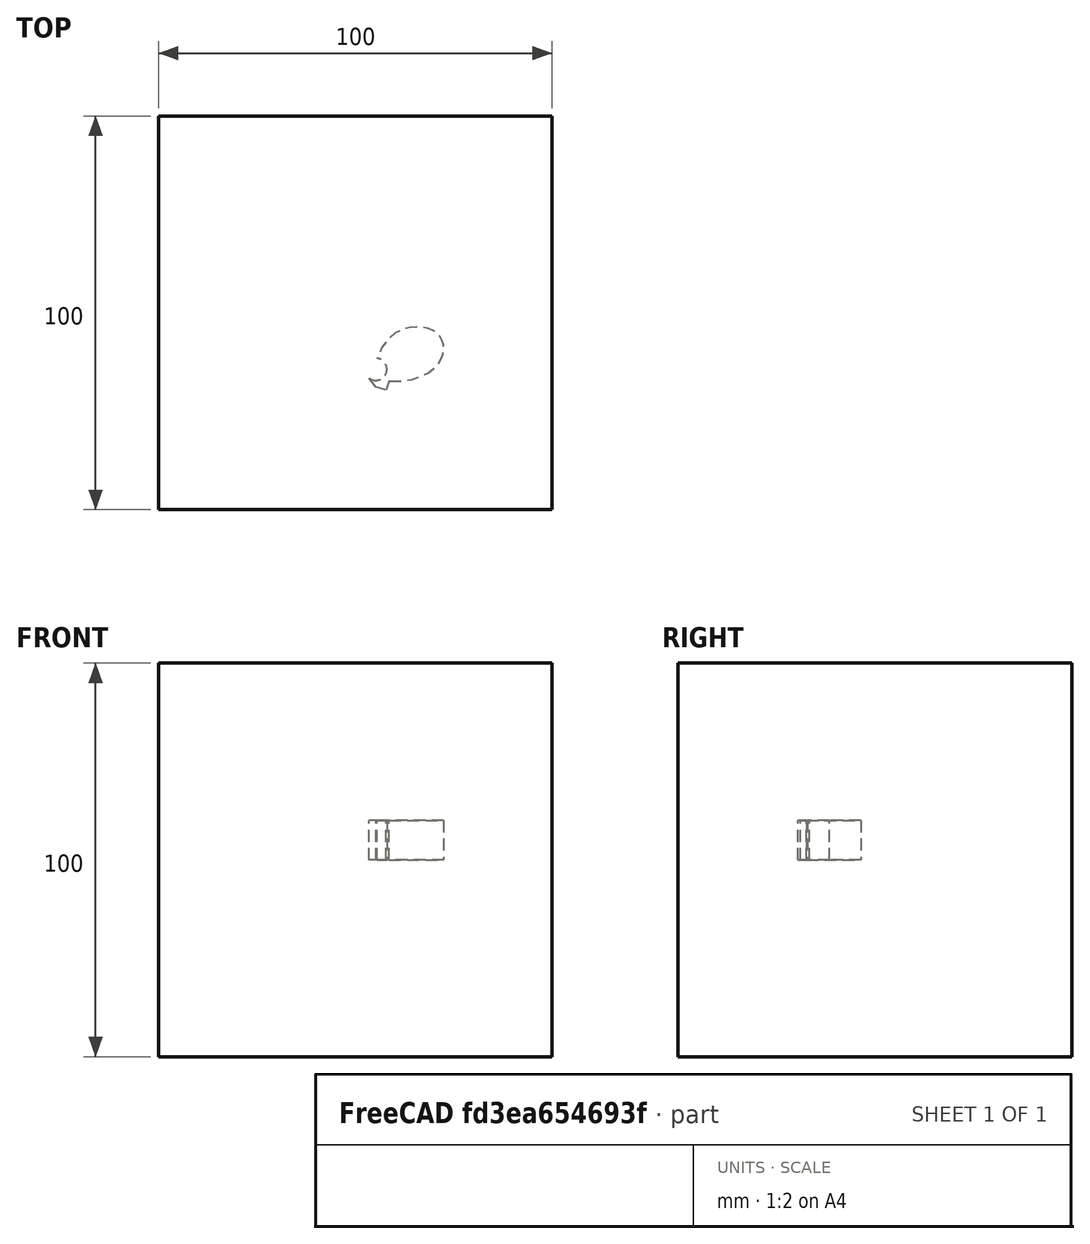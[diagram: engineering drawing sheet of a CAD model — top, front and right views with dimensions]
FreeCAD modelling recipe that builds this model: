
FCSTD DOCUMENT  (FreeCAD 0.19RUnknown)
Label: mirrorTest-1b
License: All rights reserved
LicenseURL: http://en.wikipedia.org/wiki/All_rights_reserved
objects: App::DocumentObjectGroupPython×1248, App::Part×2, Part::FeaturePython×1, Sketcher::SketchObject×1, Part::Extrusion×1, Part::Mirroring×1
note: 4 computed .brp shape members not serialized (recipe doc carries the construction recipe); baked Part::Feature solids carry a one-line shape summary decoded from their .brp

FEATURE [App::DocumentObjectGroupPython] HALFPI  # scripted group (container) (typed FeaturePython)
  name = HALFPI
  value = pi/2.
FEATURE [App::DocumentObjectGroupPython] PI  # scripted group (container) (typed FeaturePython)
  name = PI
  value = 1.*pi
FEATURE [App::DocumentObjectGroupPython] TWOPI  # scripted group (container) (typed FeaturePython)
  name = TWOPI
  value = 2.*pi
FEATURE [App::DocumentObjectGroupPython] Constants  # scripted group (container) (typed FeaturePython)
  Group = -> [HALFPI,PI,TWOPI]
FEATURE [App::DocumentObjectGroupPython] Variables  # scripted group (container) (typed FeaturePython)
FEATURE [App::DocumentObjectGroupPython] Quantities  # scripted group (container) (typed FeaturePython)
FEATURE [App::DocumentObjectGroupPython] Isotopes  # scripted group (container) (typed FeaturePython)
FEATURE [App::DocumentObjectGroupPython] Elements  # scripted group (container) (typed FeaturePython)
FEATURE [App::DocumentObjectGroupPython] G4Isotopes  # scripted group (container) (typed FeaturePython)
FEATURE [App::DocumentObjectGroupPython] H_element  # scripted group (container) (typed FeaturePython)
  Z = 1
  atom_value = 1.008
  formula = H
  name = H_element
FEATURE [App::DocumentObjectGroupPython] He_element  # scripted group (container) (typed FeaturePython)
  Z = 2
  atom_value = 4.0026
  formula = He
  name = He_element
FEATURE [App::DocumentObjectGroupPython] Li_element  # scripted group (container) (typed FeaturePython)
  Z = 3
  atom_value = 6.94
  formula = Li
  name = Li_element
FEATURE [App::DocumentObjectGroupPython] Be_element  # scripted group (container) (typed FeaturePython)
  Z = 4
  atom_value = 9.01218
  formula = Be
  name = Be_element
FEATURE [App::DocumentObjectGroupPython] B_element  # scripted group (container) (typed FeaturePython)
  Z = 5
  atom_value = 10.81
  formula = B
  name = B_element
FEATURE [App::DocumentObjectGroupPython] C_element  # scripted group (container) (typed FeaturePython)
  Z = 6
  atom_value = 12.011
  formula = C
  name = C_element
FEATURE [App::DocumentObjectGroupPython] N_element  # scripted group (container) (typed FeaturePython)
  Z = 7
  atom_value = 14.007
  formula = N
  name = N_element
FEATURE [App::DocumentObjectGroupPython] O_element  # scripted group (container) (typed FeaturePython)
  Z = 8
  atom_value = 15.999
  formula = O
  name = O_element
FEATURE [App::DocumentObjectGroupPython] F_element  # scripted group (container) (typed FeaturePython)
  Z = 9
  atom_value = 18.9984
  formula = F
  name = F_element
FEATURE [App::DocumentObjectGroupPython] Ne_element  # scripted group (container) (typed FeaturePython)
  Z = 10
  atom_value = 20.1797
  formula = Ne
  name = Ne_element
FEATURE [App::DocumentObjectGroupPython] Na_element  # scripted group (container) (typed FeaturePython)
  Z = 11
  atom_value = 22.9898
  formula = Na
  name = Na_element
FEATURE [App::DocumentObjectGroupPython] Mg_element  # scripted group (container) (typed FeaturePython)
  Z = 12
  atom_value = 24.305
  formula = Mg
  name = Mg_element
FEATURE [App::DocumentObjectGroupPython] Al_element  # scripted group (container) (typed FeaturePython)
  Z = 13
  atom_value = 26.9815
  formula = Al
  name = Al_element
FEATURE [App::DocumentObjectGroupPython] Si_element  # scripted group (container) (typed FeaturePython)
  Z = 14
  atom_value = 28.085
  formula = Si
  name = Si_element
FEATURE [App::DocumentObjectGroupPython] P_element  # scripted group (container) (typed FeaturePython)
  Z = 15
  atom_value = 30.9738
  formula = P
  name = P_element
FEATURE [App::DocumentObjectGroupPython] S_element  # scripted group (container) (typed FeaturePython)
  Z = 16
  atom_value = 32.06
  formula = S
  name = S_element
FEATURE [App::DocumentObjectGroupPython] Cl_element  # scripted group (container) (typed FeaturePython)
  Z = 17
  atom_value = 35.45
  formula = Cl
  name = Cl_element
FEATURE [App::DocumentObjectGroupPython] Ar_element  # scripted group (container) (typed FeaturePython)
  Z = 18
  atom_value = 39.95
  formula = Ar
  name = Ar_element
FEATURE [App::DocumentObjectGroupPython] K_element  # scripted group (container) (typed FeaturePython)
  Z = 19
  atom_value = 39.0983
  formula = K
  name = K_element
FEATURE [App::DocumentObjectGroupPython] Ca_element  # scripted group (container) (typed FeaturePython)
  Z = 20
  atom_value = 40.078
  formula = Ca
  name = Ca_element
FEATURE [App::DocumentObjectGroupPython] Sc_element  # scripted group (container) (typed FeaturePython)
  Z = 21
  atom_value = 44.9559
  formula = Sc
  name = Sc_element
FEATURE [App::DocumentObjectGroupPython] Ti_element  # scripted group (container) (typed FeaturePython)
  Z = 22
  atom_value = 47.867
  formula = Ti
  name = Ti_element
FEATURE [App::DocumentObjectGroupPython] V_element  # scripted group (container) (typed FeaturePython)
  Z = 23
  atom_value = 50.9415
  formula = V
  name = V_element
FEATURE [App::DocumentObjectGroupPython] Cr_element  # scripted group (container) (typed FeaturePython)
  Z = 24
  atom_value = 51.9961
  formula = Cr
  name = Cr_element
FEATURE [App::DocumentObjectGroupPython] Mn_element  # scripted group (container) (typed FeaturePython)
  Z = 25
  atom_value = 54.938
  formula = Mn
  name = Mn_element
FEATURE [App::DocumentObjectGroupPython] Fe_element  # scripted group (container) (typed FeaturePython)
  Z = 26
  atom_value = 55.845
  formula = Fe
  name = Fe_element
FEATURE [App::DocumentObjectGroupPython] Co_element  # scripted group (container) (typed FeaturePython)
  Z = 27
  atom_value = 58.9332
  formula = Co
  name = Co_element
FEATURE [App::DocumentObjectGroupPython] Ni_element  # scripted group (container) (typed FeaturePython)
  Z = 28
  atom_value = 58.6934
  formula = Ni
  name = Ni_element
FEATURE [App::DocumentObjectGroupPython] Cu_element  # scripted group (container) (typed FeaturePython)
  Z = 29
  atom_value = 63.546
  formula = Cu
  name = Cu_element
FEATURE [App::DocumentObjectGroupPython] Zn_element  # scripted group (container) (typed FeaturePython)
  Z = 30
  atom_value = 65.38
  formula = Zn
  name = Zn_element
FEATURE [App::DocumentObjectGroupPython] Ga_element  # scripted group (container) (typed FeaturePython)
  Z = 31
  atom_value = 69.723
  formula = Ga
  name = Ga_element
FEATURE [App::DocumentObjectGroupPython] Ge_element  # scripted group (container) (typed FeaturePython)
  Z = 32
  atom_value = 72.63
  formula = Ge
  name = Ge_element
FEATURE [App::DocumentObjectGroupPython] As_element  # scripted group (container) (typed FeaturePython)
  Z = 33
  atom_value = 74.9216
  formula = As
  name = As_element
FEATURE [App::DocumentObjectGroupPython] Se_element  # scripted group (container) (typed FeaturePython)
  Z = 34
  atom_value = 78.971
  formula = Se
  name = Se_element
FEATURE [App::DocumentObjectGroupPython] Br_element  # scripted group (container) (typed FeaturePython)
  Z = 35
  atom_value = 79.904
  formula = Br
  name = Br_element
FEATURE [App::DocumentObjectGroupPython] Kr_element  # scripted group (container) (typed FeaturePython)
  Z = 36
  atom_value = 83.798
  formula = Kr
  name = Kr_element
FEATURE [App::DocumentObjectGroupPython] Rb_element  # scripted group (container) (typed FeaturePython)
  Z = 37
  atom_value = 85.4678
  formula = Rb
  name = Rb_element
FEATURE [App::DocumentObjectGroupPython] Sr_element  # scripted group (container) (typed FeaturePython)
  Z = 38
  atom_value = 87.62
  formula = Sr
  name = Sr_element
FEATURE [App::DocumentObjectGroupPython] Y_element  # scripted group (container) (typed FeaturePython)
  Z = 39
  atom_value = 88.9058
  formula = Y
  name = Y_element
FEATURE [App::DocumentObjectGroupPython] Zr_element  # scripted group (container) (typed FeaturePython)
  Z = 40
  atom_value = 91.224
  formula = Zr
  name = Zr_element
FEATURE [App::DocumentObjectGroupPython] Nb_element  # scripted group (container) (typed FeaturePython)
  Z = 41
  atom_value = 92.9064
  formula = Nb
  name = Nb_element
FEATURE [App::DocumentObjectGroupPython] Mo_element  # scripted group (container) (typed FeaturePython)
  Z = 42
  atom_value = 95.95
  formula = Mo
  name = Mo_element
FEATURE [App::DocumentObjectGroupPython] Tc_element  # scripted group (container) (typed FeaturePython)
  Z = 43
  atom_value = 97
  formula = Tc
  name = Tc_element
FEATURE [App::DocumentObjectGroupPython] Ru_element  # scripted group (container) (typed FeaturePython)
  Z = 44
  atom_value = 101.07
  formula = Ru
  name = Ru_element
FEATURE [App::DocumentObjectGroupPython] Rh_element  # scripted group (container) (typed FeaturePython)
  Z = 45
  atom_value = 102.905
  formula = Rh
  name = Rh_element
FEATURE [App::DocumentObjectGroupPython] Pd_element  # scripted group (container) (typed FeaturePython)
  Z = 46
  atom_value = 106.42
  formula = Pd
  name = Pd_element
FEATURE [App::DocumentObjectGroupPython] Ag_element  # scripted group (container) (typed FeaturePython)
  Z = 47
  atom_value = 107.868
  formula = Ag
  name = Ag_element
FEATURE [App::DocumentObjectGroupPython] Cd_element  # scripted group (container) (typed FeaturePython)
  Z = 48
  atom_value = 112.414
  formula = Cd
  name = Cd_element
FEATURE [App::DocumentObjectGroupPython] In_element  # scripted group (container) (typed FeaturePython)
  Z = 49
  atom_value = 114.818
  formula = In
  name = In_element
FEATURE [App::DocumentObjectGroupPython] Sn_element  # scripted group (container) (typed FeaturePython)
  Z = 50
  atom_value = 118.71
  formula = Sn
  name = Sn_element
FEATURE [App::DocumentObjectGroupPython] Sb_element  # scripted group (container) (typed FeaturePython)
  Z = 51
  atom_value = 121.76
  formula = Sb
  name = Sb_element
FEATURE [App::DocumentObjectGroupPython] Te_element  # scripted group (container) (typed FeaturePython)
  Z = 52
  atom_value = 127.6
  formula = Te
  name = Te_element
FEATURE [App::DocumentObjectGroupPython] I_element  # scripted group (container) (typed FeaturePython)
  Z = 53
  atom_value = 126.904
  formula = I
  name = I_element
FEATURE [App::DocumentObjectGroupPython] Xe_element  # scripted group (container) (typed FeaturePython)
  Z = 54
  atom_value = 131.293
  formula = Xe
  name = Xe_element
FEATURE [App::DocumentObjectGroupPython] Cs_element  # scripted group (container) (typed FeaturePython)
  Z = 55
  atom_value = 132.905
  formula = Cs
  name = Cs_element
FEATURE [App::DocumentObjectGroupPython] Ba_element  # scripted group (container) (typed FeaturePython)
  Z = 56
  atom_value = 137.327
  formula = Ba
  name = Ba_element
FEATURE [App::DocumentObjectGroupPython] La_element  # scripted group (container) (typed FeaturePython)
  Z = 57
  atom_value = 138.905
  formula = La
  name = La_element
FEATURE [App::DocumentObjectGroupPython] Ce_element  # scripted group (container) (typed FeaturePython)
  Z = 58
  atom_value = 140.116
  formula = Ce
  name = Ce_element
FEATURE [App::DocumentObjectGroupPython] Pr_element  # scripted group (container) (typed FeaturePython)
  Z = 59
  atom_value = 140.908
  formula = Pr
  name = Pr_element
FEATURE [App::DocumentObjectGroupPython] Nd_element  # scripted group (container) (typed FeaturePython)
  Z = 60
  atom_value = 144.242
  formula = Nd
  name = Nd_element
FEATURE [App::DocumentObjectGroupPython] Pm_element  # scripted group (container) (typed FeaturePython)
  Z = 61
  atom_value = 145
  formula = Pm
  name = Pm_element
FEATURE [App::DocumentObjectGroupPython] Sm_element  # scripted group (container) (typed FeaturePython)
  Z = 62
  atom_value = 150.36
  formula = Sm
  name = Sm_element
FEATURE [App::DocumentObjectGroupPython] Eu_element  # scripted group (container) (typed FeaturePython)
  Z = 63
  atom_value = 151.964
  formula = Eu
  name = Eu_element
FEATURE [App::DocumentObjectGroupPython] Gd_element  # scripted group (container) (typed FeaturePython)
  Z = 64
  atom_value = 157.25
  formula = Gd
  name = Gd_element
FEATURE [App::DocumentObjectGroupPython] Tb_element  # scripted group (container) (typed FeaturePython)
  Z = 65
  atom_value = 158.925
  formula = Tb
  name = Tb_element
FEATURE [App::DocumentObjectGroupPython] Dy_element  # scripted group (container) (typed FeaturePython)
  Z = 66
  atom_value = 162.5
  formula = Dy
  name = Dy_element
FEATURE [App::DocumentObjectGroupPython] Ho_element  # scripted group (container) (typed FeaturePython)
  Z = 67
  atom_value = 164.93
  formula = Ho
  name = Ho_element
FEATURE [App::DocumentObjectGroupPython] Er_element  # scripted group (container) (typed FeaturePython)
  Z = 68
  atom_value = 167.259
  formula = Er
  name = Er_element
FEATURE [App::DocumentObjectGroupPython] Tm_element  # scripted group (container) (typed FeaturePython)
  Z = 69
  atom_value = 168.934
  formula = Tm
  name = Tm_element
FEATURE [App::DocumentObjectGroupPython] Yb_element  # scripted group (container) (typed FeaturePython)
  Z = 70
  atom_value = 173.045
  formula = Yb
  name = Yb_element
FEATURE [App::DocumentObjectGroupPython] Lu_element  # scripted group (container) (typed FeaturePython)
  Z = 71
  atom_value = 174.967
  formula = Lu
  name = Lu_element
FEATURE [App::DocumentObjectGroupPython] Hf_element  # scripted group (container) (typed FeaturePython)
  Z = 72
  atom_value = 178.49
  formula = Hf
  name = Hf_element
FEATURE [App::DocumentObjectGroupPython] Ta_element  # scripted group (container) (typed FeaturePython)
  Z = 73
  atom_value = 180.948
  formula = Ta
  name = Ta_element
FEATURE [App::DocumentObjectGroupPython] W_element  # scripted group (container) (typed FeaturePython)
  Z = 74
  atom_value = 183.84
  formula = W
  name = W_element
FEATURE [App::DocumentObjectGroupPython] Re_element  # scripted group (container) (typed FeaturePython)
  Z = 75
  atom_value = 186.207
  formula = Re
  name = Re_element
FEATURE [App::DocumentObjectGroupPython] Os_element  # scripted group (container) (typed FeaturePython)
  Z = 76
  atom_value = 190.23
  formula = Os
  name = Os_element
FEATURE [App::DocumentObjectGroupPython] Ir_element  # scripted group (container) (typed FeaturePython)
  Z = 77
  atom_value = 192.217
  formula = Ir
  name = Ir_element
FEATURE [App::DocumentObjectGroupPython] Pt_element  # scripted group (container) (typed FeaturePython)
  Z = 78
  atom_value = 195.084
  formula = Pt
  name = Pt_element
FEATURE [App::DocumentObjectGroupPython] Au_element  # scripted group (container) (typed FeaturePython)
  Z = 79
  atom_value = 196.967
  formula = Au
  name = Au_element
FEATURE [App::DocumentObjectGroupPython] Hg_element  # scripted group (container) (typed FeaturePython)
  Z = 80
  atom_value = 200.592
  formula = Hg
  name = Hg_element
FEATURE [App::DocumentObjectGroupPython] Tl_element  # scripted group (container) (typed FeaturePython)
  Z = 81
  atom_value = 204.38
  formula = Tl
  name = Tl_element
FEATURE [App::DocumentObjectGroupPython] Pb_element  # scripted group (container) (typed FeaturePython)
  Z = 82
  atom_value = 207.2
  formula = Pb
  name = Pb_element
FEATURE [App::DocumentObjectGroupPython] Bi_element  # scripted group (container) (typed FeaturePython)
  Z = 83
  atom_value = 208.98
  formula = Bi
  name = Bi_element
FEATURE [App::DocumentObjectGroupPython] Po_element  # scripted group (container) (typed FeaturePython)
  Z = 84
  atom_value = 209
  formula = Po
  name = Po_element
FEATURE [App::DocumentObjectGroupPython] At_element  # scripted group (container) (typed FeaturePython)
  Z = 85
  atom_value = 210
  formula = At
  name = At_element
FEATURE [App::DocumentObjectGroupPython] Rn_element  # scripted group (container) (typed FeaturePython)
  Z = 86
  atom_value = 222
  formula = Rn
  name = Rn_element
FEATURE [App::DocumentObjectGroupPython] Fr_element  # scripted group (container) (typed FeaturePython)
  Z = 87
  atom_value = 223
  formula = Fr
  name = Fr_element
FEATURE [App::DocumentObjectGroupPython] Ra_element  # scripted group (container) (typed FeaturePython)
  Z = 88
  atom_value = 226
  formula = Ra
  name = Ra_element
FEATURE [App::DocumentObjectGroupPython] Ac_element  # scripted group (container) (typed FeaturePython)
  Z = 89
  atom_value = 227
  formula = Ac
  name = Ac_element
FEATURE [App::DocumentObjectGroupPython] Th_element  # scripted group (container) (typed FeaturePython)
  Z = 90
  atom_value = 232.038
  formula = Th
  name = Th_element
FEATURE [App::DocumentObjectGroupPython] Pa_element  # scripted group (container) (typed FeaturePython)
  Z = 91
  atom_value = 231.036
  formula = Pa
  name = Pa_element
FEATURE [App::DocumentObjectGroupPython] U_element  # scripted group (container) (typed FeaturePython)
  Z = 92
  atom_value = 238.029
  formula = U
  name = U_element
FEATURE [App::DocumentObjectGroupPython] Np_element  # scripted group (container) (typed FeaturePython)
  Z = 93
  atom_value = 237
  formula = Np
  name = Np_element
FEATURE [App::DocumentObjectGroupPython] Pu_element  # scripted group (container) (typed FeaturePython)
  Z = 94
  atom_value = 244
  formula = Pu
  name = Pu_element
FEATURE [App::DocumentObjectGroupPython] Am_element  # scripted group (container) (typed FeaturePython)
  Z = 95
  atom_value = 243
  formula = Am
  name = Am_element
FEATURE [App::DocumentObjectGroupPython] Cm_element  # scripted group (container) (typed FeaturePython)
  Z = 96
  atom_value = 247
  formula = Cm
  name = Cm_element
FEATURE [App::DocumentObjectGroupPython] Bk_element  # scripted group (container) (typed FeaturePython)
  Z = 97
  atom_value = 247
  formula = Bk
  name = Bk_element
FEATURE [App::DocumentObjectGroupPython] Cf_element  # scripted group (container) (typed FeaturePython)
  Z = 98
  atom_value = 251
  formula = Cf
  name = Cf_element
FEATURE [App::DocumentObjectGroupPython] G4Elements  # scripted group (container) (typed FeaturePython)
  Group = -> [H_element,He_element,Li_element,Be_element,B_element,C_element,N_element,O_element,F_element,Ne_element,Na_element,Mg_element,Al_element,Si_element,P_element,S_element,Cl_element,Ar_element,K_element,Ca_element,Sc_element,Ti_element,V_element,Cr_element,Mn_element,Fe_element,Co_element,Ni_element,Cu_element,Zn_element,Ga_element,Ge_element,As_element,Se_element,Br_element,Kr_element,Rb_element,+61 more]
FEATURE [App::DocumentObjectGroupPython] H_element001  label="H_element : 0.101"  # scripted group (container) (typed FeaturePython)
  n = 0.101327
FEATURE [App::DocumentObjectGroupPython] C_element001  label="C_element : 0.775"  # scripted group (container) (typed FeaturePython)
  n = 0.7755
FEATURE [App::DocumentObjectGroupPython] N_element001  label="N_element : 0.035"  # scripted group (container) (typed FeaturePython)
  n = 0.035057
FEATURE [App::DocumentObjectGroupPython] O_element001  label="O_element : 0.052"  # scripted group (container) (typed FeaturePython)
  n = 0.0523159
FEATURE [App::DocumentObjectGroupPython] F_element001  label="F_element : 0.017"  # scripted group (container) (typed FeaturePython)
  n = 0.017422
FEATURE [App::DocumentObjectGroupPython] Ca_element001  label="Ca_element : 0.018"  # scripted group (container) (typed FeaturePython)
  n = 0.018378
FEATURE [App::DocumentObjectGroupPython] G4_A_150_TISSUE  label="G4_A-150_TISSUE"  # scripted group (container) (typed FeaturePython)
  Dunit = g/cm3
  Dvalue = 1.127
  Group = -> [H_element001,C_element001,N_element001,O_element001,F_element001,Ca_element001]
  conduct = 2
  density = 1
  expand = 3
  formula = G4_A-150_TISSUE
  name = G4_A-150_TISSUE
  specific = 4
FEATURE [App::DocumentObjectGroupPython] C_element002  label="C_element : 3"  # scripted group (container) (typed FeaturePython)
  n = 3
  ref = C_element
FEATURE [App::DocumentObjectGroupPython] H_element002  label="H_element : 6"  # scripted group (container) (typed FeaturePython)
  n = 6
  ref = H_element
FEATURE [App::DocumentObjectGroupPython] O_element002  label="O_element : 1"  # scripted group (container) (typed FeaturePython)
  n = 1
  ref = O_element
FEATURE [App::DocumentObjectGroupPython] G4_ACETONE  # scripted group (container) (typed FeaturePython)
  Dunit = g/cm3
  Dvalue = 0.7899
  Group = -> [C_element002,H_element002,O_element002]
  conduct = 2
  density = 1
  expand = 3
  formula = G4_ACETONE
  name = G4_ACETONE
  specific = 4
FEATURE [App::DocumentObjectGroupPython] C_element003  label="C_element : 2"  # scripted group (container) (typed FeaturePython)
  n = 2
  ref = C_element
FEATURE [App::DocumentObjectGroupPython] H_element003  label="H_element : 2"  # scripted group (container) (typed FeaturePython)
  n = 2
  ref = H_element
FEATURE [App::DocumentObjectGroupPython] G4_ACETYLENE  # scripted group (container) (typed FeaturePython)
  Dunit = g/cm3
  Dvalue = 0.0010967
  Group = -> [C_element003,H_element003]
  conduct = 2
  density = 1
  expand = 3
  formula = G4_ACETYLENE
  name = G4_ACETYLENE
  specific = 4
FEATURE [App::DocumentObjectGroupPython] C_element004  label="C_element : 5"  # scripted group (container) (typed FeaturePython)
  n = 5
  ref = C_element
FEATURE [App::DocumentObjectGroupPython] H_element004  label="H_element : 5"  # scripted group (container) (typed FeaturePython)
  n = 5
  ref = H_element
FEATURE [App::DocumentObjectGroupPython] N_element002  label="N_element : 5"  # scripted group (container) (typed FeaturePython)
  n = 5
  ref = N_element
FEATURE [App::DocumentObjectGroupPython] G4_ADENINE  # scripted group (container) (typed FeaturePython)
  Dunit = g/cm3
  Dvalue = 1.6
  Group = -> [C_element004,H_element004,N_element002]
  conduct = 2
  density = 1
  expand = 3
  formula = G4_ADENINE
  name = G4_ADENINE
  specific = 4
FEATURE [App::DocumentObjectGroupPython] H_element005  label="H_element : 0.114"  # scripted group (container) (typed FeaturePython)
  n = 0.114
FEATURE [App::DocumentObjectGroupPython] C_element005  label="C_element : 0.598"  # scripted group (container) (typed FeaturePython)
  n = 0.598
FEATURE [App::DocumentObjectGroupPython] N_element003  label="N_element : 0.007"  # scripted group (container) (typed FeaturePython)
  n = 0.007
FEATURE [App::DocumentObjectGroupPython] O_element003  label="O_element : 0.278"  # scripted group (container) (typed FeaturePython)
  n = 0.278
FEATURE [App::DocumentObjectGroupPython] Na_element001  label="Na_element : 0.001"  # scripted group (container) (typed FeaturePython)
  n = 0.001
FEATURE [App::DocumentObjectGroupPython] S_element001  label="S_element : 0.001"  # scripted group (container) (typed FeaturePython)
  n = 0.001
FEATURE [App::DocumentObjectGroupPython] Cl_element001  label="Cl_element : 0.001"  # scripted group (container) (typed FeaturePython)
  n = 0.001
FEATURE [App::DocumentObjectGroupPython] G4_ADIPOSE_TISSUE_ICRP  # scripted group (container) (typed FeaturePython)
  Dunit = g/cm3
  Dvalue = 0.95
  Group = -> [H_element005,C_element005,N_element003,O_element003,Na_element001,S_element001,Cl_element001]
  conduct = 2
  density = 1
  expand = 3
  formula = G4_ADIPOSE_TISSUE_ICRP
  name = G4_ADIPOSE_TISSUE_ICRP
  specific = 4
FEATURE [App::DocumentObjectGroupPython] C_element006  label="C_element : 0.000"  # scripted group (container) (typed FeaturePython)
  n = 0.000124
FEATURE [App::DocumentObjectGroupPython] N_element004  label="N_element : 0.755"  # scripted group (container) (typed FeaturePython)
  n = 0.755268
FEATURE [App::DocumentObjectGroupPython] O_element004  label="O_element : 0.232"  # scripted group (container) (typed FeaturePython)
  n = 0.231781
FEATURE [App::DocumentObjectGroupPython] Ar_element001  label="Ar_element : 0.013"  # scripted group (container) (typed FeaturePython)
  n = 0.012827
FEATURE [App::DocumentObjectGroupPython] G4_AIR  # scripted group (container) (typed FeaturePython)
  Dunit = g/cm3
  Dvalue = 0.00120479
  Group = -> [C_element006,N_element004,O_element004,Ar_element001]
  conduct = 2
  density = 1
  expand = 3
  formula = G4_AIR
  name = G4_AIR
  specific = 4
FEATURE [App::DocumentObjectGroupPython] C_element007  label="C_element : 006"  # scripted group (container) (typed FeaturePython)
  n = 3
  ref = C_element
FEATURE [App::DocumentObjectGroupPython] H_element006  label="H_element : 7"  # scripted group (container) (typed FeaturePython)
  n = 7
  ref = H_element
FEATURE [App::DocumentObjectGroupPython] N_element005  label="N_element : 1"  # scripted group (container) (typed FeaturePython)
  n = 1
  ref = N_element
FEATURE [App::DocumentObjectGroupPython] O_element005  label="O_element : 2"  # scripted group (container) (typed FeaturePython)
  n = 2
  ref = O_element
FEATURE [App::DocumentObjectGroupPython] G4_ALANINE  # scripted group (container) (typed FeaturePython)
  Dunit = g/cm3
  Dvalue = 1.42
  Group = -> [C_element007,H_element006,N_element005,O_element005]
  conduct = 2
  density = 1
  expand = 3
  formula = G4_ALANINE
  name = G4_ALANINE
  specific = 4
FEATURE [App::DocumentObjectGroupPython] Al_element001  label="Al_element : 2"  # scripted group (container) (typed FeaturePython)
  n = 2
  ref = Al_element
FEATURE [App::DocumentObjectGroupPython] O_element006  label="O_element : 3"  # scripted group (container) (typed FeaturePython)
  n = 3
  ref = O_element
FEATURE [App::DocumentObjectGroupPython] G4_ALUMINUM_OXIDE  # scripted group (container) (typed FeaturePython)
  Dunit = g/cm3
  Dvalue = 3.97
  Group = -> [Al_element001,O_element006]
  conduct = 2
  density = 1
  expand = 3
  formula = G4_ALUMINUM_OXIDE
  name = G4_ALUMINUM_OXIDE
  specific = 4
FEATURE [App::DocumentObjectGroupPython] H_element007  label="H_element : 0.106"  # scripted group (container) (typed FeaturePython)
  n = 0.10593
FEATURE [App::DocumentObjectGroupPython] C_element008  label="C_element : 0.789"  # scripted group (container) (typed FeaturePython)
  n = 0.788974
FEATURE [App::DocumentObjectGroupPython] O_element007  label="O_element : 0.105"  # scripted group (container) (typed FeaturePython)
  n = 0.105096
FEATURE [App::DocumentObjectGroupPython] G4_AMBER  # scripted group (container) (typed FeaturePython)
  Dunit = g/cm3
  Dvalue = 1.1
  Group = -> [H_element007,C_element008,O_element007]
  conduct = 2
  density = 1
  expand = 3
  formula = G4_AMBER
  name = G4_AMBER
  specific = 4
FEATURE [App::DocumentObjectGroupPython] N_element006  label="N_element : 006"  # scripted group (container) (typed FeaturePython)
  n = 1
  ref = N_element
FEATURE [App::DocumentObjectGroupPython] H_element008  label="H_element : 3"  # scripted group (container) (typed FeaturePython)
  n = 3
  ref = H_element
FEATURE [App::DocumentObjectGroupPython] G4_AMMONIA  # scripted group (container) (typed FeaturePython)
  Dunit = g/cm3
  Dvalue = 0.000826019
  Group = -> [N_element006,H_element008]
  conduct = 2
  density = 1
  expand = 3
  formula = G4_AMMONIA
  name = G4_AMMONIA
  specific = 4
FEATURE [App::DocumentObjectGroupPython] C_element009  label="C_element : 6"  # scripted group (container) (typed FeaturePython)
  n = 6
  ref = C_element
FEATURE [App::DocumentObjectGroupPython] H_element009  label="H_element : 008"  # scripted group (container) (typed FeaturePython)
  n = 7
  ref = H_element
FEATURE [App::DocumentObjectGroupPython] N_element007  label="N_element : 007"  # scripted group (container) (typed FeaturePython)
  n = 1
  ref = N_element
FEATURE [App::DocumentObjectGroupPython] G4_ANILINE  # scripted group (container) (typed FeaturePython)
  Dunit = g/cm3
  Dvalue = 1.0235
  Group = -> [C_element009,H_element009,N_element007]
  conduct = 2
  density = 1
  expand = 3
  formula = G4_ANILINE
  name = G4_ANILINE
  specific = 4
FEATURE [App::DocumentObjectGroupPython] C_element010  label="C_element : 14"  # scripted group (container) (typed FeaturePython)
  n = 14
  ref = C_element
FEATURE [App::DocumentObjectGroupPython] H_element010  label="H_element : 10"  # scripted group (container) (typed FeaturePython)
  n = 10
  ref = H_element
FEATURE [App::DocumentObjectGroupPython] G4_ANTHRACENE  # scripted group (container) (typed FeaturePython)
  Dunit = g/cm3
  Dvalue = 1.283
  Group = -> [C_element010,H_element010]
  conduct = 2
  density = 1
  expand = 3
  formula = G4_ANTHRACENE
  name = G4_ANTHRACENE
  specific = 4
FEATURE [App::DocumentObjectGroupPython] H_element011  label="H_element : 0.065"  # scripted group (container) (typed FeaturePython)
  n = 0.0654709
FEATURE [App::DocumentObjectGroupPython] C_element011  label="C_element : 0.537"  # scripted group (container) (typed FeaturePython)
  n = 0.536944
FEATURE [App::DocumentObjectGroupPython] N_element008  label="N_element : 0.021"  # scripted group (container) (typed FeaturePython)
  n = 0.0215
FEATURE [App::DocumentObjectGroupPython] O_element008  label="O_element : 0.032"  # scripted group (container) (typed FeaturePython)
  n = 0.032085
FEATURE [App::DocumentObjectGroupPython] F_element002  label="F_element : 0.167"  # scripted group (container) (typed FeaturePython)
  n = 0.167411
FEATURE [App::DocumentObjectGroupPython] Ca_element002  label="Ca_element : 0.177"  # scripted group (container) (typed FeaturePython)
  n = 0.176589
FEATURE [App::DocumentObjectGroupPython] G4_B_100_BONE  label="G4_B-100_BONE"  # scripted group (container) (typed FeaturePython)
  Dunit = g/cm3
  Dvalue = 1.45
  Group = -> [H_element011,C_element011,N_element008,O_element008,F_element002,Ca_element002]
  conduct = 2
  density = 1
  expand = 3
  formula = G4_B-100_BONE
  name = G4_B-100_BONE
  specific = 4
FEATURE [App::DocumentObjectGroupPython] H_element012  label="H_element : 0.057"  # scripted group (container) (typed FeaturePython)
  n = 0.057441
FEATURE [App::DocumentObjectGroupPython] C_element012  label="C_element : 0.790"  # scripted group (container) (typed FeaturePython)
  n = 0.774591
FEATURE [App::DocumentObjectGroupPython] O_element009  label="O_element : 0.168"  # scripted group (container) (typed FeaturePython)
  n = 0.167968
FEATURE [App::DocumentObjectGroupPython] G4_BAKELITE  # scripted group (container) (typed FeaturePython)
  Dunit = g/cm3
  Dvalue = 1.25
  Group = -> [H_element012,C_element012,O_element009]
  conduct = 2
  density = 1
  expand = 3
  formula = G4_BAKELITE
  name = G4_BAKELITE
  specific = 4
FEATURE [App::DocumentObjectGroupPython] Ba_element001  label="Ba_element : 1"  # scripted group (container) (typed FeaturePython)
  n = 1
  ref = Ba_element
FEATURE [App::DocumentObjectGroupPython] F_element003  label="F_element : 2"  # scripted group (container) (typed FeaturePython)
  n = 2
  ref = F_element
FEATURE [App::DocumentObjectGroupPython] G4_BARIUM_FLUORIDE  # scripted group (container) (typed FeaturePython)
  Dunit = g/cm3
  Dvalue = 4.89
  Group = -> [Ba_element001,F_element003]
  conduct = 2
  density = 1
  expand = 3
  formula = G4_BARIUM_FLUORIDE
  name = G4_BARIUM_FLUORIDE
  specific = 4
FEATURE [App::DocumentObjectGroupPython] Ba_element002  label="Ba_element : 002"  # scripted group (container) (typed FeaturePython)
  n = 1
  ref = Ba_element
FEATURE [App::DocumentObjectGroupPython] S_element002  label="S_element : 1"  # scripted group (container) (typed FeaturePython)
  n = 1
  ref = S_element
FEATURE [App::DocumentObjectGroupPython] O_element010  label="O_element : 4"  # scripted group (container) (typed FeaturePython)
  n = 4
  ref = O_element
FEATURE [App::DocumentObjectGroupPython] G4_BARIUM_SULFATE  # scripted group (container) (typed FeaturePython)
  Dunit = g/cm3
  Dvalue = 4.5
  Group = -> [Ba_element002,S_element002,O_element010]
  conduct = 2
  density = 1
  expand = 3
  formula = G4_BARIUM_SULFATE
  name = G4_BARIUM_SULFATE
  specific = 4
FEATURE [App::DocumentObjectGroupPython] C_element013  label="C_element : 007"  # scripted group (container) (typed FeaturePython)
  n = 6
  ref = C_element
FEATURE [App::DocumentObjectGroupPython] H_element013  label="H_element : 009"  # scripted group (container) (typed FeaturePython)
  n = 6
  ref = H_element
FEATURE [App::DocumentObjectGroupPython] G4_BENZENE  # scripted group (container) (typed FeaturePython)
  Dunit = g/cm3
  Dvalue = 0.87865
  Group = -> [C_element013,H_element013]
  conduct = 2
  density = 1
  expand = 3
  formula = G4_BENZENE
  name = G4_BENZENE
  specific = 4
FEATURE [App::DocumentObjectGroupPython] Be_element001  label="Be_element : 1"  # scripted group (container) (typed FeaturePython)
  n = 1
  ref = Be_element
FEATURE [App::DocumentObjectGroupPython] O_element011  label="O_element : 005"  # scripted group (container) (typed FeaturePython)
  n = 1
  ref = O_element
FEATURE [App::DocumentObjectGroupPython] G4_BERYLLIUM_OXIDE  # scripted group (container) (typed FeaturePython)
  Dunit = g/cm3
  Dvalue = 3.01
  Group = -> [Be_element001,O_element011]
  conduct = 2
  density = 1
  expand = 3
  formula = G4_BERYLLIUM_OXIDE
  name = G4_BERYLLIUM_OXIDE
  specific = 4
FEATURE [App::DocumentObjectGroupPython] Bi_element001  label="Bi_element : 4"  # scripted group (container) (typed FeaturePython)
  n = 4
  ref = Bi_element
FEATURE [App::DocumentObjectGroupPython] Ge_element001  label="Ge_element : 3"  # scripted group (container) (typed FeaturePython)
  n = 3
  ref = Ge_element
FEATURE [App::DocumentObjectGroupPython] O_element012  label="O_element : 12"  # scripted group (container) (typed FeaturePython)
  n = 12
  ref = O_element
FEATURE [App::DocumentObjectGroupPython] G4_BGO  # scripted group (container) (typed FeaturePython)
  Dunit = g/cm3
  Dvalue = 7.13
  Group = -> [Bi_element001,Ge_element001,O_element012]
  conduct = 2
  density = 1
  expand = 3
  formula = G4_BGO
  name = G4_BGO
  specific = 4
FEATURE [App::DocumentObjectGroupPython] H_element014  label="H_element : 0.102"  # scripted group (container) (typed FeaturePython)
  n = 0.102
FEATURE [App::DocumentObjectGroupPython] C_element014  label="C_element : 0.110"  # scripted group (container) (typed FeaturePython)
  n = 0.11
FEATURE [App::DocumentObjectGroupPython] N_element009  label="N_element : 0.033"  # scripted group (container) (typed FeaturePython)
  n = 0.033
FEATURE [App::DocumentObjectGroupPython] O_element013  label="O_element : 0.745"  # scripted group (container) (typed FeaturePython)
  n = 0.745
FEATURE [App::DocumentObjectGroupPython] Na_element002  label="Na_element : 0.002"  # scripted group (container) (typed FeaturePython)
  n = 0.001
FEATURE [App::DocumentObjectGroupPython] P_element001  label="P_element : 0.001"  # scripted group (container) (typed FeaturePython)
  n = 0.001
FEATURE [App::DocumentObjectGroupPython] S_element003  label="S_element : 0.002"  # scripted group (container) (typed FeaturePython)
  n = 0.002
FEATURE [App::DocumentObjectGroupPython] Cl_element002  label="Cl_element : 0.003"  # scripted group (container) (typed FeaturePython)
  n = 0.003
FEATURE [App::DocumentObjectGroupPython] K_element001  label="K_element : 0.002"  # scripted group (container) (typed FeaturePython)
  n = 0.002
FEATURE [App::DocumentObjectGroupPython] Fe_element001  label="Fe_element : 0.001"  # scripted group (container) (typed FeaturePython)
  n = 0.001
FEATURE [App::DocumentObjectGroupPython] G4_BLOOD_ICRP  # scripted group (container) (typed FeaturePython)
  Dunit = g/cm3
  Dvalue = 1.06
  Group = -> [H_element014,C_element014,N_element009,O_element013,Na_element002,P_element001,S_element003,Cl_element002,K_element001,Fe_element001]
  conduct = 2
  density = 1
  expand = 3
  formula = G4_BLOOD_ICRP
  name = G4_BLOOD_ICRP
  specific = 4
FEATURE [App::DocumentObjectGroupPython] H_element015  label="H_element : 0.064"  # scripted group (container) (typed FeaturePython)
  n = 0.064
FEATURE [App::DocumentObjectGroupPython] C_element015  label="C_element : 0.278"  # scripted group (container) (typed FeaturePython)
  n = 0.278
FEATURE [App::DocumentObjectGroupPython] N_element010  label="N_element : 0.027"  # scripted group (container) (typed FeaturePython)
  n = 0.027
FEATURE [App::DocumentObjectGroupPython] O_element014  label="O_element : 0.410"  # scripted group (container) (typed FeaturePython)
  n = 0.41
FEATURE [App::DocumentObjectGroupPython] Mg_element001  label="Mg_element : 0.002"  # scripted group (container) (typed FeaturePython)
  n = 0.002
FEATURE [App::DocumentObjectGroupPython] P_element002  label="P_element : 0.070"  # scripted group (container) (typed FeaturePython)
  n = 0.07
FEATURE [App::DocumentObjectGroupPython] S_element004  label="S_element : 0.003"  # scripted group (container) (typed FeaturePython)
  n = 0.002
FEATURE [App::DocumentObjectGroupPython] Ca_element003  label="Ca_element : 0.147"  # scripted group (container) (typed FeaturePython)
  n = 0.147
FEATURE [App::DocumentObjectGroupPython] G4_BONE_COMPACT_ICRU  # scripted group (container) (typed FeaturePython)
  Dunit = g/cm3
  Dvalue = 1.85
  Group = -> [H_element015,C_element015,N_element010,O_element014,Mg_element001,P_element002,S_element004,Ca_element003]
  conduct = 2
  density = 1
  expand = 3
  formula = G4_BONE_COMPACT_ICRU
  name = G4_BONE_COMPACT_ICRU
  specific = 4
FEATURE [App::DocumentObjectGroupPython] H_element016  label="H_element : 0.034"  # scripted group (container) (typed FeaturePython)
  n = 0.034
FEATURE [App::DocumentObjectGroupPython] C_element016  label="C_element : 0.155"  # scripted group (container) (typed FeaturePython)
  n = 0.155
FEATURE [App::DocumentObjectGroupPython] N_element011  label="N_element : 0.042"  # scripted group (container) (typed FeaturePython)
  n = 0.042
FEATURE [App::DocumentObjectGroupPython] O_element015  label="O_element : 0.435"  # scripted group (container) (typed FeaturePython)
  n = 0.435
FEATURE [App::DocumentObjectGroupPython] Na_element003  label="Na_element : 0.003"  # scripted group (container) (typed FeaturePython)
  n = 0.001
FEATURE [App::DocumentObjectGroupPython] Mg_element002  label="Mg_element : 0.003"  # scripted group (container) (typed FeaturePython)
  n = 0.002
FEATURE [App::DocumentObjectGroupPython] P_element003  label="P_element : 0.103"  # scripted group (container) (typed FeaturePython)
  n = 0.103
FEATURE [App::DocumentObjectGroupPython] S_element005  label="S_element : 0.004"  # scripted group (container) (typed FeaturePython)
  n = 0.003
FEATURE [App::DocumentObjectGroupPython] Ca_element004  label="Ca_element : 0.225"  # scripted group (container) (typed FeaturePython)
  n = 0.225
FEATURE [App::DocumentObjectGroupPython] G4_BONE_CORTICAL_ICRP  # scripted group (container) (typed FeaturePython)
  Dunit = g/cm3
  Dvalue = 1.92
  Group = -> [H_element016,C_element016,N_element011,O_element015,Na_element003,Mg_element002,P_element003,S_element005,Ca_element004]
  conduct = 2
  density = 1
  expand = 3
  formula = G4_BONE_CORTICAL_ICRP
  name = G4_BONE_CORTICAL_ICRP
  specific = 4
FEATURE [App::DocumentObjectGroupPython] B_element001  label="B_element : 4"  # scripted group (container) (typed FeaturePython)
  n = 4
  ref = B_element
FEATURE [App::DocumentObjectGroupPython] C_element017  label="C_element : 1"  # scripted group (container) (typed FeaturePython)
  n = 1
  ref = C_element
FEATURE [App::DocumentObjectGroupPython] G4_BORON_CARBIDE  # scripted group (container) (typed FeaturePython)
  Dunit = g/cm3
  Dvalue = 2.52
  Group = -> [B_element001,C_element017]
  conduct = 2
  density = 1
  expand = 3
  formula = G4_BORON_CARBIDE
  name = G4_BORON_CARBIDE
  specific = 4
FEATURE [App::DocumentObjectGroupPython] B_element002  label="B_element : 2"  # scripted group (container) (typed FeaturePython)
  n = 2
  ref = B_element
FEATURE [App::DocumentObjectGroupPython] O_element016  label="O_element : 006"  # scripted group (container) (typed FeaturePython)
  n = 3
  ref = O_element
FEATURE [App::DocumentObjectGroupPython] G4_BORON_OXIDE  # scripted group (container) (typed FeaturePython)
  Dunit = g/cm3
  Dvalue = 1.812
  Group = -> [B_element002,O_element016]
  conduct = 2
  density = 1
  expand = 3
  formula = G4_BORON_OXIDE
  name = G4_BORON_OXIDE
  specific = 4
FEATURE [App::DocumentObjectGroupPython] H_element017  label="H_element : 0.107"  # scripted group (container) (typed FeaturePython)
  n = 0.107
FEATURE [App::DocumentObjectGroupPython] C_element018  label="C_element : 0.145"  # scripted group (container) (typed FeaturePython)
  n = 0.145
FEATURE [App::DocumentObjectGroupPython] N_element012  label="N_element : 0.022"  # scripted group (container) (typed FeaturePython)
  n = 0.022
FEATURE [App::DocumentObjectGroupPython] O_element017  label="O_element : 0.712"  # scripted group (container) (typed FeaturePython)
  n = 0.712
FEATURE [App::DocumentObjectGroupPython] Na_element004  label="Na_element : 0.004"  # scripted group (container) (typed FeaturePython)
  n = 0.002
FEATURE [App::DocumentObjectGroupPython] P_element004  label="P_element : 0.004"  # scripted group (container) (typed FeaturePython)
  n = 0.004
FEATURE [App::DocumentObjectGroupPython] S_element006  label="S_element : 0.005"  # scripted group (container) (typed FeaturePython)
  n = 0.002
FEATURE [App::DocumentObjectGroupPython] Cl_element003  label="Cl_element : 0.004"  # scripted group (container) (typed FeaturePython)
  n = 0.003
FEATURE [App::DocumentObjectGroupPython] K_element002  label="K_element : 0.003"  # scripted group (container) (typed FeaturePython)
  n = 0.003
FEATURE [App::DocumentObjectGroupPython] G4_BRAIN_ICRP  # scripted group (container) (typed FeaturePython)
  Dunit = g/cm3
  Dvalue = 1.04
  Group = -> [H_element017,C_element018,N_element012,O_element017,Na_element004,P_element004,S_element006,Cl_element003,K_element002]
  conduct = 2
  density = 1
  expand = 3
  formula = G4_BRAIN_ICRP
  name = G4_BRAIN_ICRP
  specific = 4
FEATURE [App::DocumentObjectGroupPython] C_element019  label="C_element : 4"  # scripted group (container) (typed FeaturePython)
  n = 4
  ref = C_element
FEATURE [App::DocumentObjectGroupPython] H_element018  label="H_element : 010"  # scripted group (container) (typed FeaturePython)
  n = 10
  ref = H_element
FEATURE [App::DocumentObjectGroupPython] G4_BUTANE  # scripted group (container) (typed FeaturePython)
  Dunit = g/cm3
  Dvalue = 0.00249343
  Group = -> [C_element019,H_element018]
  conduct = 2
  density = 1
  expand = 3
  formula = G4_BUTANE
  name = G4_BUTANE
  specific = 4
FEATURE [App::DocumentObjectGroupPython] C_element020  label="C_element : 008"  # scripted group (container) (typed FeaturePython)
  n = 4
  ref = C_element
FEATURE [App::DocumentObjectGroupPython] H_element019  label="H_element : 011"  # scripted group (container) (typed FeaturePython)
  n = 10
  ref = H_element
FEATURE [App::DocumentObjectGroupPython] O_element018  label="O_element : 007"  # scripted group (container) (typed FeaturePython)
  n = 1
  ref = O_element
FEATURE [App::DocumentObjectGroupPython] G4_N_BUTYL_ALCOHOL  label="G4_N-BUTYL_ALCOHOL"  # scripted group (container) (typed FeaturePython)
  Dunit = g/cm3
  Dvalue = 0.8098
  Group = -> [C_element020,H_element019,O_element018]
  conduct = 2
  density = 1
  expand = 3
  formula = G4_N-BUTYL_ALCOHOL
  name = G4_N-BUTYL_ALCOHOL
  specific = 4
FEATURE [App::DocumentObjectGroupPython] H_element020  label="H_element : 0.025"  # scripted group (container) (typed FeaturePython)
  n = 0.02468
FEATURE [App::DocumentObjectGroupPython] C_element021  label="C_element : 0.502"  # scripted group (container) (typed FeaturePython)
  n = 0.501611
FEATURE [App::DocumentObjectGroupPython] O_element019  label="O_element : 0.005"  # scripted group (container) (typed FeaturePython)
  n = 0.004527
FEATURE [App::DocumentObjectGroupPython] F_element004  label="F_element : 0.465"  # scripted group (container) (typed FeaturePython)
  n = 0.465209
FEATURE [App::DocumentObjectGroupPython] Si_element001  label="Si_element : 0.004"  # scripted group (container) (typed FeaturePython)
  n = 0.003973
FEATURE [App::DocumentObjectGroupPython] G4_C_552  label="G4_C-552"  # scripted group (container) (typed FeaturePython)
  Dunit = g/cm3
  Dvalue = 1.76
  Group = -> [H_element020,C_element021,O_element019,F_element004,Si_element001]
  conduct = 2
  density = 1
  expand = 3
  formula = G4_C-552
  name = G4_C-552
  specific = 4
FEATURE [App::DocumentObjectGroupPython] Cd_element001  label="Cd_element : 1"  # scripted group (container) (typed FeaturePython)
  n = 1
  ref = Cd_element
FEATURE [App::DocumentObjectGroupPython] Te_element001  label="Te_element : 1"  # scripted group (container) (typed FeaturePython)
  n = 1
  ref = Te_element
FEATURE [App::DocumentObjectGroupPython] G4_CADMIUM_TELLURIDE  # scripted group (container) (typed FeaturePython)
  Dunit = g/cm3
  Dvalue = 6.2
  Group = -> [Cd_element001,Te_element001]
  conduct = 2
  density = 1
  expand = 3
  formula = G4_CADMIUM_TELLURIDE
  name = G4_CADMIUM_TELLURIDE
  specific = 4
FEATURE [App::DocumentObjectGroupPython] Cd_element002  label="Cd_element : 002"  # scripted group (container) (typed FeaturePython)
  n = 1
  ref = Cd_element
FEATURE [App::DocumentObjectGroupPython] W_element001  label="W_element : 1"  # scripted group (container) (typed FeaturePython)
  n = 1
  ref = W_element
FEATURE [App::DocumentObjectGroupPython] O_element020  label="O_element : 008"  # scripted group (container) (typed FeaturePython)
  n = 4
  ref = O_element
FEATURE [App::DocumentObjectGroupPython] G4_CADMIUM_TUNGSTATE  # scripted group (container) (typed FeaturePython)
  Dunit = g/cm3
  Dvalue = 7.9
  Group = -> [Cd_element002,W_element001,O_element020]
  conduct = 2
  density = 1
  expand = 3
  formula = G4_CADMIUM_TUNGSTATE
  name = G4_CADMIUM_TUNGSTATE
  specific = 4
FEATURE [App::DocumentObjectGroupPython] Ca_element005  label="Ca_element : 1"  # scripted group (container) (typed FeaturePython)
  n = 1
  ref = Ca_element
FEATURE [App::DocumentObjectGroupPython] C_element022  label="C_element : 009"  # scripted group (container) (typed FeaturePython)
  n = 1
  ref = C_element
FEATURE [App::DocumentObjectGroupPython] O_element021  label="O_element : 009"  # scripted group (container) (typed FeaturePython)
  n = 3
  ref = O_element
FEATURE [App::DocumentObjectGroupPython] G4_CALCIUM_CARBONATE  # scripted group (container) (typed FeaturePython)
  Dunit = g/cm3
  Dvalue = 2.8
  Group = -> [Ca_element005,C_element022,O_element021]
  conduct = 2
  density = 1
  expand = 3
  formula = G4_CALCIUM_CARBONATE
  name = G4_CALCIUM_CARBONATE
  specific = 4
FEATURE [App::DocumentObjectGroupPython] Ca_element006  label="Ca_element : 002"  # scripted group (container) (typed FeaturePython)
  n = 1
  ref = Ca_element
FEATURE [App::DocumentObjectGroupPython] F_element005  label="F_element : 003"  # scripted group (container) (typed FeaturePython)
  n = 2
  ref = F_element
FEATURE [App::DocumentObjectGroupPython] G4_CALCIUM_FLUORIDE  # scripted group (container) (typed FeaturePython)
  Dunit = g/cm3
  Dvalue = 3.18
  Group = -> [Ca_element006,F_element005]
  conduct = 2
  density = 1
  expand = 3
  formula = G4_CALCIUM_FLUORIDE
  name = G4_CALCIUM_FLUORIDE
  specific = 4
FEATURE [App::DocumentObjectGroupPython] Ca_element007  label="Ca_element : 003"  # scripted group (container) (typed FeaturePython)
  n = 1
  ref = Ca_element
FEATURE [App::DocumentObjectGroupPython] O_element022  label="O_element : 010"  # scripted group (container) (typed FeaturePython)
  n = 1
  ref = O_element
FEATURE [App::DocumentObjectGroupPython] G4_CALCIUM_OXIDE  # scripted group (container) (typed FeaturePython)
  Dunit = g/cm3
  Dvalue = 3.3
  Group = -> [Ca_element007,O_element022]
  conduct = 2
  density = 1
  expand = 3
  formula = G4_CALCIUM_OXIDE
  name = G4_CALCIUM_OXIDE
  specific = 4
FEATURE [App::DocumentObjectGroupPython] Ca_element008  label="Ca_element : 004"  # scripted group (container) (typed FeaturePython)
  n = 1
  ref = Ca_element
FEATURE [App::DocumentObjectGroupPython] S_element007  label="S_element : 002"  # scripted group (container) (typed FeaturePython)
  n = 1
  ref = S_element
FEATURE [App::DocumentObjectGroupPython] O_element023  label="O_element : 011"  # scripted group (container) (typed FeaturePython)
  n = 4
  ref = O_element
FEATURE [App::DocumentObjectGroupPython] G4_CALCIUM_SULFATE  # scripted group (container) (typed FeaturePython)
  Dunit = g/cm3
  Dvalue = 2.96
  Group = -> [Ca_element008,S_element007,O_element023]
  conduct = 2
  density = 1
  expand = 3
  formula = G4_CALCIUM_SULFATE
  name = G4_CALCIUM_SULFATE
  specific = 4
FEATURE [App::DocumentObjectGroupPython] Ca_element009  label="Ca_element : 005"  # scripted group (container) (typed FeaturePython)
  n = 1
  ref = Ca_element
FEATURE [App::DocumentObjectGroupPython] W_element002  label="W_element : 002"  # scripted group (container) (typed FeaturePython)
  n = 1
  ref = W_element
FEATURE [App::DocumentObjectGroupPython] O_element024  label="O_element : 012"  # scripted group (container) (typed FeaturePython)
  n = 4
  ref = O_element
FEATURE [App::DocumentObjectGroupPython] G4_CALCIUM_TUNGSTATE  # scripted group (container) (typed FeaturePython)
  Dunit = g/cm3
  Dvalue = 6.062
  Group = -> [Ca_element009,W_element002,O_element024]
  conduct = 2
  density = 1
  expand = 3
  formula = G4_CALCIUM_TUNGSTATE
  name = G4_CALCIUM_TUNGSTATE
  specific = 4
FEATURE [App::DocumentObjectGroupPython] C_element023  label="C_element : 010"  # scripted group (container) (typed FeaturePython)
  n = 1
  ref = C_element
FEATURE [App::DocumentObjectGroupPython] O_element025  label="O_element : 013"  # scripted group (container) (typed FeaturePython)
  n = 2
  ref = O_element
FEATURE [App::DocumentObjectGroupPython] G4_CARBON_DIOXIDE  # scripted group (container) (typed FeaturePython)
  Dunit = g/cm3
  Dvalue = 0.00184212
  Group = -> [C_element023,O_element025]
  conduct = 2
  density = 1
  expand = 3
  formula = G4_CARBON_DIOXIDE
  name = G4_CARBON_DIOXIDE
  specific = 4
FEATURE [App::DocumentObjectGroupPython] C_element024  label="C_element : 011"  # scripted group (container) (typed FeaturePython)
  n = 1
  ref = C_element
FEATURE [App::DocumentObjectGroupPython] Cl_element004  label="Cl_element : 4"  # scripted group (container) (typed FeaturePython)
  n = 4
  ref = Cl_element
FEATURE [App::DocumentObjectGroupPython] G4_CARBON_TETRACHLORIDE  # scripted group (container) (typed FeaturePython)
  Dunit = g/cm3
  Dvalue = 1.594
  Group = -> [C_element024,Cl_element004]
  conduct = 2
  density = 1
  expand = 3
  formula = G4_CARBON_TETRACHLORIDE
  name = G4_CARBON_TETRACHLORIDE
  specific = 4
FEATURE [App::DocumentObjectGroupPython] C_element025  label="C_element : 012"  # scripted group (container) (typed FeaturePython)
  n = 6
  ref = C_element
FEATURE [App::DocumentObjectGroupPython] H_element021  label="H_element : 012"  # scripted group (container) (typed FeaturePython)
  n = 10
  ref = H_element
FEATURE [App::DocumentObjectGroupPython] O_element026  label="O_element : 5"  # scripted group (container) (typed FeaturePython)
  n = 5
  ref = O_element
FEATURE [App::DocumentObjectGroupPython] G4_CELLULOSE_CELLOPHANE  # scripted group (container) (typed FeaturePython)
  Dunit = g/cm3
  Dvalue = 1.42
  Group = -> [C_element025,H_element021,O_element026]
  conduct = 2
  density = 1
  expand = 3
  formula = G4_CELLULOSE_CELLOPHANE
  name = G4_CELLULOSE_CELLOPHANE
  specific = 4
FEATURE [App::DocumentObjectGroupPython] H_element022  label="H_element : 0.067"  # scripted group (container) (typed FeaturePython)
  n = 0.067125
FEATURE [App::DocumentObjectGroupPython] C_element026  label="C_element : 0.545"  # scripted group (container) (typed FeaturePython)
  n = 0.545403
FEATURE [App::DocumentObjectGroupPython] O_element027  label="O_element : 0.387"  # scripted group (container) (typed FeaturePython)
  n = 0.387472
FEATURE [App::DocumentObjectGroupPython] G4_CELLULOSE_BUTYRATE  # scripted group (container) (typed FeaturePython)
  Dunit = g/cm3
  Dvalue = 1.2
  Group = -> [H_element022,C_element026,O_element027]
  conduct = 2
  density = 1
  expand = 3
  formula = G4_CELLULOSE_BUTYRATE
  name = G4_CELLULOSE_BUTYRATE
  specific = 4
FEATURE [App::DocumentObjectGroupPython] H_element023  label="H_element : 0.029"  # scripted group (container) (typed FeaturePython)
  n = 0.029216
FEATURE [App::DocumentObjectGroupPython] C_element027  label="C_element : 0.271"  # scripted group (container) (typed FeaturePython)
  n = 0.271296
FEATURE [App::DocumentObjectGroupPython] N_element013  label="N_element : 0.121"  # scripted group (container) (typed FeaturePython)
  n = 0.121276
FEATURE [App::DocumentObjectGroupPython] O_element028  label="O_element : 0.578"  # scripted group (container) (typed FeaturePython)
  n = 0.578212
FEATURE [App::DocumentObjectGroupPython] G4_CELLULOSE_NITRATE  # scripted group (container) (typed FeaturePython)
  Dunit = g/cm3
  Dvalue = 1.49
  Group = -> [H_element023,C_element027,N_element013,O_element028]
  conduct = 2
  density = 1
  expand = 3
  formula = G4_CELLULOSE_NITRATE
  name = G4_CELLULOSE_NITRATE
  specific = 4
FEATURE [App::DocumentObjectGroupPython] H_element024  label="H_element : 0.108"  # scripted group (container) (typed FeaturePython)
  n = 0.107596
FEATURE [App::DocumentObjectGroupPython] N_element014  label="N_element : 0.001"  # scripted group (container) (typed FeaturePython)
  n = 0.0008
FEATURE [App::DocumentObjectGroupPython] O_element029  label="O_element : 0.875"  # scripted group (container) (typed FeaturePython)
  n = 0.874976
FEATURE [App::DocumentObjectGroupPython] S_element008  label="S_element : 0.015"  # scripted group (container) (typed FeaturePython)
  n = 0.014627
FEATURE [App::DocumentObjectGroupPython] Ce_element001  label="Ce_element : 0.002"  # scripted group (container) (typed FeaturePython)
  n = 0.002001
FEATURE [App::DocumentObjectGroupPython] G4_CERIC_SULFATE  # scripted group (container) (typed FeaturePython)
  Dunit = g/cm3
  Dvalue = 1.03
  Group = -> [H_element024,N_element014,O_element029,S_element008,Ce_element001]
  conduct = 2
  density = 1
  expand = 3
  formula = G4_CERIC_SULFATE
  name = G4_CERIC_SULFATE
  specific = 4
FEATURE [App::DocumentObjectGroupPython] Cs_element001  label="Cs_element : 1"  # scripted group (container) (typed FeaturePython)
  n = 1
  ref = Cs_element
FEATURE [App::DocumentObjectGroupPython] F_element006  label="F_element : 1"  # scripted group (container) (typed FeaturePython)
  n = 1
  ref = F_element
FEATURE [App::DocumentObjectGroupPython] G4_CESIUM_FLUORIDE  # scripted group (container) (typed FeaturePython)
  Dunit = g/cm3
  Dvalue = 4.115
  Group = -> [Cs_element001,F_element006]
  conduct = 2
  density = 1
  expand = 3
  formula = G4_CESIUM_FLUORIDE
  name = G4_CESIUM_FLUORIDE
  specific = 4
FEATURE [App::DocumentObjectGroupPython] Cs_element002  label="Cs_element : 002"  # scripted group (container) (typed FeaturePython)
  n = 1
  ref = Cs_element
FEATURE [App::DocumentObjectGroupPython] I_element001  label="I_element : 1"  # scripted group (container) (typed FeaturePython)
  n = 1
  ref = I_element
FEATURE [App::DocumentObjectGroupPython] G4_CESIUM_IODIDE  # scripted group (container) (typed FeaturePython)
  Dunit = g/cm3
  Dvalue = 4.51
  Group = -> [Cs_element002,I_element001]
  conduct = 2
  density = 1
  expand = 3
  formula = G4_CESIUM_IODIDE
  name = G4_CESIUM_IODIDE
  specific = 4
FEATURE [App::DocumentObjectGroupPython] C_element028  label="C_element : 013"  # scripted group (container) (typed FeaturePython)
  n = 6
  ref = C_element
FEATURE [App::DocumentObjectGroupPython] H_element025  label="H_element : 013"  # scripted group (container) (typed FeaturePython)
  n = 5
  ref = H_element
FEATURE [App::DocumentObjectGroupPython] Cl_element005  label="Cl_element : 1"  # scripted group (container) (typed FeaturePython)
  n = 1
  ref = Cl_element
FEATURE [App::DocumentObjectGroupPython] G4_CHLOROBENZENE  # scripted group (container) (typed FeaturePython)
  Dunit = g/cm3
  Dvalue = 1.1058
  Group = -> [C_element028,H_element025,Cl_element005]
  conduct = 2
  density = 1
  expand = 3
  formula = G4_CHLOROBENZENE
  name = G4_CHLOROBENZENE
  specific = 4
FEATURE [App::DocumentObjectGroupPython] C_element029  label="C_element : 014"  # scripted group (container) (typed FeaturePython)
  n = 1
  ref = C_element
FEATURE [App::DocumentObjectGroupPython] H_element026  label="H_element : 1"  # scripted group (container) (typed FeaturePython)
  n = 1
  ref = H_element
FEATURE [App::DocumentObjectGroupPython] Cl_element006  label="Cl_element : 3"  # scripted group (container) (typed FeaturePython)
  n = 3
  ref = Cl_element
FEATURE [App::DocumentObjectGroupPython] G4_CHLOROFORM  # scripted group (container) (typed FeaturePython)
  Dunit = g/cm3
  Dvalue = 1.4832
  Group = -> [C_element029,H_element026,Cl_element006]
  conduct = 2
  density = 1
  expand = 3
  formula = G4_CHLOROFORM
  name = G4_CHLOROFORM
  specific = 4
FEATURE [App::DocumentObjectGroupPython] H_element027  label="H_element : 0.010"  # scripted group (container) (typed FeaturePython)
  n = 0.01
FEATURE [App::DocumentObjectGroupPython] C_element030  label="C_element : 0.001"  # scripted group (container) (typed FeaturePython)
  n = 0.001
FEATURE [App::DocumentObjectGroupPython] O_element030  label="O_element : 0.529"  # scripted group (container) (typed FeaturePython)
  n = 0.529107
FEATURE [App::DocumentObjectGroupPython] Na_element005  label="Na_element : 0.016"  # scripted group (container) (typed FeaturePython)
  n = 0.016
FEATURE [App::DocumentObjectGroupPython] Mg_element003  label="Mg_element : 0.004"  # scripted group (container) (typed FeaturePython)
  n = 0.002
FEATURE [App::DocumentObjectGroupPython] Al_element002  label="Al_element : 0.034"  # scripted group (container) (typed FeaturePython)
  n = 0.033872
FEATURE [App::DocumentObjectGroupPython] Si_element002  label="Si_element : 0.337"  # scripted group (container) (typed FeaturePython)
  n = 0.337021
FEATURE [App::DocumentObjectGroupPython] K_element003  label="K_element : 0.013"  # scripted group (container) (typed FeaturePython)
  n = 0.013
FEATURE [App::DocumentObjectGroupPython] Ca_element010  label="Ca_element : 0.044"  # scripted group (container) (typed FeaturePython)
  n = 0.044
FEATURE [App::DocumentObjectGroupPython] Fe_element002  label="Fe_element : 0.014"  # scripted group (container) (typed FeaturePython)
  n = 0.014
FEATURE [App::DocumentObjectGroupPython] G4_CONCRETE  # scripted group (container) (typed FeaturePython)
  Dunit = g/cm3
  Dvalue = 2.3
  Group = -> [H_element027,C_element030,O_element030,Na_element005,Mg_element003,Al_element002,Si_element002,K_element003,Ca_element010,Fe_element002]
  conduct = 2
  density = 1
  expand = 3
  formula = G4_CONCRETE
  name = G4_CONCRETE
  specific = 4
FEATURE [App::DocumentObjectGroupPython] C_element031  label="C_element : 015"  # scripted group (container) (typed FeaturePython)
  n = 6
  ref = C_element
FEATURE [App::DocumentObjectGroupPython] H_element028  label="H_element : 12"  # scripted group (container) (typed FeaturePython)
  n = 12
  ref = H_element
FEATURE [App::DocumentObjectGroupPython] G4_CYCLOHEXANE  # scripted group (container) (typed FeaturePython)
  Dunit = g/cm3
  Dvalue = 0.779
  Group = -> [C_element031,H_element028]
  conduct = 2
  density = 1
  expand = 3
  formula = G4_CYCLOHEXANE
  name = G4_CYCLOHEXANE
  specific = 4
FEATURE [App::DocumentObjectGroupPython] C_element032  label="C_element : 016"  # scripted group (container) (typed FeaturePython)
  n = 6
  ref = C_element
FEATURE [App::DocumentObjectGroupPython] H_element029  label="H_element : 4"  # scripted group (container) (typed FeaturePython)
  n = 4
  ref = H_element
FEATURE [App::DocumentObjectGroupPython] Cl_element007  label="Cl_element : 2"  # scripted group (container) (typed FeaturePython)
  n = 2
  ref = Cl_element
FEATURE [App::DocumentObjectGroupPython] G4_1_2_DICHLOROBENZENE  label="G4_1.2-DICHLOROBENZENE"  # scripted group (container) (typed FeaturePython)
  Dunit = g/cm3
  Dvalue = 1.3048
  Group = -> [C_element032,H_element029,Cl_element007]
  conduct = 2
  density = 1
  expand = 3
  formula = G4_1.2-DICHLOROBENZENE
  name = G4_1.2-DICHLOROBENZENE
  specific = 4
FEATURE [App::DocumentObjectGroupPython] C_element033  label="C_element : 017"  # scripted group (container) (typed FeaturePython)
  n = 4
  ref = C_element
FEATURE [App::DocumentObjectGroupPython] H_element030  label="H_element : 8"  # scripted group (container) (typed FeaturePython)
  n = 8
  ref = H_element
FEATURE [App::DocumentObjectGroupPython] O_element031  label="O_element : 014"  # scripted group (container) (typed FeaturePython)
  n = 1
  ref = O_element
FEATURE [App::DocumentObjectGroupPython] Cl_element008  label="Cl_element : 005"  # scripted group (container) (typed FeaturePython)
  n = 2
  ref = Cl_element
FEATURE [App::DocumentObjectGroupPython] G4_DICHLORODIETHYL_ETHER  # scripted group (container) (typed FeaturePython)
  Dunit = g/cm3
  Dvalue = 1.2199
  Group = -> [C_element033,H_element030,O_element031,Cl_element008]
  conduct = 2
  density = 1
  expand = 3
  formula = G4_DICHLORODIETHYL_ETHER
  name = G4_DICHLORODIETHYL_ETHER
  specific = 4
FEATURE [App::DocumentObjectGroupPython] C_element034  label="C_element : 018"  # scripted group (container) (typed FeaturePython)
  n = 2
  ref = C_element
FEATURE [App::DocumentObjectGroupPython] H_element031  label="H_element : 014"  # scripted group (container) (typed FeaturePython)
  n = 4
  ref = H_element
FEATURE [App::DocumentObjectGroupPython] Cl_element009  label="Cl_element : 006"  # scripted group (container) (typed FeaturePython)
  n = 2
  ref = Cl_element
FEATURE [App::DocumentObjectGroupPython] G4_1_2_DICHLOROETHANE  label="G4_1.2-DICHLOROETHANE"  # scripted group (container) (typed FeaturePython)
  Dunit = g/cm3
  Dvalue = 1.2351
  Group = -> [C_element034,H_element031,Cl_element009]
  conduct = 2
  density = 1
  expand = 3
  formula = G4_1.2-DICHLOROETHANE
  name = G4_1.2-DICHLOROETHANE
  specific = 4
FEATURE [App::DocumentObjectGroupPython] C_element035  label="C_element : 019"  # scripted group (container) (typed FeaturePython)
  n = 4
  ref = C_element
FEATURE [App::DocumentObjectGroupPython] H_element032  label="H_element : 015"  # scripted group (container) (typed FeaturePython)
  n = 10
  ref = H_element
FEATURE [App::DocumentObjectGroupPython] O_element032  label="O_element : 015"  # scripted group (container) (typed FeaturePython)
  n = 1
  ref = O_element
FEATURE [App::DocumentObjectGroupPython] G4_DIETHYL_ETHER  # scripted group (container) (typed FeaturePython)
  Dunit = g/cm3
  Dvalue = 0.71378
  Group = -> [C_element035,H_element032,O_element032]
  conduct = 2
  density = 1
  expand = 3
  formula = G4_DIETHYL_ETHER
  name = G4_DIETHYL_ETHER
  specific = 4
FEATURE [App::DocumentObjectGroupPython] C_element036  label="C_element : 020"  # scripted group (container) (typed FeaturePython)
  n = 3
  ref = C_element
FEATURE [App::DocumentObjectGroupPython] H_element033  label="H_element : 016"  # scripted group (container) (typed FeaturePython)
  n = 7
  ref = H_element
FEATURE [App::DocumentObjectGroupPython] N_element015  label="N_element : 008"  # scripted group (container) (typed FeaturePython)
  n = 1
  ref = N_element
FEATURE [App::DocumentObjectGroupPython] O_element033  label="O_element : 016"  # scripted group (container) (typed FeaturePython)
  n = 1
  ref = O_element
FEATURE [App::DocumentObjectGroupPython] G4_N_N_DIMETHYL_FORMAMIDE  label="G4_N.N-DIMETHYL_FORMAMIDE"  # scripted group (container) (typed FeaturePython)
  Dunit = g/cm3
  Dvalue = 0.9487
  Group = -> [C_element036,H_element033,N_element015,O_element033]
  conduct = 2
  density = 1
  expand = 3
  formula = G4_N.N-DIMETHYL_FORMAMIDE
  name = G4_N.N-DIMETHYL_FORMAMIDE
  specific = 4
FEATURE [App::DocumentObjectGroupPython] C_element037  label="C_element : 021"  # scripted group (container) (typed FeaturePython)
  n = 2
  ref = C_element
FEATURE [App::DocumentObjectGroupPython] H_element034  label="H_element : 017"  # scripted group (container) (typed FeaturePython)
  n = 6
  ref = H_element
FEATURE [App::DocumentObjectGroupPython] O_element034  label="O_element : 017"  # scripted group (container) (typed FeaturePython)
  n = 1
  ref = O_element
FEATURE [App::DocumentObjectGroupPython] S_element009  label="S_element : 003"  # scripted group (container) (typed FeaturePython)
  n = 1
  ref = S_element
FEATURE [App::DocumentObjectGroupPython] G4_DIMETHYL_SULFOXIDE  # scripted group (container) (typed FeaturePython)
  Dunit = g/cm3
  Dvalue = 1.1014
  Group = -> [C_element037,H_element034,O_element034,S_element009]
  conduct = 2
  density = 1
  expand = 3
  formula = G4_DIMETHYL_SULFOXIDE
  name = G4_DIMETHYL_SULFOXIDE
  specific = 4
FEATURE [App::DocumentObjectGroupPython] C_element038  label="C_element : 022"  # scripted group (container) (typed FeaturePython)
  n = 2
  ref = C_element
FEATURE [App::DocumentObjectGroupPython] H_element035  label="H_element : 018"  # scripted group (container) (typed FeaturePython)
  n = 6
  ref = H_element
FEATURE [App::DocumentObjectGroupPython] G4_ETHANE  # scripted group (container) (typed FeaturePython)
  Dunit = g/cm3
  Dvalue = 0.00125324
  Group = -> [C_element038,H_element035]
  conduct = 2
  density = 1
  expand = 3
  formula = G4_ETHANE
  name = G4_ETHANE
  specific = 4
FEATURE [App::DocumentObjectGroupPython] C_element039  label="C_element : 023"  # scripted group (container) (typed FeaturePython)
  n = 2
  ref = C_element
FEATURE [App::DocumentObjectGroupPython] H_element036  label="H_element : 019"  # scripted group (container) (typed FeaturePython)
  n = 6
  ref = H_element
FEATURE [App::DocumentObjectGroupPython] O_element035  label="O_element : 018"  # scripted group (container) (typed FeaturePython)
  n = 1
  ref = O_element
FEATURE [App::DocumentObjectGroupPython] G4_ETHYL_ALCOHOL  # scripted group (container) (typed FeaturePython)
  Dunit = g/cm3
  Dvalue = 0.7893
  Group = -> [C_element039,H_element036,O_element035]
  conduct = 2
  density = 1
  expand = 3
  formula = G4_ETHYL_ALCOHOL
  name = G4_ETHYL_ALCOHOL
  specific = 4
FEATURE [App::DocumentObjectGroupPython] H_element037  label="H_element : 0.090"  # scripted group (container) (typed FeaturePython)
  n = 0.090027
FEATURE [App::DocumentObjectGroupPython] C_element040  label="C_element : 0.585"  # scripted group (container) (typed FeaturePython)
  n = 0.585182
FEATURE [App::DocumentObjectGroupPython] O_element036  label="O_element : 0.325"  # scripted group (container) (typed FeaturePython)
  n = 0.324791
FEATURE [App::DocumentObjectGroupPython] G4_ETHYL_CELLULOSE  # scripted group (container) (typed FeaturePython)
  Dunit = g/cm3
  Dvalue = 1.13
  Group = -> [H_element037,C_element040,O_element036]
  conduct = 2
  density = 1
  expand = 3
  formula = G4_ETHYL_CELLULOSE
  name = G4_ETHYL_CELLULOSE
  specific = 4
FEATURE [App::DocumentObjectGroupPython] C_element041  label="C_element : 024"  # scripted group (container) (typed FeaturePython)
  n = 2
  ref = C_element
FEATURE [App::DocumentObjectGroupPython] H_element038  label="H_element : 020"  # scripted group (container) (typed FeaturePython)
  n = 4
  ref = H_element
FEATURE [App::DocumentObjectGroupPython] G4_ETHYLENE  # scripted group (container) (typed FeaturePython)
  Dunit = g/cm3
  Dvalue = 0.00117497
  Group = -> [C_element041,H_element038]
  conduct = 2
  density = 1
  expand = 3
  formula = G4_ETHYLENE
  name = G4_ETHYLENE
  specific = 4
FEATURE [App::DocumentObjectGroupPython] H_element039  label="H_element : 0.096"  # scripted group (container) (typed FeaturePython)
  n = 0.096
FEATURE [App::DocumentObjectGroupPython] C_element042  label="C_element : 0.195"  # scripted group (container) (typed FeaturePython)
  n = 0.195
FEATURE [App::DocumentObjectGroupPython] N_element016  label="N_element : 0.057"  # scripted group (container) (typed FeaturePython)
  n = 0.057
FEATURE [App::DocumentObjectGroupPython] O_element037  label="O_element : 0.646"  # scripted group (container) (typed FeaturePython)
  n = 0.646
FEATURE [App::DocumentObjectGroupPython] Na_element006  label="Na_element : 0.017"  # scripted group (container) (typed FeaturePython)
  n = 0.001
FEATURE [App::DocumentObjectGroupPython] P_element005  label="P_element : 0.104"  # scripted group (container) (typed FeaturePython)
  n = 0.001
FEATURE [App::DocumentObjectGroupPython] S_element010  label="S_element : 0.016"  # scripted group (container) (typed FeaturePython)
  n = 0.003
FEATURE [App::DocumentObjectGroupPython] Cl_element010  label="Cl_element : 0.005"  # scripted group (container) (typed FeaturePython)
  n = 0.001
FEATURE [App::DocumentObjectGroupPython] G4_EYE_LENS_ICRP  # scripted group (container) (typed FeaturePython)
  Dunit = g/cm3
  Dvalue = 1.07
  Group = -> [H_element039,C_element042,N_element016,O_element037,Na_element006,P_element005,S_element010,Cl_element010]
  conduct = 2
  density = 1
  expand = 3
  formula = G4_EYE_LENS_ICRP
  name = G4_EYE_LENS_ICRP
  specific = 4
FEATURE [App::DocumentObjectGroupPython] Fe_element003  label="Fe_element : 2"  # scripted group (container) (typed FeaturePython)
  n = 2
  ref = Fe_element
FEATURE [App::DocumentObjectGroupPython] O_element038  label="O_element : 019"  # scripted group (container) (typed FeaturePython)
  n = 3
  ref = O_element
FEATURE [App::DocumentObjectGroupPython] G4_FERRIC_OXIDE  # scripted group (container) (typed FeaturePython)
  Dunit = g/cm3
  Dvalue = 5.2
  Group = -> [Fe_element003,O_element038]
  conduct = 2
  density = 1
  expand = 3
  formula = G4_FERRIC_OXIDE
  name = G4_FERRIC_OXIDE
  specific = 4
FEATURE [App::DocumentObjectGroupPython] Fe_element004  label="Fe_element : 1"  # scripted group (container) (typed FeaturePython)
  n = 1
  ref = Fe_element
FEATURE [App::DocumentObjectGroupPython] B_element003  label="B_element : 1"  # scripted group (container) (typed FeaturePython)
  n = 1
  ref = B_element
FEATURE [App::DocumentObjectGroupPython] G4_FERROBORIDE  # scripted group (container) (typed FeaturePython)
  Dunit = g/cm3
  Dvalue = 7.15
  Group = -> [Fe_element004,B_element003]
  conduct = 2
  density = 1
  expand = 3
  formula = G4_FERROBORIDE
  name = G4_FERROBORIDE
  specific = 4
FEATURE [App::DocumentObjectGroupPython] Fe_element005  label="Fe_element : 003"  # scripted group (container) (typed FeaturePython)
  n = 1
  ref = Fe_element
FEATURE [App::DocumentObjectGroupPython] O_element039  label="O_element : 020"  # scripted group (container) (typed FeaturePython)
  n = 1
  ref = O_element
FEATURE [App::DocumentObjectGroupPython] G4_FERROUS_OXIDE  # scripted group (container) (typed FeaturePython)
  Dunit = g/cm3
  Dvalue = 5.7
  Group = -> [Fe_element005,O_element039]
  conduct = 2
  density = 1
  expand = 3
  formula = G4_FERROUS_OXIDE
  name = G4_FERROUS_OXIDE
  specific = 4
FEATURE [App::DocumentObjectGroupPython] H_element040  label="H_element : 0.115"  # scripted group (container) (typed FeaturePython)
  n = 0.108259
FEATURE [App::DocumentObjectGroupPython] N_element017  label="N_element : 0.000"  # scripted group (container) (typed FeaturePython)
  n = 2.7e-05
FEATURE [App::DocumentObjectGroupPython] O_element040  label="O_element : 0.879"  # scripted group (container) (typed FeaturePython)
  n = 0.878636
FEATURE [App::DocumentObjectGroupPython] Na_element007  label="Na_element : 0.000"  # scripted group (container) (typed FeaturePython)
  n = 2.2e-05
FEATURE [App::DocumentObjectGroupPython] S_element011  label="S_element : 0.013"  # scripted group (container) (typed FeaturePython)
  n = 0.012968
FEATURE [App::DocumentObjectGroupPython] Cl_element011  label="Cl_element : 0.000"  # scripted group (container) (typed FeaturePython)
  n = 3.4e-05
FEATURE [App::DocumentObjectGroupPython] Fe_element006  label="Fe_element : 0.000"  # scripted group (container) (typed FeaturePython)
  n = 5.4e-05
FEATURE [App::DocumentObjectGroupPython] G4_FERROUS_SULFATE  # scripted group (container) (typed FeaturePython)
  Dunit = g/cm3
  Dvalue = 1.024
  Group = -> [H_element040,N_element017,O_element040,Na_element007,S_element011,Cl_element011,Fe_element006]
  conduct = 2
  density = 1
  expand = 3
  formula = G4_FERROUS_SULFATE
  name = G4_FERROUS_SULFATE
  specific = 4
FEATURE [App::DocumentObjectGroupPython] C_element043  label="C_element : 0.099"  # scripted group (container) (typed FeaturePython)
  n = 0.099335
FEATURE [App::DocumentObjectGroupPython] F_element007  label="F_element : 0.314"  # scripted group (container) (typed FeaturePython)
  n = 0.314247
FEATURE [App::DocumentObjectGroupPython] Cl_element012  label="Cl_element : 0.586"  # scripted group (container) (typed FeaturePython)
  n = 0.586418
FEATURE [App::DocumentObjectGroupPython] G4_FREON_12  label="G4_FREON-12"  # scripted group (container) (typed FeaturePython)
  Dunit = g/cm3
  Dvalue = 1.12
  Group = -> [C_element043,F_element007,Cl_element012]
  conduct = 2
  density = 1
  expand = 3
  formula = G4_FREON-12
  name = G4_FREON-12
  specific = 4
FEATURE [App::DocumentObjectGroupPython] C_element044  label="C_element : 0.057"  # scripted group (container) (typed FeaturePython)
  n = 0.057245
FEATURE [App::DocumentObjectGroupPython] F_element008  label="F_element : 0.181"  # scripted group (container) (typed FeaturePython)
  n = 0.181096
FEATURE [App::DocumentObjectGroupPython] Br_element001  label="Br_element : 0.762"  # scripted group (container) (typed FeaturePython)
  n = 0.761659
FEATURE [App::DocumentObjectGroupPython] G4_FREON_12B2  label="G4_FREON-12B2"  # scripted group (container) (typed FeaturePython)
  Dunit = g/cm3
  Dvalue = 1.8
  Group = -> [C_element044,F_element008,Br_element001]
  conduct = 2
  density = 1
  expand = 3
  formula = G4_FREON-12B2
  name = G4_FREON-12B2
  specific = 4
FEATURE [App::DocumentObjectGroupPython] C_element045  label="C_element : 0.115"  # scripted group (container) (typed FeaturePython)
  n = 0.114983
FEATURE [App::DocumentObjectGroupPython] F_element009  label="F_element : 0.546"  # scripted group (container) (typed FeaturePython)
  n = 0.545621
FEATURE [App::DocumentObjectGroupPython] Cl_element013  label="Cl_element : 0.339"  # scripted group (container) (typed FeaturePython)
  n = 0.339396
FEATURE [App::DocumentObjectGroupPython] G4_FREON_13  label="G4_FREON-13"  # scripted group (container) (typed FeaturePython)
  Dunit = g/cm3
  Dvalue = 0.95
  Group = -> [C_element045,F_element009,Cl_element013]
  conduct = 2
  density = 1
  expand = 3
  formula = G4_FREON-13
  name = G4_FREON-13
  specific = 4
FEATURE [App::DocumentObjectGroupPython] C_element046  label="C_element : 025"  # scripted group (container) (typed FeaturePython)
  n = 1
  ref = C_element
FEATURE [App::DocumentObjectGroupPython] F_element010  label="F_element : 3"  # scripted group (container) (typed FeaturePython)
  n = 3
  ref = F_element
FEATURE [App::DocumentObjectGroupPython] Br_element002  label="Br_element : 1"  # scripted group (container) (typed FeaturePython)
  n = 1
  ref = Br_element
FEATURE [App::DocumentObjectGroupPython] G4_FREON_13B1  label="G4_FREON-13B1"  # scripted group (container) (typed FeaturePython)
  Dunit = g/cm3
  Dvalue = 1.5
  Group = -> [C_element046,F_element010,Br_element002]
  conduct = 2
  density = 1
  expand = 3
  formula = G4_FREON-13B1
  name = G4_FREON-13B1
  specific = 4
FEATURE [App::DocumentObjectGroupPython] C_element047  label="C_element : 0.061"  # scripted group (container) (typed FeaturePython)
  n = 0.061309
FEATURE [App::DocumentObjectGroupPython] F_element011  label="F_element : 0.291"  # scripted group (container) (typed FeaturePython)
  n = 0.290924
FEATURE [App::DocumentObjectGroupPython] I_element002  label="I_element : 0.648"  # scripted group (container) (typed FeaturePython)
  n = 0.647767
FEATURE [App::DocumentObjectGroupPython] G4_FREON_13I1  label="G4_FREON-13I1"  # scripted group (container) (typed FeaturePython)
  Dunit = g/cm3
  Dvalue = 1.8
  Group = -> [C_element047,F_element011,I_element002]
  conduct = 2
  density = 1
  expand = 3
  formula = G4_FREON-13I1
  name = G4_FREON-13I1
  specific = 4
FEATURE [App::DocumentObjectGroupPython] Gd_element001  label="Gd_element : 2"  # scripted group (container) (typed FeaturePython)
  n = 2
  ref = Gd_element
FEATURE [App::DocumentObjectGroupPython] O_element041  label="O_element : 021"  # scripted group (container) (typed FeaturePython)
  n = 2
  ref = O_element
FEATURE [App::DocumentObjectGroupPython] S_element012  label="S_element : 004"  # scripted group (container) (typed FeaturePython)
  n = 1
  ref = S_element
FEATURE [App::DocumentObjectGroupPython] G4_GADOLINIUM_OXYSULFIDE  # scripted group (container) (typed FeaturePython)
  Dunit = g/cm3
  Dvalue = 7.44
  Group = -> [Gd_element001,O_element041,S_element012]
  conduct = 2
  density = 1
  expand = 3
  formula = G4_GADOLINIUM_OXYSULFIDE
  name = G4_GADOLINIUM_OXYSULFIDE
  specific = 4
FEATURE [App::DocumentObjectGroupPython] Ga_element001  label="Ga_element : 1"  # scripted group (container) (typed FeaturePython)
  n = 1
  ref = Ga_element
FEATURE [App::DocumentObjectGroupPython] As_element001  label="As_element : 1"  # scripted group (container) (typed FeaturePython)
  n = 1
  ref = As_element
FEATURE [App::DocumentObjectGroupPython] G4_GALLIUM_ARSENIDE  # scripted group (container) (typed FeaturePython)
  Dunit = g/cm3
  Dvalue = 5.31
  Group = -> [Ga_element001,As_element001]
  conduct = 2
  density = 1
  expand = 3
  formula = G4_GALLIUM_ARSENIDE
  name = G4_GALLIUM_ARSENIDE
  specific = 4
FEATURE [App::DocumentObjectGroupPython] H_element041  label="H_element : 0.081"  # scripted group (container) (typed FeaturePython)
  n = 0.08118
FEATURE [App::DocumentObjectGroupPython] C_element048  label="C_element : 0.416"  # scripted group (container) (typed FeaturePython)
  n = 0.41606
FEATURE [App::DocumentObjectGroupPython] N_element018  label="N_element : 0.111"  # scripted group (container) (typed FeaturePython)
  n = 0.11124
FEATURE [App::DocumentObjectGroupPython] O_element042  label="O_element : 0.381"  # scripted group (container) (typed FeaturePython)
  n = 0.38064
FEATURE [App::DocumentObjectGroupPython] S_element013  label="S_element : 0.011"  # scripted group (container) (typed FeaturePython)
  n = 0.01088
FEATURE [App::DocumentObjectGroupPython] G4_GEL_PHOTO_EMULSION  # scripted group (container) (typed FeaturePython)
  Dunit = g/cm3
  Dvalue = 1.2914
  Group = -> [H_element041,C_element048,N_element018,O_element042,S_element013]
  conduct = 2
  density = 1
  expand = 3
  formula = G4_GEL_PHOTO_EMULSION
  name = G4_GEL_PHOTO_EMULSION
  specific = 4
FEATURE [App::DocumentObjectGroupPython] B_element004  label="B_element : 0.040"  # scripted group (container) (typed FeaturePython)
  n = 0.0400639
FEATURE [App::DocumentObjectGroupPython] O_element043  label="O_element : 0.540"  # scripted group (container) (typed FeaturePython)
  n = 0.539561
FEATURE [App::DocumentObjectGroupPython] Na_element008  label="Na_element : 0.028"  # scripted group (container) (typed FeaturePython)
  n = 0.0281909
FEATURE [App::DocumentObjectGroupPython] Al_element003  label="Al_element : 0.012"  # scripted group (container) (typed FeaturePython)
  n = 0.011644
FEATURE [App::DocumentObjectGroupPython] Si_element003  label="Si_element : 0.377"  # scripted group (container) (typed FeaturePython)
  n = 0.377219
FEATURE [App::DocumentObjectGroupPython] K_element004  label="K_element : 0.014"  # scripted group (container) (typed FeaturePython)
  n = 0.00332099
FEATURE [App::DocumentObjectGroupPython] G4_Pyrex_Glass  # scripted group (container) (typed FeaturePython)
  Dunit = g/cm3
  Dvalue = 2.23
  Group = -> [B_element004,O_element043,Na_element008,Al_element003,Si_element003,K_element004]
  conduct = 2
  density = 1
  expand = 3
  formula = G4_Pyrex_Glass
  name = G4_Pyrex_Glass
  specific = 4
FEATURE [App::DocumentObjectGroupPython] O_element044  label="O_element : 0.156"  # scripted group (container) (typed FeaturePython)
  n = 0.156453
FEATURE [App::DocumentObjectGroupPython] Si_element004  label="Si_element : 0.081"  # scripted group (container) (typed FeaturePython)
  n = 0.080866
FEATURE [App::DocumentObjectGroupPython] Ti_element001  label="Ti_element : 0.008"  # scripted group (container) (typed FeaturePython)
  n = 0.008092
FEATURE [App::DocumentObjectGroupPython] As_element002  label="As_element : 0.003"  # scripted group (container) (typed FeaturePython)
  n = 0.002651
FEATURE [App::DocumentObjectGroupPython] Pb_element001  label="Pb_element : 0.752"  # scripted group (container) (typed FeaturePython)
  n = 0.751938
FEATURE [App::DocumentObjectGroupPython] G4_GLASS_LEAD  # scripted group (container) (typed FeaturePython)
  Dunit = g/cm3
  Dvalue = 6.22
  Group = -> [O_element044,Si_element004,Ti_element001,As_element002,Pb_element001]
  conduct = 2
  density = 1
  expand = 3
  formula = G4_GLASS_LEAD
  name = G4_GLASS_LEAD
  specific = 4
FEATURE [App::DocumentObjectGroupPython] O_element045  label="O_element : 0.460"  # scripted group (container) (typed FeaturePython)
  n = 0.4598
FEATURE [App::DocumentObjectGroupPython] Na_element009  label="Na_element : 0.096"  # scripted group (container) (typed FeaturePython)
  n = 0.0964411
FEATURE [App::DocumentObjectGroupPython] Si_element005  label="Si_element : 0.378"  # scripted group (container) (typed FeaturePython)
  n = 0.336553
FEATURE [App::DocumentObjectGroupPython] Ca_element011  label="Ca_element : 0.107"  # scripted group (container) (typed FeaturePython)
  n = 0.107205
FEATURE [App::DocumentObjectGroupPython] G4_GLASS_PLATE  # scripted group (container) (typed FeaturePython)
  Dunit = g/cm3
  Dvalue = 2.4
  Group = -> [O_element045,Na_element009,Si_element005,Ca_element011]
  conduct = 2
  density = 1
  expand = 3
  formula = G4_GLASS_PLATE
  name = G4_GLASS_PLATE
  specific = 4
FEATURE [App::DocumentObjectGroupPython] C_element049  label="C_element : 026"  # scripted group (container) (typed FeaturePython)
  n = 5
  ref = C_element
FEATURE [App::DocumentObjectGroupPython] H_element042  label="H_element : 021"  # scripted group (container) (typed FeaturePython)
  n = 10
  ref = H_element
FEATURE [App::DocumentObjectGroupPython] N_element019  label="N_element : 2"  # scripted group (container) (typed FeaturePython)
  n = 2
  ref = N_element
FEATURE [App::DocumentObjectGroupPython] O_element046  label="O_element : 022"  # scripted group (container) (typed FeaturePython)
  n = 3
  ref = O_element
FEATURE [App::DocumentObjectGroupPython] G4_GLUTAMINE  # scripted group (container) (typed FeaturePython)
  Dunit = g/cm3
  Dvalue = 1.46
  Group = -> [C_element049,H_element042,N_element019,O_element046]
  conduct = 2
  density = 1
  expand = 3
  formula = G4_GLUTAMINE
  name = G4_GLUTAMINE
  specific = 4
FEATURE [App::DocumentObjectGroupPython] C_element050  label="C_element : 027"  # scripted group (container) (typed FeaturePython)
  n = 3
  ref = C_element
FEATURE [App::DocumentObjectGroupPython] H_element043  label="H_element : 022"  # scripted group (container) (typed FeaturePython)
  n = 8
  ref = H_element
FEATURE [App::DocumentObjectGroupPython] O_element047  label="O_element : 023"  # scripted group (container) (typed FeaturePython)
  n = 3
  ref = O_element
FEATURE [App::DocumentObjectGroupPython] G4_GLYCEROL  # scripted group (container) (typed FeaturePython)
  Dunit = g/cm3
  Dvalue = 1.2613
  Group = -> [C_element050,H_element043,O_element047]
  conduct = 2
  density = 1
  expand = 3
  formula = G4_GLYCEROL
  name = G4_GLYCEROL
  specific = 4
FEATURE [App::DocumentObjectGroupPython] C_element051  label="C_element : 028"  # scripted group (container) (typed FeaturePython)
  n = 5
  ref = C_element
FEATURE [App::DocumentObjectGroupPython] H_element044  label="H_element : 023"  # scripted group (container) (typed FeaturePython)
  n = 5
  ref = H_element
FEATURE [App::DocumentObjectGroupPython] N_element020  label="N_element : 009"  # scripted group (container) (typed FeaturePython)
  n = 5
  ref = N_element
FEATURE [App::DocumentObjectGroupPython] O_element048  label="O_element : 024"  # scripted group (container) (typed FeaturePython)
  n = 1
  ref = O_element
FEATURE [App::DocumentObjectGroupPython] G4_GUANINE  # scripted group (container) (typed FeaturePython)
  Dunit = g/cm3
  Dvalue = 2.2
  Group = -> [C_element051,H_element044,N_element020,O_element048]
  conduct = 2
  density = 1
  expand = 3
  formula = G4_GUANINE
  name = G4_GUANINE
  specific = 4
FEATURE [App::DocumentObjectGroupPython] Ca_element012  label="Ca_element : 006"  # scripted group (container) (typed FeaturePython)
  n = 1
  ref = Ca_element
FEATURE [App::DocumentObjectGroupPython] S_element014  label="S_element : 005"  # scripted group (container) (typed FeaturePython)
  n = 1
  ref = S_element
FEATURE [App::DocumentObjectGroupPython] O_element049  label="O_element : 6"  # scripted group (container) (typed FeaturePython)
  n = 6
  ref = O_element
FEATURE [App::DocumentObjectGroupPython] H_element045  label="H_element : 024"  # scripted group (container) (typed FeaturePython)
  n = 4
  ref = H_element
FEATURE [App::DocumentObjectGroupPython] G4_GYPSUM  # scripted group (container) (typed FeaturePython)
  Dunit = g/cm3
  Dvalue = 2.32
  Group = -> [Ca_element012,S_element014,O_element049,H_element045]
  conduct = 2
  density = 1
  expand = 3
  formula = G4_GYPSUM
  name = G4_GYPSUM
  specific = 4
FEATURE [App::DocumentObjectGroupPython] C_element052  label="C_element : 7"  # scripted group (container) (typed FeaturePython)
  n = 7
  ref = C_element
FEATURE [App::DocumentObjectGroupPython] H_element046  label="H_element : 16"  # scripted group (container) (typed FeaturePython)
  n = 16
  ref = H_element
FEATURE [App::DocumentObjectGroupPython] G4_N_HEPTANE  label="G4_N-HEPTANE"  # scripted group (container) (typed FeaturePython)
  Dunit = g/cm3
  Dvalue = 0.68376
  Group = -> [C_element052,H_element046]
  conduct = 2
  density = 1
  expand = 3
  formula = G4_N-HEPTANE
  name = G4_N-HEPTANE
  specific = 4
FEATURE [App::DocumentObjectGroupPython] C_element053  label="C_element : 029"  # scripted group (container) (typed FeaturePython)
  n = 6
  ref = C_element
FEATURE [App::DocumentObjectGroupPython] H_element047  label="H_element : 14"  # scripted group (container) (typed FeaturePython)
  n = 14
  ref = H_element
FEATURE [App::DocumentObjectGroupPython] G4_N_HEXANE  label="G4_N-HEXANE"  # scripted group (container) (typed FeaturePython)
  Dunit = g/cm3
  Dvalue = 0.6603
  Group = -> [C_element053,H_element047]
  conduct = 2
  density = 1
  expand = 3
  formula = G4_N-HEXANE
  name = G4_N-HEXANE
  specific = 4
FEATURE [App::DocumentObjectGroupPython] C_element054  label="C_element : 22"  # scripted group (container) (typed FeaturePython)
  n = 22
  ref = C_element
FEATURE [App::DocumentObjectGroupPython] H_element048  label="H_element : 025"  # scripted group (container) (typed FeaturePython)
  n = 10
  ref = H_element
FEATURE [App::DocumentObjectGroupPython] N_element021  label="N_element : 010"  # scripted group (container) (typed FeaturePython)
  n = 2
  ref = N_element
FEATURE [App::DocumentObjectGroupPython] O_element050  label="O_element : 025"  # scripted group (container) (typed FeaturePython)
  n = 5
  ref = O_element
FEATURE [App::DocumentObjectGroupPython] G4_KAPTON  # scripted group (container) (typed FeaturePython)
  Dunit = g/cm3
  Dvalue = 1.42
  Group = -> [C_element054,H_element048,N_element021,O_element050]
  conduct = 2
  density = 1
  expand = 3
  formula = G4_KAPTON
  name = G4_KAPTON
  specific = 4
FEATURE [App::DocumentObjectGroupPython] La_element001  label="La_element : 1"  # scripted group (container) (typed FeaturePython)
  n = 1
  ref = La_element
FEATURE [App::DocumentObjectGroupPython] Br_element003  label="Br_element : 002"  # scripted group (container) (typed FeaturePython)
  n = 1
  ref = Br_element
FEATURE [App::DocumentObjectGroupPython] O_element051  label="O_element : 026"  # scripted group (container) (typed FeaturePython)
  n = 1
  ref = O_element
FEATURE [App::DocumentObjectGroupPython] G4_LANTHANUM_OXYBROMIDE  # scripted group (container) (typed FeaturePython)
  Dunit = g/cm3
  Dvalue = 6.28
  Group = -> [La_element001,Br_element003,O_element051]
  conduct = 2
  density = 1
  expand = 3
  formula = G4_LANTHANUM_OXYBROMIDE
  name = G4_LANTHANUM_OXYBROMIDE
  specific = 4
FEATURE [App::DocumentObjectGroupPython] La_element002  label="La_element : 2"  # scripted group (container) (typed FeaturePython)
  n = 2
  ref = La_element
FEATURE [App::DocumentObjectGroupPython] O_element052  label="O_element : 027"  # scripted group (container) (typed FeaturePython)
  n = 2
  ref = O_element
FEATURE [App::DocumentObjectGroupPython] S_element015  label="S_element : 006"  # scripted group (container) (typed FeaturePython)
  n = 1
  ref = S_element
FEATURE [App::DocumentObjectGroupPython] G4_LANTHANUM_OXYSULFIDE  # scripted group (container) (typed FeaturePython)
  Dunit = g/cm3
  Dvalue = 5.86
  Group = -> [La_element002,O_element052,S_element015]
  conduct = 2
  density = 1
  expand = 3
  formula = G4_LANTHANUM_OXYSULFIDE
  name = G4_LANTHANUM_OXYSULFIDE
  specific = 4
FEATURE [App::DocumentObjectGroupPython] O_element053  label="O_element : 0.072"  # scripted group (container) (typed FeaturePython)
  n = 0.071682
FEATURE [App::DocumentObjectGroupPython] Pb_element002  label="Pb_element : 0.928"  # scripted group (container) (typed FeaturePython)
  n = 0.928318
FEATURE [App::DocumentObjectGroupPython] G4_LEAD_OXIDE  # scripted group (container) (typed FeaturePython)
  Dunit = g/cm3
  Dvalue = 9.53
  Group = -> [O_element053,Pb_element002]
  conduct = 2
  density = 1
  expand = 3
  formula = G4_LEAD_OXIDE
  name = G4_LEAD_OXIDE
  specific = 4
FEATURE [App::DocumentObjectGroupPython] Li_element001  label="Li_element : 1"  # scripted group (container) (typed FeaturePython)
  n = 1
  ref = Li_element
FEATURE [App::DocumentObjectGroupPython] N_element022  label="N_element : 011"  # scripted group (container) (typed FeaturePython)
  n = 1
  ref = N_element
FEATURE [App::DocumentObjectGroupPython] H_element049  label="H_element : 026"  # scripted group (container) (typed FeaturePython)
  n = 2
  ref = H_element
FEATURE [App::DocumentObjectGroupPython] G4_LITHIUM_AMIDE  # scripted group (container) (typed FeaturePython)
  Dunit = g/cm3
  Dvalue = 1.178
  Group = -> [Li_element001,N_element022,H_element049]
  conduct = 2
  density = 1
  expand = 3
  formula = G4_LITHIUM_AMIDE
  name = G4_LITHIUM_AMIDE
  specific = 4
FEATURE [App::DocumentObjectGroupPython] Li_element002  label="Li_element : 2"  # scripted group (container) (typed FeaturePython)
  n = 2
  ref = Li_element
FEATURE [App::DocumentObjectGroupPython] C_element055  label="C_element : 030"  # scripted group (container) (typed FeaturePython)
  n = 1
  ref = C_element
FEATURE [App::DocumentObjectGroupPython] O_element054  label="O_element : 028"  # scripted group (container) (typed FeaturePython)
  n = 3
  ref = O_element
FEATURE [App::DocumentObjectGroupPython] G4_LITHIUM_CARBONATE  # scripted group (container) (typed FeaturePython)
  Dunit = g/cm3
  Dvalue = 2.11
  Group = -> [Li_element002,C_element055,O_element054]
  conduct = 2
  density = 1
  expand = 3
  formula = G4_LITHIUM_CARBONATE
  name = G4_LITHIUM_CARBONATE
  specific = 4
FEATURE [App::DocumentObjectGroupPython] Li_element003  label="Li_element : 003"  # scripted group (container) (typed FeaturePython)
  n = 1
  ref = Li_element
FEATURE [App::DocumentObjectGroupPython] F_element012  label="F_element : 004"  # scripted group (container) (typed FeaturePython)
  n = 1
  ref = F_element
FEATURE [App::DocumentObjectGroupPython] G4_LITHIUM_FLUORIDE  # scripted group (container) (typed FeaturePython)
  Dunit = g/cm3
  Dvalue = 2.635
  Group = -> [Li_element003,F_element012]
  conduct = 2
  density = 1
  expand = 3
  formula = G4_LITHIUM_FLUORIDE
  name = G4_LITHIUM_FLUORIDE
  specific = 4
FEATURE [App::DocumentObjectGroupPython] Li_element004  label="Li_element : 004"  # scripted group (container) (typed FeaturePython)
  n = 1
  ref = Li_element
FEATURE [App::DocumentObjectGroupPython] H_element050  label="H_element : 027"  # scripted group (container) (typed FeaturePython)
  n = 1
  ref = H_element
FEATURE [App::DocumentObjectGroupPython] G4_LITHIUM_HYDRIDE  # scripted group (container) (typed FeaturePython)
  Dunit = g/cm3
  Dvalue = 0.82
  Group = -> [Li_element004,H_element050]
  conduct = 2
  density = 1
  expand = 3
  formula = G4_LITHIUM_HYDRIDE
  name = G4_LITHIUM_HYDRIDE
  specific = 4
FEATURE [App::DocumentObjectGroupPython] Li_element005  label="Li_element : 005"  # scripted group (container) (typed FeaturePython)
  n = 1
  ref = Li_element
FEATURE [App::DocumentObjectGroupPython] I_element003  label="I_element : 002"  # scripted group (container) (typed FeaturePython)
  n = 1
  ref = I_element
FEATURE [App::DocumentObjectGroupPython] G4_LITHIUM_IODIDE  # scripted group (container) (typed FeaturePython)
  Dunit = g/cm3
  Dvalue = 3.494
  Group = -> [Li_element005,I_element003]
  conduct = 2
  density = 1
  expand = 3
  formula = G4_LITHIUM_IODIDE
  name = G4_LITHIUM_IODIDE
  specific = 4
FEATURE [App::DocumentObjectGroupPython] Li_element006  label="Li_element : 006"  # scripted group (container) (typed FeaturePython)
  n = 2
  ref = Li_element
FEATURE [App::DocumentObjectGroupPython] O_element055  label="O_element : 029"  # scripted group (container) (typed FeaturePython)
  n = 1
  ref = O_element
FEATURE [App::DocumentObjectGroupPython] G4_LITHIUM_OXIDE  # scripted group (container) (typed FeaturePython)
  Dunit = g/cm3
  Dvalue = 2.013
  Group = -> [Li_element006,O_element055]
  conduct = 2
  density = 1
  expand = 3
  formula = G4_LITHIUM_OXIDE
  name = G4_LITHIUM_OXIDE
  specific = 4
FEATURE [App::DocumentObjectGroupPython] Li_element007  label="Li_element : 007"  # scripted group (container) (typed FeaturePython)
  n = 2
  ref = Li_element
FEATURE [App::DocumentObjectGroupPython] B_element005  label="B_element : 005"  # scripted group (container) (typed FeaturePython)
  n = 4
  ref = B_element
FEATURE [App::DocumentObjectGroupPython] O_element056  label="O_element : 7"  # scripted group (container) (typed FeaturePython)
  n = 7
  ref = O_element
FEATURE [App::DocumentObjectGroupPython] G4_LITHIUM_TETRABORATE  # scripted group (container) (typed FeaturePython)
  Dunit = g/cm3
  Dvalue = 2.44
  Group = -> [Li_element007,B_element005,O_element056]
  conduct = 2
  density = 1
  expand = 3
  formula = G4_LITHIUM_TETRABORATE
  name = G4_LITHIUM_TETRABORATE
  specific = 4
FEATURE [App::DocumentObjectGroupPython] H_element051  label="H_element : 0.105"  # scripted group (container) (typed FeaturePython)
  n = 0.105
FEATURE [App::DocumentObjectGroupPython] C_element056  label="C_element : 0.083"  # scripted group (container) (typed FeaturePython)
  n = 0.083
FEATURE [App::DocumentObjectGroupPython] N_element023  label="N_element : 0.023"  # scripted group (container) (typed FeaturePython)
  n = 0.023
FEATURE [App::DocumentObjectGroupPython] O_element057  label="O_element : 0.779"  # scripted group (container) (typed FeaturePython)
  n = 0.779
FEATURE [App::DocumentObjectGroupPython] Na_element010  label="Na_element : 0.097"  # scripted group (container) (typed FeaturePython)
  n = 0.002
FEATURE [App::DocumentObjectGroupPython] P_element006  label="P_element : 0.105"  # scripted group (container) (typed FeaturePython)
  n = 0.001
FEATURE [App::DocumentObjectGroupPython] S_element016  label="S_element : 0.017"  # scripted group (container) (typed FeaturePython)
  n = 0.002
FEATURE [App::DocumentObjectGroupPython] Cl_element014  label="Cl_element : 0.587"  # scripted group (container) (typed FeaturePython)
  n = 0.003
FEATURE [App::DocumentObjectGroupPython] K_element005  label="K_element : 0.015"  # scripted group (container) (typed FeaturePython)
  n = 0.002
FEATURE [App::DocumentObjectGroupPython] G4_LUNG_ICRP  # scripted group (container) (typed FeaturePython)
  Dunit = g/cm3
  Dvalue = 1.04
  Group = -> [H_element051,C_element056,N_element023,O_element057,Na_element010,P_element006,S_element016,Cl_element014,K_element005]
  conduct = 2
  density = 1
  expand = 3
  formula = G4_LUNG_ICRP
  name = G4_LUNG_ICRP
  specific = 4
FEATURE [App::DocumentObjectGroupPython] H_element052  label="H_element : 0.116"  # scripted group (container) (typed FeaturePython)
  n = 0.114318
FEATURE [App::DocumentObjectGroupPython] C_element057  label="C_element : 0.656"  # scripted group (container) (typed FeaturePython)
  n = 0.655824
FEATURE [App::DocumentObjectGroupPython] O_element058  label="O_element : 0.092"  # scripted group (container) (typed FeaturePython)
  n = 0.0921831
FEATURE [App::DocumentObjectGroupPython] Mg_element004  label="Mg_element : 0.135"  # scripted group (container) (typed FeaturePython)
  n = 0.134792
FEATURE [App::DocumentObjectGroupPython] Ca_element013  label="Ca_element : 0.003"  # scripted group (container) (typed FeaturePython)
  n = 0.002883
FEATURE [App::DocumentObjectGroupPython] G4_M3_WAX  # scripted group (container) (typed FeaturePython)
  Dunit = g/cm3
  Dvalue = 1.05
  Group = -> [H_element052,C_element057,O_element058,Mg_element004,Ca_element013]
  conduct = 2
  density = 1
  expand = 3
  formula = G4_M3_WAX
  name = G4_M3_WAX
  specific = 4
FEATURE [App::DocumentObjectGroupPython] Mg_element005  label="Mg_element : 1"  # scripted group (container) (typed FeaturePython)
  n = 1
  ref = Mg_element
FEATURE [App::DocumentObjectGroupPython] C_element058  label="C_element : 031"  # scripted group (container) (typed FeaturePython)
  n = 1
  ref = C_element
FEATURE [App::DocumentObjectGroupPython] O_element059  label="O_element : 030"  # scripted group (container) (typed FeaturePython)
  n = 3
  ref = O_element
FEATURE [App::DocumentObjectGroupPython] G4_MAGNESIUM_CARBONATE  # scripted group (container) (typed FeaturePython)
  Dunit = g/cm3
  Dvalue = 2.958
  Group = -> [Mg_element005,C_element058,O_element059]
  conduct = 2
  density = 1
  expand = 3
  formula = G4_MAGNESIUM_CARBONATE
  name = G4_MAGNESIUM_CARBONATE
  specific = 4
FEATURE [App::DocumentObjectGroupPython] Mg_element006  label="Mg_element : 002"  # scripted group (container) (typed FeaturePython)
  n = 1
  ref = Mg_element
FEATURE [App::DocumentObjectGroupPython] F_element013  label="F_element : 005"  # scripted group (container) (typed FeaturePython)
  n = 2
  ref = F_element
FEATURE [App::DocumentObjectGroupPython] G4_MAGNESIUM_FLUORIDE  # scripted group (container) (typed FeaturePython)
  Dunit = g/cm3
  Dvalue = 3
  Group = -> [Mg_element006,F_element013]
  conduct = 2
  density = 1
  expand = 3
  formula = G4_MAGNESIUM_FLUORIDE
  name = G4_MAGNESIUM_FLUORIDE
  specific = 4
FEATURE [App::DocumentObjectGroupPython] Mg_element007  label="Mg_element : 003"  # scripted group (container) (typed FeaturePython)
  n = 1
  ref = Mg_element
FEATURE [App::DocumentObjectGroupPython] O_element060  label="O_element : 031"  # scripted group (container) (typed FeaturePython)
  n = 1
  ref = O_element
FEATURE [App::DocumentObjectGroupPython] G4_MAGNESIUM_OXIDE  # scripted group (container) (typed FeaturePython)
  Dunit = g/cm3
  Dvalue = 3.58
  Group = -> [Mg_element007,O_element060]
  conduct = 2
  density = 1
  expand = 3
  formula = G4_MAGNESIUM_OXIDE
  name = G4_MAGNESIUM_OXIDE
  specific = 4
FEATURE [App::DocumentObjectGroupPython] Mg_element008  label="Mg_element : 004"  # scripted group (container) (typed FeaturePython)
  n = 1
  ref = Mg_element
FEATURE [App::DocumentObjectGroupPython] B_element006  label="B_element : 006"  # scripted group (container) (typed FeaturePython)
  n = 4
  ref = B_element
FEATURE [App::DocumentObjectGroupPython] O_element061  label="O_element : 032"  # scripted group (container) (typed FeaturePython)
  n = 7
  ref = O_element
FEATURE [App::DocumentObjectGroupPython] G4_MAGNESIUM_TETRABORATE  # scripted group (container) (typed FeaturePython)
  Dunit = g/cm3
  Dvalue = 2.53
  Group = -> [Mg_element008,B_element006,O_element061]
  conduct = 2
  density = 1
  expand = 3
  formula = G4_MAGNESIUM_TETRABORATE
  name = G4_MAGNESIUM_TETRABORATE
  specific = 4
FEATURE [App::DocumentObjectGroupPython] Hg_element001  label="Hg_element : 1"  # scripted group (container) (typed FeaturePython)
  n = 1
  ref = Hg_element
FEATURE [App::DocumentObjectGroupPython] I_element004  label="I_element : 2"  # scripted group (container) (typed FeaturePython)
  n = 2
  ref = I_element
FEATURE [App::DocumentObjectGroupPython] G4_MERCURIC_IODIDE  # scripted group (container) (typed FeaturePython)
  Dunit = g/cm3
  Dvalue = 6.36
  Group = -> [Hg_element001,I_element004]
  conduct = 2
  density = 1
  expand = 3
  formula = G4_MERCURIC_IODIDE
  name = G4_MERCURIC_IODIDE
  specific = 4
FEATURE [App::DocumentObjectGroupPython] C_element059  label="C_element : 032"  # scripted group (container) (typed FeaturePython)
  n = 1
  ref = C_element
FEATURE [App::DocumentObjectGroupPython] H_element053  label="H_element : 028"  # scripted group (container) (typed FeaturePython)
  n = 4
  ref = H_element
FEATURE [App::DocumentObjectGroupPython] G4_METHANE  # scripted group (container) (typed FeaturePython)
  Dunit = g/cm3
  Dvalue = 0.000667151
  Group = -> [C_element059,H_element053]
  conduct = 2
  density = 1
  expand = 3
  formula = G4_METHANE
  name = G4_METHANE
  specific = 4
FEATURE [App::DocumentObjectGroupPython] C_element060  label="C_element : 033"  # scripted group (container) (typed FeaturePython)
  n = 1
  ref = C_element
FEATURE [App::DocumentObjectGroupPython] H_element054  label="H_element : 029"  # scripted group (container) (typed FeaturePython)
  n = 4
  ref = H_element
FEATURE [App::DocumentObjectGroupPython] O_element062  label="O_element : 033"  # scripted group (container) (typed FeaturePython)
  n = 1
  ref = O_element
FEATURE [App::DocumentObjectGroupPython] G4_METHANOL  # scripted group (container) (typed FeaturePython)
  Dunit = g/cm3
  Dvalue = 0.7914
  Group = -> [C_element060,H_element054,O_element062]
  conduct = 2
  density = 1
  expand = 3
  formula = G4_METHANOL
  name = G4_METHANOL
  specific = 4
FEATURE [App::DocumentObjectGroupPython] H_element055  label="H_element : 0.134"  # scripted group (container) (typed FeaturePython)
  n = 0.13404
FEATURE [App::DocumentObjectGroupPython] C_element061  label="C_element : 0.778"  # scripted group (container) (typed FeaturePython)
  n = 0.77796
FEATURE [App::DocumentObjectGroupPython] O_element063  label="O_element : 0.035"  # scripted group (container) (typed FeaturePython)
  n = 0.03502
FEATURE [App::DocumentObjectGroupPython] Mg_element009  label="Mg_element : 0.039"  # scripted group (container) (typed FeaturePython)
  n = 0.038594
FEATURE [App::DocumentObjectGroupPython] Ti_element002  label="Ti_element : 0.014"  # scripted group (container) (typed FeaturePython)
  n = 0.014386
FEATURE [App::DocumentObjectGroupPython] G4_MIX_D_WAX  # scripted group (container) (typed FeaturePython)
  Dunit = g/cm3
  Dvalue = 0.99
  Group = -> [H_element055,C_element061,O_element063,Mg_element009,Ti_element002]
  conduct = 2
  density = 1
  expand = 3
  formula = G4_MIX_D_WAX
  name = G4_MIX_D_WAX
  specific = 4
FEATURE [App::DocumentObjectGroupPython] H_element056  label="H_element : 0.135"  # scripted group (container) (typed FeaturePython)
  n = 0.081192
FEATURE [App::DocumentObjectGroupPython] C_element062  label="C_element : 0.583"  # scripted group (container) (typed FeaturePython)
  n = 0.583442
FEATURE [App::DocumentObjectGroupPython] N_element024  label="N_element : 0.018"  # scripted group (container) (typed FeaturePython)
  n = 0.017798
FEATURE [App::DocumentObjectGroupPython] O_element064  label="O_element : 0.186"  # scripted group (container) (typed FeaturePython)
  n = 0.186381
FEATURE [App::DocumentObjectGroupPython] Mg_element010  label="Mg_element : 0.130"  # scripted group (container) (typed FeaturePython)
  n = 0.130287
FEATURE [App::DocumentObjectGroupPython] Cl_element015  label="Cl_element : 0.588"  # scripted group (container) (typed FeaturePython)
  n = 0.0009
FEATURE [App::DocumentObjectGroupPython] G4_MS20_TISSUE  # scripted group (container) (typed FeaturePython)
  Dunit = g/cm3
  Dvalue = 1
  Group = -> [H_element056,C_element062,N_element024,O_element064,Mg_element010,Cl_element015]
  conduct = 2
  density = 1
  expand = 3
  formula = G4_MS20_TISSUE
  name = G4_MS20_TISSUE
  specific = 4
FEATURE [App::DocumentObjectGroupPython] H_element057  label="H_element : 0.136"  # scripted group (container) (typed FeaturePython)
  n = 0.102
FEATURE [App::DocumentObjectGroupPython] C_element063  label="C_element : 0.143"  # scripted group (container) (typed FeaturePython)
  n = 0.143
FEATURE [App::DocumentObjectGroupPython] N_element025  label="N_element : 0.034"  # scripted group (container) (typed FeaturePython)
  n = 0.034
FEATURE [App::DocumentObjectGroupPython] O_element065  label="O_element : 0.710"  # scripted group (container) (typed FeaturePython)
  n = 0.71
FEATURE [App::DocumentObjectGroupPython] Na_element011  label="Na_element : 0.098"  # scripted group (container) (typed FeaturePython)
  n = 0.001
FEATURE [App::DocumentObjectGroupPython] P_element007  label="P_element : 0.002"  # scripted group (container) (typed FeaturePython)
  n = 0.002
FEATURE [App::DocumentObjectGroupPython] S_element017  label="S_element : 0.018"  # scripted group (container) (typed FeaturePython)
  n = 0.003
FEATURE [App::DocumentObjectGroupPython] Cl_element016  label="Cl_element : 0.589"  # scripted group (container) (typed FeaturePython)
  n = 0.001
FEATURE [App::DocumentObjectGroupPython] K_element006  label="K_element : 0.004"  # scripted group (container) (typed FeaturePython)
  n = 0.004
FEATURE [App::DocumentObjectGroupPython] G4_MUSCLE_SKELETAL_ICRP  # scripted group (container) (typed FeaturePython)
  Dunit = g/cm3
  Dvalue = 1.05
  Group = -> [H_element057,C_element063,N_element025,O_element065,Na_element011,P_element007,S_element017,Cl_element016,K_element006]
  conduct = 2
  density = 1
  expand = 3
  formula = G4_MUSCLE_SKELETAL_ICRP
  name = G4_MUSCLE_SKELETAL_ICRP
  specific = 4
FEATURE [App::DocumentObjectGroupPython] H_element058  label="H_element : 0.137"  # scripted group (container) (typed FeaturePython)
  n = 0.102102
FEATURE [App::DocumentObjectGroupPython] C_element064  label="C_element : 0.123"  # scripted group (container) (typed FeaturePython)
  n = 0.123123
FEATURE [App::DocumentObjectGroupPython] N_element026  label="N_element : 0.756"  # scripted group (container) (typed FeaturePython)
  n = 0.035035
FEATURE [App::DocumentObjectGroupPython] O_element066  label="O_element : 0.730"  # scripted group (container) (typed FeaturePython)
  n = 0.72973
FEATURE [App::DocumentObjectGroupPython] Na_element012  label="Na_element : 0.099"  # scripted group (container) (typed FeaturePython)
  n = 0.001001
FEATURE [App::DocumentObjectGroupPython] P_element008  label="P_element : 0.106"  # scripted group (container) (typed FeaturePython)
  n = 0.002002
FEATURE [App::DocumentObjectGroupPython] S_element018  label="S_element : 0.019"  # scripted group (container) (typed FeaturePython)
  n = 0.004004
FEATURE [App::DocumentObjectGroupPython] K_element007  label="K_element : 0.016"  # scripted group (container) (typed FeaturePython)
  n = 0.003003
FEATURE [App::DocumentObjectGroupPython] G4_MUSCLE_STRIATED_ICRU  # scripted group (container) (typed FeaturePython)
  Dunit = g/cm3
  Dvalue = 1.04
  Group = -> [H_element058,C_element064,N_element026,O_element066,Na_element012,P_element008,S_element018,K_element007]
  conduct = 2
  density = 1
  expand = 3
  formula = G4_MUSCLE_STRIATED_ICRU
  name = G4_MUSCLE_STRIATED_ICRU
  specific = 4
FEATURE [App::DocumentObjectGroupPython] H_element059  label="H_element : 0.098"  # scripted group (container) (typed FeaturePython)
  n = 0.0982341
FEATURE [App::DocumentObjectGroupPython] C_element065  label="C_element : 0.156"  # scripted group (container) (typed FeaturePython)
  n = 0.156214
FEATURE [App::DocumentObjectGroupPython] N_element027  label="N_element : 0.757"  # scripted group (container) (typed FeaturePython)
  n = 0.035451
FEATURE [App::DocumentObjectGroupPython] O_element067  label="O_element : 0.880"  # scripted group (container) (typed FeaturePython)
  n = 0.710101
FEATURE [App::DocumentObjectGroupPython] G4_MUSCLE_WITH_SUCROSE  # scripted group (container) (typed FeaturePython)
  Dunit = g/cm3
  Dvalue = 1.11
  Group = -> [H_element059,C_element065,N_element027,O_element067]
  conduct = 2
  density = 1
  expand = 3
  formula = G4_MUSCLE_WITH_SUCROSE
  name = G4_MUSCLE_WITH_SUCROSE
  specific = 4
FEATURE [App::DocumentObjectGroupPython] H_element060  label="H_element : 0.138"  # scripted group (container) (typed FeaturePython)
  n = 0.101969
FEATURE [App::DocumentObjectGroupPython] C_element066  label="C_element : 0.120"  # scripted group (container) (typed FeaturePython)
  n = 0.120058
FEATURE [App::DocumentObjectGroupPython] N_element028  label="N_element : 0.758"  # scripted group (container) (typed FeaturePython)
  n = 0.035451
FEATURE [App::DocumentObjectGroupPython] O_element068  label="O_element : 0.743"  # scripted group (container) (typed FeaturePython)
  n = 0.742522
FEATURE [App::DocumentObjectGroupPython] G4_MUSCLE_WITHOUT_SUCROSE  # scripted group (container) (typed FeaturePython)
  Dunit = g/cm3
  Dvalue = 1.07
  Group = -> [H_element060,C_element066,N_element028,O_element068]
  conduct = 2
  density = 1
  expand = 3
  formula = G4_MUSCLE_WITHOUT_SUCROSE
  name = G4_MUSCLE_WITHOUT_SUCROSE
  specific = 4
FEATURE [App::DocumentObjectGroupPython] C_element067  label="C_element : 10"  # scripted group (container) (typed FeaturePython)
  n = 10
  ref = C_element
FEATURE [App::DocumentObjectGroupPython] H_element061  label="H_element : 030"  # scripted group (container) (typed FeaturePython)
  n = 8
  ref = H_element
FEATURE [App::DocumentObjectGroupPython] G4_NAPHTHALENE  # scripted group (container) (typed FeaturePython)
  Dunit = g/cm3
  Dvalue = 1.145
  Group = -> [C_element067,H_element061]
  conduct = 2
  density = 1
  expand = 3
  formula = G4_NAPHTHALENE
  name = G4_NAPHTHALENE
  specific = 4
FEATURE [App::DocumentObjectGroupPython] C_element068  label="C_element : 034"  # scripted group (container) (typed FeaturePython)
  n = 6
  ref = C_element
FEATURE [App::DocumentObjectGroupPython] H_element062  label="H_element : 031"  # scripted group (container) (typed FeaturePython)
  n = 5
  ref = H_element
FEATURE [App::DocumentObjectGroupPython] N_element029  label="N_element : 012"  # scripted group (container) (typed FeaturePython)
  n = 1
  ref = N_element
FEATURE [App::DocumentObjectGroupPython] O_element069  label="O_element : 034"  # scripted group (container) (typed FeaturePython)
  n = 2
  ref = O_element
FEATURE [App::DocumentObjectGroupPython] G4_NITROBENZENE  # scripted group (container) (typed FeaturePython)
  Dunit = g/cm3
  Dvalue = 1.19867
  Group = -> [C_element068,H_element062,N_element029,O_element069]
  conduct = 2
  density = 1
  expand = 3
  formula = G4_NITROBENZENE
  name = G4_NITROBENZENE
  specific = 4
FEATURE [App::DocumentObjectGroupPython] N_element030  label="N_element : 013"  # scripted group (container) (typed FeaturePython)
  n = 2
  ref = N_element
FEATURE [App::DocumentObjectGroupPython] O_element070  label="O_element : 035"  # scripted group (container) (typed FeaturePython)
  n = 1
  ref = O_element
FEATURE [App::DocumentObjectGroupPython] G4_NITROUS_OXIDE  # scripted group (container) (typed FeaturePython)
  Dunit = g/cm3
  Dvalue = 0.00183094
  Group = -> [N_element030,O_element070]
  conduct = 2
  density = 1
  expand = 3
  formula = G4_NITROUS_OXIDE
  name = G4_NITROUS_OXIDE
  specific = 4
FEATURE [App::DocumentObjectGroupPython] H_element063  label="H_element : 0.104"  # scripted group (container) (typed FeaturePython)
  n = 0.103509
FEATURE [App::DocumentObjectGroupPython] C_element069  label="C_element : 0.648"  # scripted group (container) (typed FeaturePython)
  n = 0.648416
FEATURE [App::DocumentObjectGroupPython] N_element031  label="N_element : 0.100"  # scripted group (container) (typed FeaturePython)
  n = 0.0995361
FEATURE [App::DocumentObjectGroupPython] O_element071  label="O_element : 0.149"  # scripted group (container) (typed FeaturePython)
  n = 0.148539
FEATURE [App::DocumentObjectGroupPython] G4_NYLON_8062  label="G4_NYLON-8062"  # scripted group (container) (typed FeaturePython)
  Dunit = g/cm3
  Dvalue = 1.08
  Group = -> [H_element063,C_element069,N_element031,O_element071]
  conduct = 2
  density = 1
  expand = 3
  formula = G4_NYLON-8062
  name = G4_NYLON-8062
  specific = 4
FEATURE [App::DocumentObjectGroupPython] C_element070  label="C_element : 035"  # scripted group (container) (typed FeaturePython)
  n = 6
  ref = C_element
FEATURE [App::DocumentObjectGroupPython] H_element064  label="H_element : 11"  # scripted group (container) (typed FeaturePython)
  n = 11
  ref = H_element
FEATURE [App::DocumentObjectGroupPython] N_element032  label="N_element : 014"  # scripted group (container) (typed FeaturePython)
  n = 1
  ref = N_element
FEATURE [App::DocumentObjectGroupPython] O_element072  label="O_element : 036"  # scripted group (container) (typed FeaturePython)
  n = 1
  ref = O_element
FEATURE [App::DocumentObjectGroupPython] G4_NYLON_6_6  label="G4_NYLON-6-6"  # scripted group (container) (typed FeaturePython)
  Dunit = g/cm3
  Dvalue = 1.14
  Group = -> [C_element070,H_element064,N_element032,O_element072]
  conduct = 2
  density = 1
  expand = 3
  formula = G4_NYLON-6-6
  name = G4_NYLON-6-6
  specific = 4
FEATURE [App::DocumentObjectGroupPython] H_element065  label="H_element : 0.139"  # scripted group (container) (typed FeaturePython)
  n = 0.107062
FEATURE [App::DocumentObjectGroupPython] C_element071  label="C_element : 0.680"  # scripted group (container) (typed FeaturePython)
  n = 0.680449
FEATURE [App::DocumentObjectGroupPython] N_element033  label="N_element : 0.099"  # scripted group (container) (typed FeaturePython)
  n = 0.099189
FEATURE [App::DocumentObjectGroupPython] O_element073  label="O_element : 0.113"  # scripted group (container) (typed FeaturePython)
  n = 0.1133
FEATURE [App::DocumentObjectGroupPython] G4_NYLON_6_10  label="G4_NYLON-6-10"  # scripted group (container) (typed FeaturePython)
  Dunit = g/cm3
  Dvalue = 1.14
  Group = -> [H_element065,C_element071,N_element033,O_element073]
  conduct = 2
  density = 1
  expand = 3
  formula = G4_NYLON-6-10
  name = G4_NYLON-6-10
  specific = 4
FEATURE [App::DocumentObjectGroupPython] H_element066  label="H_element : 0.140"  # scripted group (container) (typed FeaturePython)
  n = 0.115476
FEATURE [App::DocumentObjectGroupPython] C_element072  label="C_element : 0.721"  # scripted group (container) (typed FeaturePython)
  n = 0.720818
FEATURE [App::DocumentObjectGroupPython] N_element034  label="N_element : 0.076"  # scripted group (container) (typed FeaturePython)
  n = 0.0764169
FEATURE [App::DocumentObjectGroupPython] O_element074  label="O_element : 0.087"  # scripted group (container) (typed FeaturePython)
  n = 0.0872889
FEATURE [App::DocumentObjectGroupPython] G4_NYLON_11_RILSAN  label="G4_NYLON-11_RILSAN"  # scripted group (container) (typed FeaturePython)
  Dunit = g/cm3
  Dvalue = 1.425
  Group = -> [H_element066,C_element072,N_element034,O_element074]
  conduct = 2
  density = 1
  expand = 3
  formula = G4_NYLON-11_RILSAN
  name = G4_NYLON-11_RILSAN
  specific = 4
FEATURE [App::DocumentObjectGroupPython] C_element073  label="C_element : 8"  # scripted group (container) (typed FeaturePython)
  n = 8
  ref = C_element
FEATURE [App::DocumentObjectGroupPython] H_element067  label="H_element : 18"  # scripted group (container) (typed FeaturePython)
  n = 18
  ref = H_element
FEATURE [App::DocumentObjectGroupPython] G4_OCTANE  # scripted group (container) (typed FeaturePython)
  Dunit = g/cm3
  Dvalue = 0.7026
  Group = -> [C_element073,H_element067]
  conduct = 2
  density = 1
  expand = 3
  formula = G4_OCTANE
  name = G4_OCTANE
  specific = 4
FEATURE [App::DocumentObjectGroupPython] C_element074  label="C_element : 25"  # scripted group (container) (typed FeaturePython)
  n = 25
  ref = C_element
FEATURE [App::DocumentObjectGroupPython] H_element068  label="H_element : 52"  # scripted group (container) (typed FeaturePython)
  n = 52
  ref = H_element
FEATURE [App::DocumentObjectGroupPython] G4_PARAFFIN  # scripted group (container) (typed FeaturePython)
  Dunit = g/cm3
  Dvalue = 0.93
  Group = -> [C_element074,H_element068]
  conduct = 2
  density = 1
  expand = 3
  formula = G4_PARAFFIN
  name = G4_PARAFFIN
  specific = 4
FEATURE [App::DocumentObjectGroupPython] C_element075  label="C_element : 036"  # scripted group (container) (typed FeaturePython)
  n = 5
  ref = C_element
FEATURE [App::DocumentObjectGroupPython] H_element069  label="H_element : 032"  # scripted group (container) (typed FeaturePython)
  n = 12
  ref = H_element
FEATURE [App::DocumentObjectGroupPython] G4_N_PENTANE  label="G4_N-PENTANE"  # scripted group (container) (typed FeaturePython)
  Dunit = g/cm3
  Dvalue = 0.6262
  Group = -> [C_element075,H_element069]
  conduct = 2
  density = 1
  expand = 3
  formula = G4_N-PENTANE
  name = G4_N-PENTANE
  specific = 4
FEATURE [App::DocumentObjectGroupPython] H_element070  label="H_element : 0.014"  # scripted group (container) (typed FeaturePython)
  n = 0.0141
FEATURE [App::DocumentObjectGroupPython] C_element076  label="C_element : 0.072"  # scripted group (container) (typed FeaturePython)
  n = 0.072261
FEATURE [App::DocumentObjectGroupPython] N_element035  label="N_element : 0.019"  # scripted group (container) (typed FeaturePython)
  n = 0.01932
FEATURE [App::DocumentObjectGroupPython] O_element075  label="O_element : 0.066"  # scripted group (container) (typed FeaturePython)
  n = 0.066101
FEATURE [App::DocumentObjectGroupPython] S_element019  label="S_element : 0.020"  # scripted group (container) (typed FeaturePython)
  n = 0.00189
FEATURE [App::DocumentObjectGroupPython] Br_element004  label="Br_element : 0.349"  # scripted group (container) (typed FeaturePython)
  n = 0.349103
FEATURE [App::DocumentObjectGroupPython] Ag_element001  label="Ag_element : 0.474"  # scripted group (container) (typed FeaturePython)
  n = 0.474105
FEATURE [App::DocumentObjectGroupPython] I_element005  label="I_element : 0.003"  # scripted group (container) (typed FeaturePython)
  n = 0.00312
FEATURE [App::DocumentObjectGroupPython] G4_PHOTO_EMULSION  # scripted group (container) (typed FeaturePython)
  Dunit = g/cm3
  Dvalue = 3.815
  Group = -> [H_element070,C_element076,N_element035,O_element075,S_element019,Br_element004,Ag_element001,I_element005]
  conduct = 2
  density = 1
  expand = 3
  formula = G4_PHOTO_EMULSION
  name = G4_PHOTO_EMULSION
  specific = 4
FEATURE [App::DocumentObjectGroupPython] C_element077  label="C_element : 9"  # scripted group (container) (typed FeaturePython)
  n = 9
  ref = C_element
FEATURE [App::DocumentObjectGroupPython] H_element071  label="H_element : 033"  # scripted group (container) (typed FeaturePython)
  n = 10
  ref = H_element
FEATURE [App::DocumentObjectGroupPython] G4_PLASTIC_SC_VINYLTOLUENE  # scripted group (container) (typed FeaturePython)
  Dunit = g/cm3
  Dvalue = 1.032
  Group = -> [C_element077,H_element071]
  conduct = 2
  density = 1
  expand = 3
  formula = G4_PLASTIC_SC_VINYLTOLUENE
  name = G4_PLASTIC_SC_VINYLTOLUENE
  specific = 4
FEATURE [App::DocumentObjectGroupPython] Pu_element001  label="Pu_element : 1"  # scripted group (container) (typed FeaturePython)
  n = 1
  ref = Pu_element
FEATURE [App::DocumentObjectGroupPython] O_element076  label="O_element : 037"  # scripted group (container) (typed FeaturePython)
  n = 2
  ref = O_element
FEATURE [App::DocumentObjectGroupPython] G4_PLUTONIUM_DIOXIDE  # scripted group (container) (typed FeaturePython)
  Dunit = g/cm3
  Dvalue = 11.46
  Group = -> [Pu_element001,O_element076]
  conduct = 2
  density = 1
  expand = 3
  formula = G4_PLUTONIUM_DIOXIDE
  name = G4_PLUTONIUM_DIOXIDE
  specific = 4
FEATURE [App::DocumentObjectGroupPython] C_element078  label="C_element : 037"  # scripted group (container) (typed FeaturePython)
  n = 3
  ref = C_element
FEATURE [App::DocumentObjectGroupPython] H_element072  label="H_element : 034"  # scripted group (container) (typed FeaturePython)
  n = 3
  ref = H_element
FEATURE [App::DocumentObjectGroupPython] N_element036  label="N_element : 015"  # scripted group (container) (typed FeaturePython)
  n = 1
  ref = N_element
FEATURE [App::DocumentObjectGroupPython] G4_POLYACRYLONITRILE  # scripted group (container) (typed FeaturePython)
  Dunit = g/cm3
  Dvalue = 1.17
  Group = -> [C_element078,H_element072,N_element036]
  conduct = 2
  density = 1
  expand = 3
  formula = G4_POLYACRYLONITRILE
  name = G4_POLYACRYLONITRILE
  specific = 4
FEATURE [App::DocumentObjectGroupPython] C_element079  label="C_element : 16"  # scripted group (container) (typed FeaturePython)
  n = 16
  ref = C_element
FEATURE [App::DocumentObjectGroupPython] H_element073  label="H_element : 035"  # scripted group (container) (typed FeaturePython)
  n = 14
  ref = H_element
FEATURE [App::DocumentObjectGroupPython] O_element077  label="O_element : 038"  # scripted group (container) (typed FeaturePython)
  n = 3
  ref = O_element
FEATURE [App::DocumentObjectGroupPython] G4_POLYCARBONATE  # scripted group (container) (typed FeaturePython)
  Dunit = g/cm3
  Dvalue = 1.2
  Group = -> [C_element079,H_element073,O_element077]
  conduct = 2
  density = 1
  expand = 3
  formula = G4_POLYCARBONATE
  name = G4_POLYCARBONATE
  specific = 4
FEATURE [App::DocumentObjectGroupPython] C_element080  label="C_element : 038"  # scripted group (container) (typed FeaturePython)
  n = 8
  ref = C_element
FEATURE [App::DocumentObjectGroupPython] H_element074  label="H_element : 036"  # scripted group (container) (typed FeaturePython)
  n = 7
  ref = H_element
FEATURE [App::DocumentObjectGroupPython] Cl_element017  label="Cl_element : 007"  # scripted group (container) (typed FeaturePython)
  n = 1
  ref = Cl_element
FEATURE [App::DocumentObjectGroupPython] G4_POLYCHLOROSTYRENE  # scripted group (container) (typed FeaturePython)
  Dunit = g/cm3
  Dvalue = 1.3
  Group = -> [C_element080,H_element074,Cl_element017]
  conduct = 2
  density = 1
  expand = 3
  formula = G4_POLYCHLOROSTYRENE
  name = G4_POLYCHLOROSTYRENE
  specific = 4
FEATURE [App::DocumentObjectGroupPython] C_element081  label="C_element : 039"  # scripted group (container) (typed FeaturePython)
  n = 1
  ref = C_element
FEATURE [App::DocumentObjectGroupPython] H_element075  label="H_element : 037"  # scripted group (container) (typed FeaturePython)
  n = 2
  ref = H_element
FEATURE [App::DocumentObjectGroupPython] G4_POLYETHYLENE  # scripted group (container) (typed FeaturePython)
  Dunit = g/cm3
  Dvalue = 0.94
  Group = -> [C_element081,H_element075]
  conduct = 2
  density = 1
  expand = 3
  formula = G4_POLYETHYLENE
  name = G4_POLYETHYLENE
  specific = 4
FEATURE [App::DocumentObjectGroupPython] C_element082  label="C_element : 040"  # scripted group (container) (typed FeaturePython)
  n = 10
  ref = C_element
FEATURE [App::DocumentObjectGroupPython] H_element076  label="H_element : 038"  # scripted group (container) (typed FeaturePython)
  n = 8
  ref = H_element
FEATURE [App::DocumentObjectGroupPython] O_element078  label="O_element : 039"  # scripted group (container) (typed FeaturePython)
  n = 4
  ref = O_element
FEATURE [App::DocumentObjectGroupPython] G4_MYLAR  # scripted group (container) (typed FeaturePython)
  Dunit = g/cm3
  Dvalue = 1.4
  Group = -> [C_element082,H_element076,O_element078]
  conduct = 2
  density = 1
  expand = 3
  formula = G4_MYLAR
  name = G4_MYLAR
  specific = 4
FEATURE [App::DocumentObjectGroupPython] C_element083  label="C_element : 041"  # scripted group (container) (typed FeaturePython)
  n = 5
  ref = C_element
FEATURE [App::DocumentObjectGroupPython] H_element077  label="H_element : 039"  # scripted group (container) (typed FeaturePython)
  n = 8
  ref = H_element
FEATURE [App::DocumentObjectGroupPython] O_element079  label="O_element : 040"  # scripted group (container) (typed FeaturePython)
  n = 2
  ref = O_element
FEATURE [App::DocumentObjectGroupPython] G4_PLEXIGLASS  # scripted group (container) (typed FeaturePython)
  Dunit = g/cm3
  Dvalue = 1.19
  Group = -> [C_element083,H_element077,O_element079]
  conduct = 2
  density = 1
  expand = 3
  formula = G4_PLEXIGLASS
  name = G4_PLEXIGLASS
  specific = 4
FEATURE [App::DocumentObjectGroupPython] C_element084  label="C_element : 042"  # scripted group (container) (typed FeaturePython)
  n = 1
  ref = C_element
FEATURE [App::DocumentObjectGroupPython] H_element078  label="H_element : 040"  # scripted group (container) (typed FeaturePython)
  n = 2
  ref = H_element
FEATURE [App::DocumentObjectGroupPython] O_element080  label="O_element : 041"  # scripted group (container) (typed FeaturePython)
  n = 1
  ref = O_element
FEATURE [App::DocumentObjectGroupPython] G4_POLYOXYMETHYLENE  # scripted group (container) (typed FeaturePython)
  Dunit = g/cm3
  Dvalue = 1.425
  Group = -> [C_element084,H_element078,O_element080]
  conduct = 2
  density = 1
  expand = 3
  formula = G4_POLYOXYMETHYLENE
  name = G4_POLYOXYMETHYLENE
  specific = 4
FEATURE [App::DocumentObjectGroupPython] C_element085  label="C_element : 043"  # scripted group (container) (typed FeaturePython)
  n = 2
  ref = C_element
FEATURE [App::DocumentObjectGroupPython] H_element079  label="H_element : 041"  # scripted group (container) (typed FeaturePython)
  n = 4
  ref = H_element
FEATURE [App::DocumentObjectGroupPython] G4_POLYPROPYLENE  # scripted group (container) (typed FeaturePython)
  Dunit = g/cm3
  Dvalue = 0.9
  Group = -> [C_element085,H_element079]
  conduct = 2
  density = 1
  expand = 3
  formula = G4_POLYPROPYLENE
  name = G4_POLYPROPYLENE
  specific = 4
FEATURE [App::DocumentObjectGroupPython] C_element086  label="C_element : 044"  # scripted group (container) (typed FeaturePython)
  n = 8
  ref = C_element
FEATURE [App::DocumentObjectGroupPython] H_element080  label="H_element : 042"  # scripted group (container) (typed FeaturePython)
  n = 8
  ref = H_element
FEATURE [App::DocumentObjectGroupPython] G4_POLYSTYRENE  # scripted group (container) (typed FeaturePython)
  Dunit = g/cm3
  Dvalue = 1.06
  Group = -> [C_element086,H_element080]
  conduct = 2
  density = 1
  expand = 3
  formula = G4_POLYSTYRENE
  name = G4_POLYSTYRENE
  specific = 4
FEATURE [App::DocumentObjectGroupPython] C_element087  label="C_element : 045"  # scripted group (container) (typed FeaturePython)
  n = 2
  ref = C_element
FEATURE [App::DocumentObjectGroupPython] F_element014  label="F_element : 4"  # scripted group (container) (typed FeaturePython)
  n = 4
  ref = F_element
FEATURE [App::DocumentObjectGroupPython] G4_TEFLON  # scripted group (container) (typed FeaturePython)
  Dunit = g/cm3
  Dvalue = 2.2
  Group = -> [C_element087,F_element014]
  conduct = 2
  density = 1
  expand = 3
  formula = G4_TEFLON
  name = G4_TEFLON
  specific = 4
FEATURE [App::DocumentObjectGroupPython] C_element088  label="C_element : 046"  # scripted group (container) (typed FeaturePython)
  n = 2
  ref = C_element
FEATURE [App::DocumentObjectGroupPython] F_element015  label="F_element : 006"  # scripted group (container) (typed FeaturePython)
  n = 3
  ref = F_element
FEATURE [App::DocumentObjectGroupPython] Cl_element018  label="Cl_element : 008"  # scripted group (container) (typed FeaturePython)
  n = 1
  ref = Cl_element
FEATURE [App::DocumentObjectGroupPython] G4_POLYTRIFLUOROCHLOROETHYLENE  # scripted group (container) (typed FeaturePython)
  Dunit = g/cm3
  Dvalue = 2.1
  Group = -> [C_element088,F_element015,Cl_element018]
  conduct = 2
  density = 1
  expand = 3
  formula = G4_POLYTRIFLUOROCHLOROETHYLENE
  name = G4_POLYTRIFLUOROCHLOROETHYLENE
  specific = 4
FEATURE [App::DocumentObjectGroupPython] C_element089  label="C_element : 047"  # scripted group (container) (typed FeaturePython)
  n = 4
  ref = C_element
FEATURE [App::DocumentObjectGroupPython] H_element081  label="H_element : 043"  # scripted group (container) (typed FeaturePython)
  n = 6
  ref = H_element
FEATURE [App::DocumentObjectGroupPython] O_element081  label="O_element : 042"  # scripted group (container) (typed FeaturePython)
  n = 2
  ref = O_element
FEATURE [App::DocumentObjectGroupPython] G4_POLYVINYL_ACETATE  # scripted group (container) (typed FeaturePython)
  Dunit = g/cm3
  Dvalue = 1.19
  Group = -> [C_element089,H_element081,O_element081]
  conduct = 2
  density = 1
  expand = 3
  formula = G4_POLYVINYL_ACETATE
  name = G4_POLYVINYL_ACETATE
  specific = 4
FEATURE [App::DocumentObjectGroupPython] C_element090  label="C_element : 048"  # scripted group (container) (typed FeaturePython)
  n = 2
  ref = C_element
FEATURE [App::DocumentObjectGroupPython] H_element082  label="H_element : 044"  # scripted group (container) (typed FeaturePython)
  n = 4
  ref = H_element
FEATURE [App::DocumentObjectGroupPython] O_element082  label="O_element : 043"  # scripted group (container) (typed FeaturePython)
  n = 1
  ref = O_element
FEATURE [App::DocumentObjectGroupPython] G4_POLYVINYL_ALCOHOL  # scripted group (container) (typed FeaturePython)
  Dunit = g/cm3
  Dvalue = 1.3
  Group = -> [C_element090,H_element082,O_element082]
  conduct = 2
  density = 1
  expand = 3
  formula = G4_POLYVINYL_ALCOHOL
  name = G4_POLYVINYL_ALCOHOL
  specific = 4
FEATURE [App::DocumentObjectGroupPython] C_element091  label="C_element : 049"  # scripted group (container) (typed FeaturePython)
  n = 8
  ref = C_element
FEATURE [App::DocumentObjectGroupPython] H_element083  label="H_element : 045"  # scripted group (container) (typed FeaturePython)
  n = 14
  ref = H_element
FEATURE [App::DocumentObjectGroupPython] O_element083  label="O_element : 044"  # scripted group (container) (typed FeaturePython)
  n = 2
  ref = O_element
FEATURE [App::DocumentObjectGroupPython] G4_POLYVINYL_BUTYRAL  # scripted group (container) (typed FeaturePython)
  Dunit = g/cm3
  Dvalue = 1.12
  Group = -> [C_element091,H_element083,O_element083]
  conduct = 2
  density = 1
  expand = 3
  formula = G4_POLYVINYL_BUTYRAL
  name = G4_POLYVINYL_BUTYRAL
  specific = 4
FEATURE [App::DocumentObjectGroupPython] C_element092  label="C_element : 050"  # scripted group (container) (typed FeaturePython)
  n = 2
  ref = C_element
FEATURE [App::DocumentObjectGroupPython] H_element084  label="H_element : 046"  # scripted group (container) (typed FeaturePython)
  n = 3
  ref = H_element
FEATURE [App::DocumentObjectGroupPython] Cl_element019  label="Cl_element : 009"  # scripted group (container) (typed FeaturePython)
  n = 1
  ref = Cl_element
FEATURE [App::DocumentObjectGroupPython] G4_POLYVINYL_CHLORIDE  # scripted group (container) (typed FeaturePython)
  Dunit = g/cm3
  Dvalue = 1.3
  Group = -> [C_element092,H_element084,Cl_element019]
  conduct = 2
  density = 1
  expand = 3
  formula = G4_POLYVINYL_CHLORIDE
  name = G4_POLYVINYL_CHLORIDE
  specific = 4
FEATURE [App::DocumentObjectGroupPython] C_element093  label="C_element : 051"  # scripted group (container) (typed FeaturePython)
  n = 2
  ref = C_element
FEATURE [App::DocumentObjectGroupPython] H_element085  label="H_element : 047"  # scripted group (container) (typed FeaturePython)
  n = 2
  ref = H_element
FEATURE [App::DocumentObjectGroupPython] Cl_element020  label="Cl_element : 010"  # scripted group (container) (typed FeaturePython)
  n = 2
  ref = Cl_element
FEATURE [App::DocumentObjectGroupPython] G4_POLYVINYLIDENE_CHLORIDE  # scripted group (container) (typed FeaturePython)
  Dunit = g/cm3
  Dvalue = 1.7
  Group = -> [C_element093,H_element085,Cl_element020]
  conduct = 2
  density = 1
  expand = 3
  formula = G4_POLYVINYLIDENE_CHLORIDE
  name = G4_POLYVINYLIDENE_CHLORIDE
  specific = 4
FEATURE [App::DocumentObjectGroupPython] C_element094  label="C_element : 052"  # scripted group (container) (typed FeaturePython)
  n = 2
  ref = C_element
FEATURE [App::DocumentObjectGroupPython] H_element086  label="H_element : 048"  # scripted group (container) (typed FeaturePython)
  n = 2
  ref = H_element
FEATURE [App::DocumentObjectGroupPython] F_element016  label="F_element : 007"  # scripted group (container) (typed FeaturePython)
  n = 2
  ref = F_element
FEATURE [App::DocumentObjectGroupPython] G4_POLYVINYLIDENE_FLUORIDE  # scripted group (container) (typed FeaturePython)
  Dunit = g/cm3
  Dvalue = 1.76
  Group = -> [C_element094,H_element086,F_element016]
  conduct = 2
  density = 1
  expand = 3
  formula = G4_POLYVINYLIDENE_FLUORIDE
  name = G4_POLYVINYLIDENE_FLUORIDE
  specific = 4
FEATURE [App::DocumentObjectGroupPython] C_element095  label="C_element : 053"  # scripted group (container) (typed FeaturePython)
  n = 6
  ref = C_element
FEATURE [App::DocumentObjectGroupPython] H_element087  label="H_element : 9"  # scripted group (container) (typed FeaturePython)
  n = 9
  ref = H_element
FEATURE [App::DocumentObjectGroupPython] N_element037  label="N_element : 016"  # scripted group (container) (typed FeaturePython)
  n = 1
  ref = N_element
FEATURE [App::DocumentObjectGroupPython] O_element084  label="O_element : 045"  # scripted group (container) (typed FeaturePython)
  n = 1
  ref = O_element
FEATURE [App::DocumentObjectGroupPython] G4_POLYVINYL_PYRROLIDONE  # scripted group (container) (typed FeaturePython)
  Dunit = g/cm3
  Dvalue = 1.25
  Group = -> [C_element095,H_element087,N_element037,O_element084]
  conduct = 2
  density = 1
  expand = 3
  formula = G4_POLYVINYL_PYRROLIDONE
  name = G4_POLYVINYL_PYRROLIDONE
  specific = 4
FEATURE [App::DocumentObjectGroupPython] K_element008  label="K_element : 1"  # scripted group (container) (typed FeaturePython)
  n = 1
  ref = K_element
FEATURE [App::DocumentObjectGroupPython] I_element006  label="I_element : 003"  # scripted group (container) (typed FeaturePython)
  n = 1
  ref = I_element
FEATURE [App::DocumentObjectGroupPython] G4_POTASSIUM_IODIDE  # scripted group (container) (typed FeaturePython)
  Dunit = g/cm3
  Dvalue = 3.13
  Group = -> [K_element008,I_element006]
  conduct = 2
  density = 1
  expand = 3
  formula = G4_POTASSIUM_IODIDE
  name = G4_POTASSIUM_IODIDE
  specific = 4
FEATURE [App::DocumentObjectGroupPython] K_element009  label="K_element : 2"  # scripted group (container) (typed FeaturePython)
  n = 2
  ref = K_element
FEATURE [App::DocumentObjectGroupPython] O_element085  label="O_element : 046"  # scripted group (container) (typed FeaturePython)
  n = 1
  ref = O_element
FEATURE [App::DocumentObjectGroupPython] G4_POTASSIUM_OXIDE  # scripted group (container) (typed FeaturePython)
  Dunit = g/cm3
  Dvalue = 2.32
  Group = -> [K_element009,O_element085]
  conduct = 2
  density = 1
  expand = 3
  formula = G4_POTASSIUM_OXIDE
  name = G4_POTASSIUM_OXIDE
  specific = 4
FEATURE [App::DocumentObjectGroupPython] C_element096  label="C_element : 054"  # scripted group (container) (typed FeaturePython)
  n = 3
  ref = C_element
FEATURE [App::DocumentObjectGroupPython] H_element088  label="H_element : 049"  # scripted group (container) (typed FeaturePython)
  n = 8
  ref = H_element
FEATURE [App::DocumentObjectGroupPython] G4_PROPANE  # scripted group (container) (typed FeaturePython)
  Dunit = g/cm3
  Dvalue = 0.00187939
  Group = -> [C_element096,H_element088]
  conduct = 2
  density = 1
  expand = 3
  formula = G4_PROPANE
  name = G4_PROPANE
  specific = 4
FEATURE [App::DocumentObjectGroupPython] C_element097  label="C_element : 055"  # scripted group (container) (typed FeaturePython)
  n = 3
  ref = C_element
FEATURE [App::DocumentObjectGroupPython] H_element089  label="H_element : 050"  # scripted group (container) (typed FeaturePython)
  n = 8
  ref = H_element
FEATURE [App::DocumentObjectGroupPython] G4_lPROPANE  # scripted group (container) (typed FeaturePython)
  Dunit = g/cm3
  Dvalue = 0.43
  Group = -> [C_element097,H_element089]
  conduct = 2
  density = 1
  expand = 3
  formula = G4_lPROPANE
  name = G4_lPROPANE
  specific = 4
FEATURE [App::DocumentObjectGroupPython] C_element098  label="C_element : 056"  # scripted group (container) (typed FeaturePython)
  n = 3
  ref = C_element
FEATURE [App::DocumentObjectGroupPython] H_element090  label="H_element : 051"  # scripted group (container) (typed FeaturePython)
  n = 8
  ref = H_element
FEATURE [App::DocumentObjectGroupPython] O_element086  label="O_element : 047"  # scripted group (container) (typed FeaturePython)
  n = 1
  ref = O_element
FEATURE [App::DocumentObjectGroupPython] G4_N_PROPYL_ALCOHOL  label="G4_N-PROPYL_ALCOHOL"  # scripted group (container) (typed FeaturePython)
  Dunit = g/cm3
  Dvalue = 0.8035
  Group = -> [C_element098,H_element090,O_element086]
  conduct = 2
  density = 1
  expand = 3
  formula = G4_N-PROPYL_ALCOHOL
  name = G4_N-PROPYL_ALCOHOL
  specific = 4
FEATURE [App::DocumentObjectGroupPython] C_element099  label="C_element : 057"  # scripted group (container) (typed FeaturePython)
  n = 5
  ref = C_element
FEATURE [App::DocumentObjectGroupPython] H_element091  label="H_element : 052"  # scripted group (container) (typed FeaturePython)
  n = 5
  ref = H_element
FEATURE [App::DocumentObjectGroupPython] N_element038  label="N_element : 017"  # scripted group (container) (typed FeaturePython)
  n = 1
  ref = N_element
FEATURE [App::DocumentObjectGroupPython] G4_PYRIDINE  # scripted group (container) (typed FeaturePython)
  Dunit = g/cm3
  Dvalue = 0.9819
  Group = -> [C_element099,H_element091,N_element038]
  conduct = 2
  density = 1
  expand = 3
  formula = G4_PYRIDINE
  name = G4_PYRIDINE
  specific = 4
FEATURE [App::DocumentObjectGroupPython] H_element092  label="H_element : 0.144"  # scripted group (container) (typed FeaturePython)
  n = 0.143711
FEATURE [App::DocumentObjectGroupPython] C_element100  label="C_element : 0.856"  # scripted group (container) (typed FeaturePython)
  n = 0.856289
FEATURE [App::DocumentObjectGroupPython] G4_RUBBER_BUTYL  # scripted group (container) (typed FeaturePython)
  Dunit = g/cm3
  Dvalue = 0.92
  Group = -> [H_element092,C_element100]
  conduct = 2
  density = 1
  expand = 3
  formula = G4_RUBBER_BUTYL
  name = G4_RUBBER_BUTYL
  specific = 4
FEATURE [App::DocumentObjectGroupPython] H_element093  label="H_element : 0.118"  # scripted group (container) (typed FeaturePython)
  n = 0.118371
FEATURE [App::DocumentObjectGroupPython] C_element101  label="C_element : 0.882"  # scripted group (container) (typed FeaturePython)
  n = 0.881629
FEATURE [App::DocumentObjectGroupPython] G4_RUBBER_NATURAL  # scripted group (container) (typed FeaturePython)
  Dunit = g/cm3
  Dvalue = 0.92
  Group = -> [H_element093,C_element101]
  conduct = 2
  density = 1
  expand = 3
  formula = G4_RUBBER_NATURAL
  name = G4_RUBBER_NATURAL
  specific = 4
FEATURE [App::DocumentObjectGroupPython] H_element094  label="H_element : 0.145"  # scripted group (container) (typed FeaturePython)
  n = 0.05692
FEATURE [App::DocumentObjectGroupPython] C_element102  label="C_element : 0.543"  # scripted group (container) (typed FeaturePython)
  n = 0.542646
FEATURE [App::DocumentObjectGroupPython] Cl_element021  label="Cl_element : 0.400"  # scripted group (container) (typed FeaturePython)
  n = 0.400434
FEATURE [App::DocumentObjectGroupPython] G4_RUBBER_NEOPRENE  # scripted group (container) (typed FeaturePython)
  Dunit = g/cm3
  Dvalue = 1.23
  Group = -> [H_element094,C_element102,Cl_element021]
  conduct = 2
  density = 1
  expand = 3
  formula = G4_RUBBER_NEOPRENE
  name = G4_RUBBER_NEOPRENE
  specific = 4
FEATURE [App::DocumentObjectGroupPython] Si_element006  label="Si_element : 1"  # scripted group (container) (typed FeaturePython)
  n = 1
  ref = Si_element
FEATURE [App::DocumentObjectGroupPython] O_element087  label="O_element : 048"  # scripted group (container) (typed FeaturePython)
  n = 2
  ref = O_element
FEATURE [App::DocumentObjectGroupPython] G4_SILICON_DIOXIDE  # scripted group (container) (typed FeaturePython)
  Dunit = g/cm3
  Dvalue = 2.32
  Group = -> [Si_element006,O_element087]
  conduct = 2
  density = 1
  expand = 3
  formula = G4_SILICON_DIOXIDE
  name = G4_SILICON_DIOXIDE
  specific = 4
FEATURE [App::DocumentObjectGroupPython] Ag_element002  label="Ag_element : 1"  # scripted group (container) (typed FeaturePython)
  n = 1
  ref = Ag_element
FEATURE [App::DocumentObjectGroupPython] Br_element005  label="Br_element : 003"  # scripted group (container) (typed FeaturePython)
  n = 1
  ref = Br_element
FEATURE [App::DocumentObjectGroupPython] G4_SILVER_BROMIDE  # scripted group (container) (typed FeaturePython)
  Dunit = g/cm3
  Dvalue = 6.473
  Group = -> [Ag_element002,Br_element005]
  conduct = 2
  density = 1
  expand = 3
  formula = G4_SILVER_BROMIDE
  name = G4_SILVER_BROMIDE
  specific = 4
FEATURE [App::DocumentObjectGroupPython] Ag_element003  label="Ag_element : 002"  # scripted group (container) (typed FeaturePython)
  n = 1
  ref = Ag_element
FEATURE [App::DocumentObjectGroupPython] Cl_element022  label="Cl_element : 011"  # scripted group (container) (typed FeaturePython)
  n = 1
  ref = Cl_element
FEATURE [App::DocumentObjectGroupPython] G4_SILVER_CHLORIDE  # scripted group (container) (typed FeaturePython)
  Dunit = g/cm3
  Dvalue = 5.56
  Group = -> [Ag_element003,Cl_element022]
  conduct = 2
  density = 1
  expand = 3
  formula = G4_SILVER_CHLORIDE
  name = G4_SILVER_CHLORIDE
  specific = 4
FEATURE [App::DocumentObjectGroupPython] Br_element006  label="Br_element : 0.423"  # scripted group (container) (typed FeaturePython)
  n = 0.422895
FEATURE [App::DocumentObjectGroupPython] Ag_element004  label="Ag_element : 0.574"  # scripted group (container) (typed FeaturePython)
  n = 0.573748
FEATURE [App::DocumentObjectGroupPython] I_element007  label="I_element : 0.649"  # scripted group (container) (typed FeaturePython)
  n = 0.003357
FEATURE [App::DocumentObjectGroupPython] G4_SILVER_HALIDES  # scripted group (container) (typed FeaturePython)
  Dunit = g/cm3
  Dvalue = 6.47
  Group = -> [Br_element006,Ag_element004,I_element007]
  conduct = 2
  density = 1
  expand = 3
  formula = G4_SILVER_HALIDES
  name = G4_SILVER_HALIDES
  specific = 4
FEATURE [App::DocumentObjectGroupPython] Ag_element005  label="Ag_element : 003"  # scripted group (container) (typed FeaturePython)
  n = 1
  ref = Ag_element
FEATURE [App::DocumentObjectGroupPython] I_element008  label="I_element : 004"  # scripted group (container) (typed FeaturePython)
  n = 1
  ref = I_element
FEATURE [App::DocumentObjectGroupPython] G4_SILVER_IODIDE  # scripted group (container) (typed FeaturePython)
  Dunit = g/cm3
  Dvalue = 6.01
  Group = -> [Ag_element005,I_element008]
  conduct = 2
  density = 1
  expand = 3
  formula = G4_SILVER_IODIDE
  name = G4_SILVER_IODIDE
  specific = 4
FEATURE [App::DocumentObjectGroupPython] H_element095  label="H_element : 0.100"  # scripted group (container) (typed FeaturePython)
  n = 0.1
FEATURE [App::DocumentObjectGroupPython] C_element103  label="C_element : 0.204"  # scripted group (container) (typed FeaturePython)
  n = 0.204
FEATURE [App::DocumentObjectGroupPython] N_element039  label="N_element : 0.759"  # scripted group (container) (typed FeaturePython)
  n = 0.042
FEATURE [App::DocumentObjectGroupPython] O_element088  label="O_element : 0.645"  # scripted group (container) (typed FeaturePython)
  n = 0.645
FEATURE [App::DocumentObjectGroupPython] Na_element013  label="Na_element : 0.100"  # scripted group (container) (typed FeaturePython)
  n = 0.002
FEATURE [App::DocumentObjectGroupPython] P_element009  label="P_element : 0.107"  # scripted group (container) (typed FeaturePython)
  n = 0.001
FEATURE [App::DocumentObjectGroupPython] S_element020  label="S_element : 0.021"  # scripted group (container) (typed FeaturePython)
  n = 0.002
FEATURE [App::DocumentObjectGroupPython] Cl_element023  label="Cl_element : 0.590"  # scripted group (container) (typed FeaturePython)
  n = 0.003
FEATURE [App::DocumentObjectGroupPython] K_element010  label="K_element : 0.001"  # scripted group (container) (typed FeaturePython)
  n = 0.001
FEATURE [App::DocumentObjectGroupPython] G4_SKIN_ICRP  # scripted group (container) (typed FeaturePython)
  Dunit = g/cm3
  Dvalue = 1.09
  Group = -> [H_element095,C_element103,N_element039,O_element088,Na_element013,P_element009,S_element020,Cl_element023,K_element010]
  conduct = 2
  density = 1
  expand = 3
  formula = G4_SKIN_ICRP
  name = G4_SKIN_ICRP
  specific = 4
FEATURE [App::DocumentObjectGroupPython] Na_element014  label="Na_element : 2"  # scripted group (container) (typed FeaturePython)
  n = 2
  ref = Na_element
FEATURE [App::DocumentObjectGroupPython] C_element104  label="C_element : 058"  # scripted group (container) (typed FeaturePython)
  n = 1
  ref = C_element
FEATURE [App::DocumentObjectGroupPython] O_element089  label="O_element : 049"  # scripted group (container) (typed FeaturePython)
  n = 3
  ref = O_element
FEATURE [App::DocumentObjectGroupPython] G4_SODIUM_CARBONATE  # scripted group (container) (typed FeaturePython)
  Dunit = g/cm3
  Dvalue = 2.532
  Group = -> [Na_element014,C_element104,O_element089]
  conduct = 2
  density = 1
  expand = 3
  formula = G4_SODIUM_CARBONATE
  name = G4_SODIUM_CARBONATE
  specific = 4
FEATURE [App::DocumentObjectGroupPython] Na_element015  label="Na_element : 1"  # scripted group (container) (typed FeaturePython)
  n = 1
  ref = Na_element
FEATURE [App::DocumentObjectGroupPython] I_element009  label="I_element : 005"  # scripted group (container) (typed FeaturePython)
  n = 1
  ref = I_element
FEATURE [App::DocumentObjectGroupPython] G4_SODIUM_IODIDE  # scripted group (container) (typed FeaturePython)
  Dunit = g/cm3
  Dvalue = 3.667
  Group = -> [Na_element015,I_element009]
  conduct = 2
  density = 1
  expand = 3
  formula = G4_SODIUM_IODIDE
  name = G4_SODIUM_IODIDE
  specific = 4
FEATURE [App::DocumentObjectGroupPython] Na_element016  label="Na_element : 003"  # scripted group (container) (typed FeaturePython)
  n = 2
  ref = Na_element
FEATURE [App::DocumentObjectGroupPython] O_element090  label="O_element : 050"  # scripted group (container) (typed FeaturePython)
  n = 1
  ref = O_element
FEATURE [App::DocumentObjectGroupPython] G4_SODIUM_MONOXIDE  # scripted group (container) (typed FeaturePython)
  Dunit = g/cm3
  Dvalue = 2.27
  Group = -> [Na_element016,O_element090]
  conduct = 2
  density = 1
  expand = 3
  formula = G4_SODIUM_MONOXIDE
  name = G4_SODIUM_MONOXIDE
  specific = 4
FEATURE [App::DocumentObjectGroupPython] Na_element017  label="Na_element : 004"  # scripted group (container) (typed FeaturePython)
  n = 1
  ref = Na_element
FEATURE [App::DocumentObjectGroupPython] N_element040  label="N_element : 018"  # scripted group (container) (typed FeaturePython)
  n = 1
  ref = N_element
FEATURE [App::DocumentObjectGroupPython] O_element091  label="O_element : 051"  # scripted group (container) (typed FeaturePython)
  n = 3
  ref = O_element
FEATURE [App::DocumentObjectGroupPython] G4_SODIUM_NITRATE  # scripted group (container) (typed FeaturePython)
  Dunit = g/cm3
  Dvalue = 2.261
  Group = -> [Na_element017,N_element040,O_element091]
  conduct = 2
  density = 1
  expand = 3
  formula = G4_SODIUM_NITRATE
  name = G4_SODIUM_NITRATE
  specific = 4
FEATURE [App::DocumentObjectGroupPython] C_element105  label="C_element : 059"  # scripted group (container) (typed FeaturePython)
  n = 14
  ref = C_element
FEATURE [App::DocumentObjectGroupPython] H_element096  label="H_element : 053"  # scripted group (container) (typed FeaturePython)
  n = 12
  ref = H_element
FEATURE [App::DocumentObjectGroupPython] G4_STILBENE  # scripted group (container) (typed FeaturePython)
  Dunit = g/cm3
  Dvalue = 0.9707
  Group = -> [C_element105,H_element096]
  conduct = 2
  density = 1
  expand = 3
  formula = G4_STILBENE
  name = G4_STILBENE
  specific = 4
FEATURE [App::DocumentObjectGroupPython] C_element106  label="C_element : 12"  # scripted group (container) (typed FeaturePython)
  n = 12
  ref = C_element
FEATURE [App::DocumentObjectGroupPython] H_element097  label="H_element : 22"  # scripted group (container) (typed FeaturePython)
  n = 22
  ref = H_element
FEATURE [App::DocumentObjectGroupPython] O_element092  label="O_element : 11"  # scripted group (container) (typed FeaturePython)
  n = 11
  ref = O_element
FEATURE [App::DocumentObjectGroupPython] G4_SUCROSE  # scripted group (container) (typed FeaturePython)
  Dunit = g/cm3
  Dvalue = 1.5805
  Group = -> [C_element106,H_element097,O_element092]
  conduct = 2
  density = 1
  expand = 3
  formula = G4_SUCROSE
  name = G4_SUCROSE
  specific = 4
FEATURE [App::DocumentObjectGroupPython] C_element107  label="C_element : 18"  # scripted group (container) (typed FeaturePython)
  n = 18
  ref = C_element
FEATURE [App::DocumentObjectGroupPython] H_element098  label="H_element : 054"  # scripted group (container) (typed FeaturePython)
  n = 14
  ref = H_element
FEATURE [App::DocumentObjectGroupPython] G4_TERPHENYL  # scripted group (container) (typed FeaturePython)
  Dunit = g/cm3
  Dvalue = 1.24
  Group = -> [C_element107,H_element098]
  conduct = 2
  density = 1
  expand = 3
  formula = G4_TERPHENYL
  name = G4_TERPHENYL
  specific = 4
FEATURE [App::DocumentObjectGroupPython] H_element099  label="H_element : 0.146"  # scripted group (container) (typed FeaturePython)
  n = 0.106
FEATURE [App::DocumentObjectGroupPython] C_element108  label="C_element : 0.883"  # scripted group (container) (typed FeaturePython)
  n = 0.099
FEATURE [App::DocumentObjectGroupPython] N_element041  label="N_element : 0.020"  # scripted group (container) (typed FeaturePython)
  n = 0.02
FEATURE [App::DocumentObjectGroupPython] O_element093  label="O_element : 0.766"  # scripted group (container) (typed FeaturePython)
  n = 0.766
FEATURE [App::DocumentObjectGroupPython] Na_element018  label="Na_element : 0.101"  # scripted group (container) (typed FeaturePython)
  n = 0.002
FEATURE [App::DocumentObjectGroupPython] P_element010  label="P_element : 0.108"  # scripted group (container) (typed FeaturePython)
  n = 0.001
FEATURE [App::DocumentObjectGroupPython] S_element021  label="S_element : 0.022"  # scripted group (container) (typed FeaturePython)
  n = 0.002
FEATURE [App::DocumentObjectGroupPython] Cl_element024  label="Cl_element : 0.002"  # scripted group (container) (typed FeaturePython)
  n = 0.002
FEATURE [App::DocumentObjectGroupPython] K_element011  label="K_element : 0.017"  # scripted group (container) (typed FeaturePython)
  n = 0.002
FEATURE [App::DocumentObjectGroupPython] G4_TESTIS_ICRP  # scripted group (container) (typed FeaturePython)
  Dunit = g/cm3
  Dvalue = 1.04
  Group = -> [H_element099,C_element108,N_element041,O_element093,Na_element018,P_element010,S_element021,Cl_element024,K_element011]
  conduct = 2
  density = 1
  expand = 3
  formula = G4_TESTIS_ICRP
  name = G4_TESTIS_ICRP
  specific = 4
FEATURE [App::DocumentObjectGroupPython] C_element109  label="C_element : 060"  # scripted group (container) (typed FeaturePython)
  n = 2
  ref = C_element
FEATURE [App::DocumentObjectGroupPython] Cl_element025  label="Cl_element : 012"  # scripted group (container) (typed FeaturePython)
  n = 4
  ref = Cl_element
FEATURE [App::DocumentObjectGroupPython] G4_TETRACHLOROETHYLENE  # scripted group (container) (typed FeaturePython)
  Dunit = g/cm3
  Dvalue = 1.625
  Group = -> [C_element109,Cl_element025]
  conduct = 2
  density = 1
  expand = 3
  formula = G4_TETRACHLOROETHYLENE
  name = G4_TETRACHLOROETHYLENE
  specific = 4
FEATURE [App::DocumentObjectGroupPython] Tl_element001  label="Tl_element : 1"  # scripted group (container) (typed FeaturePython)
  n = 1
  ref = Tl_element
FEATURE [App::DocumentObjectGroupPython] Cl_element026  label="Cl_element : 013"  # scripted group (container) (typed FeaturePython)
  n = 1
  ref = Cl_element
FEATURE [App::DocumentObjectGroupPython] G4_THALLIUM_CHLORIDE  # scripted group (container) (typed FeaturePython)
  Dunit = g/cm3
  Dvalue = 7.004
  Group = -> [Tl_element001,Cl_element026]
  conduct = 2
  density = 1
  expand = 3
  formula = G4_THALLIUM_CHLORIDE
  name = G4_THALLIUM_CHLORIDE
  specific = 4
FEATURE [App::DocumentObjectGroupPython] H_element100  label="H_element : 0.147"  # scripted group (container) (typed FeaturePython)
  n = 0.105
FEATURE [App::DocumentObjectGroupPython] C_element110  label="C_element : 0.256"  # scripted group (container) (typed FeaturePython)
  n = 0.256
FEATURE [App::DocumentObjectGroupPython] N_element042  label="N_element : 0.760"  # scripted group (container) (typed FeaturePython)
  n = 0.027
FEATURE [App::DocumentObjectGroupPython] O_element094  label="O_element : 0.602"  # scripted group (container) (typed FeaturePython)
  n = 0.602
FEATURE [App::DocumentObjectGroupPython] Na_element019  label="Na_element : 0.102"  # scripted group (container) (typed FeaturePython)
  n = 0.001
FEATURE [App::DocumentObjectGroupPython] P_element011  label="P_element : 0.109"  # scripted group (container) (typed FeaturePython)
  n = 0.002
FEATURE [App::DocumentObjectGroupPython] S_element022  label="S_element : 0.023"  # scripted group (container) (typed FeaturePython)
  n = 0.003
FEATURE [App::DocumentObjectGroupPython] Cl_element027  label="Cl_element : 0.591"  # scripted group (container) (typed FeaturePython)
  n = 0.002
FEATURE [App::DocumentObjectGroupPython] K_element012  label="K_element : 0.018"  # scripted group (container) (typed FeaturePython)
  n = 0.002
FEATURE [App::DocumentObjectGroupPython] G4_TISSUE_SOFT_ICRP  # scripted group (container) (typed FeaturePython)
  Dunit = g/cm3
  Dvalue = 1.03
  Group = -> [H_element100,C_element110,N_element042,O_element094,Na_element019,P_element011,S_element022,Cl_element027,K_element012]
  conduct = 2
  density = 1
  expand = 3
  formula = G4_TISSUE_SOFT_ICRP
  name = G4_TISSUE_SOFT_ICRP
  specific = 4
FEATURE [App::DocumentObjectGroupPython] H_element101  label="H_element : 0.148"  # scripted group (container) (typed FeaturePython)
  n = 0.101
FEATURE [App::DocumentObjectGroupPython] C_element111  label="C_element : 0.111"  # scripted group (container) (typed FeaturePython)
  n = 0.111
FEATURE [App::DocumentObjectGroupPython] N_element043  label="N_element : 0.026"  # scripted group (container) (typed FeaturePython)
  n = 0.026
FEATURE [App::DocumentObjectGroupPython] O_element095  label="O_element : 0.762"  # scripted group (container) (typed FeaturePython)
  n = 0.762
FEATURE [App::DocumentObjectGroupPython] G4_TISSUE_SOFT_ICRU_4  label="G4_TISSUE_SOFT_ICRU-4"  # scripted group (container) (typed FeaturePython)
  Dunit = g/cm3
  Dvalue = 1
  Group = -> [H_element101,C_element111,N_element043,O_element095]
  conduct = 2
  density = 1
  expand = 3
  formula = G4_TISSUE_SOFT_ICRU-4
  name = G4_TISSUE_SOFT_ICRU-4
  specific = 4
FEATURE [App::DocumentObjectGroupPython] H_element102  label="H_element : 0.149"  # scripted group (container) (typed FeaturePython)
  n = 0.101869
FEATURE [App::DocumentObjectGroupPython] C_element112  label="C_element : 0.456"  # scripted group (container) (typed FeaturePython)
  n = 0.456179
FEATURE [App::DocumentObjectGroupPython] N_element044  label="N_element : 0.761"  # scripted group (container) (typed FeaturePython)
  n = 0.035172
FEATURE [App::DocumentObjectGroupPython] O_element096  label="O_element : 0.407"  # scripted group (container) (typed FeaturePython)
  n = 0.40678
FEATURE [App::DocumentObjectGroupPython] G4_TISSUE_METHANE  label="G4_TISSUE-METHANE"  # scripted group (container) (typed FeaturePython)
  Dunit = g/cm3
  Dvalue = 0.00106409
  Group = -> [H_element102,C_element112,N_element044,O_element096]
  conduct = 2
  density = 1
  expand = 3
  formula = G4_TISSUE-METHANE
  name = G4_TISSUE-METHANE
  specific = 4
FEATURE [App::DocumentObjectGroupPython] H_element103  label="H_element : 0.103"  # scripted group (container) (typed FeaturePython)
  n = 0.102672
FEATURE [App::DocumentObjectGroupPython] C_element113  label="C_element : 0.569"  # scripted group (container) (typed FeaturePython)
  n = 0.56894
FEATURE [App::DocumentObjectGroupPython] N_element045  label="N_element : 0.762"  # scripted group (container) (typed FeaturePython)
  n = 0.035022
FEATURE [App::DocumentObjectGroupPython] O_element097  label="O_element : 0.293"  # scripted group (container) (typed FeaturePython)
  n = 0.293366
FEATURE [App::DocumentObjectGroupPython] G4_TISSUE_PROPANE  label="G4_TISSUE-PROPANE"  # scripted group (container) (typed FeaturePython)
  Dunit = g/cm3
  Dvalue = 0.00182628
  Group = -> [H_element103,C_element113,N_element045,O_element097]
  conduct = 2
  density = 1
  expand = 3
  formula = G4_TISSUE-PROPANE
  name = G4_TISSUE-PROPANE
  specific = 4
FEATURE [App::DocumentObjectGroupPython] Ti_element003  label="Ti_element : 1"  # scripted group (container) (typed FeaturePython)
  n = 1
  ref = Ti_element
FEATURE [App::DocumentObjectGroupPython] O_element098  label="O_element : 052"  # scripted group (container) (typed FeaturePython)
  n = 2
  ref = O_element
FEATURE [App::DocumentObjectGroupPython] G4_TITANIUM_DIOXIDE  # scripted group (container) (typed FeaturePython)
  Dunit = g/cm3
  Dvalue = 4.26
  Group = -> [Ti_element003,O_element098]
  conduct = 2
  density = 1
  expand = 3
  formula = G4_TITANIUM_DIOXIDE
  name = G4_TITANIUM_DIOXIDE
  specific = 4
FEATURE [App::DocumentObjectGroupPython] C_element114  label="C_element : 061"  # scripted group (container) (typed FeaturePython)
  n = 7
  ref = C_element
FEATURE [App::DocumentObjectGroupPython] H_element104  label="H_element : 055"  # scripted group (container) (typed FeaturePython)
  n = 8
  ref = H_element
FEATURE [App::DocumentObjectGroupPython] G4_TOLUENE  # scripted group (container) (typed FeaturePython)
  Dunit = g/cm3
  Dvalue = 0.8669
  Group = -> [C_element114,H_element104]
  conduct = 2
  density = 1
  expand = 3
  formula = G4_TOLUENE
  name = G4_TOLUENE
  specific = 4
FEATURE [App::DocumentObjectGroupPython] C_element115  label="C_element : 062"  # scripted group (container) (typed FeaturePython)
  n = 2
  ref = C_element
FEATURE [App::DocumentObjectGroupPython] H_element105  label="H_element : 056"  # scripted group (container) (typed FeaturePython)
  n = 1
  ref = H_element
FEATURE [App::DocumentObjectGroupPython] Cl_element028  label="Cl_element : 014"  # scripted group (container) (typed FeaturePython)
  n = 3
  ref = Cl_element
FEATURE [App::DocumentObjectGroupPython] G4_TRICHLOROETHYLENE  # scripted group (container) (typed FeaturePython)
  Dunit = g/cm3
  Dvalue = 1.46
  Group = -> [C_element115,H_element105,Cl_element028]
  conduct = 2
  density = 1
  expand = 3
  formula = G4_TRICHLOROETHYLENE
  name = G4_TRICHLOROETHYLENE
  specific = 4
FEATURE [App::DocumentObjectGroupPython] C_element116  label="C_element : 063"  # scripted group (container) (typed FeaturePython)
  n = 6
  ref = C_element
FEATURE [App::DocumentObjectGroupPython] H_element106  label="H_element : 15"  # scripted group (container) (typed FeaturePython)
  n = 15
  ref = H_element
FEATURE [App::DocumentObjectGroupPython] O_element099  label="O_element : 053"  # scripted group (container) (typed FeaturePython)
  n = 4
  ref = O_element
FEATURE [App::DocumentObjectGroupPython] P_element012  label="P_element : 1"  # scripted group (container) (typed FeaturePython)
  n = 1
  ref = P_element
FEATURE [App::DocumentObjectGroupPython] G4_TRIETHYL_PHOSPHATE  # scripted group (container) (typed FeaturePython)
  Dunit = g/cm3
  Dvalue = 1.07
  Group = -> [C_element116,H_element106,O_element099,P_element012]
  conduct = 2
  density = 1
  expand = 3
  formula = G4_TRIETHYL_PHOSPHATE
  name = G4_TRIETHYL_PHOSPHATE
  specific = 4
FEATURE [App::DocumentObjectGroupPython] W_element003  label="W_element : 003"  # scripted group (container) (typed FeaturePython)
  n = 1
  ref = W_element
FEATURE [App::DocumentObjectGroupPython] F_element017  label="F_element : 6"  # scripted group (container) (typed FeaturePython)
  n = 6
  ref = F_element
FEATURE [App::DocumentObjectGroupPython] G4_TUNGSTEN_HEXAFLUORIDE  # scripted group (container) (typed FeaturePython)
  Dunit = g/cm3
  Dvalue = 2.4
  Group = -> [W_element003,F_element017]
  conduct = 2
  density = 1
  expand = 3
  formula = G4_TUNGSTEN_HEXAFLUORIDE
  name = G4_TUNGSTEN_HEXAFLUORIDE
  specific = 4
FEATURE [App::DocumentObjectGroupPython] U_element001  label="U_element : 1"  # scripted group (container) (typed FeaturePython)
  n = 1
  ref = U_element
FEATURE [App::DocumentObjectGroupPython] C_element117  label="C_element : 064"  # scripted group (container) (typed FeaturePython)
  n = 2
  ref = C_element
FEATURE [App::DocumentObjectGroupPython] G4_URANIUM_DICARBIDE  # scripted group (container) (typed FeaturePython)
  Dunit = g/cm3
  Dvalue = 11.28
  Group = -> [U_element001,C_element117]
  conduct = 2
  density = 1
  expand = 3
  formula = G4_URANIUM_DICARBIDE
  name = G4_URANIUM_DICARBIDE
  specific = 4
FEATURE [App::DocumentObjectGroupPython] U_element002  label="U_element : 002"  # scripted group (container) (typed FeaturePython)
  n = 1
  ref = U_element
FEATURE [App::DocumentObjectGroupPython] C_element118  label="C_element : 065"  # scripted group (container) (typed FeaturePython)
  n = 1
  ref = C_element
FEATURE [App::DocumentObjectGroupPython] G4_URANIUM_MONOCARBIDE  # scripted group (container) (typed FeaturePython)
  Dunit = g/cm3
  Dvalue = 13.63
  Group = -> [U_element002,C_element118]
  conduct = 2
  density = 1
  expand = 3
  formula = G4_URANIUM_MONOCARBIDE
  name = G4_URANIUM_MONOCARBIDE
  specific = 4
FEATURE [App::DocumentObjectGroupPython] U_element003  label="U_element : 003"  # scripted group (container) (typed FeaturePython)
  n = 1
  ref = U_element
FEATURE [App::DocumentObjectGroupPython] O_element100  label="O_element : 054"  # scripted group (container) (typed FeaturePython)
  n = 2
  ref = O_element
FEATURE [App::DocumentObjectGroupPython] G4_URANIUM_OXIDE  # scripted group (container) (typed FeaturePython)
  Dunit = g/cm3
  Dvalue = 10.96
  Group = -> [U_element003,O_element100]
  conduct = 2
  density = 1
  expand = 3
  formula = G4_URANIUM_OXIDE
  name = G4_URANIUM_OXIDE
  specific = 4
FEATURE [App::DocumentObjectGroupPython] C_element119  label="C_element : 066"  # scripted group (container) (typed FeaturePython)
  n = 1
  ref = C_element
FEATURE [App::DocumentObjectGroupPython] H_element107  label="H_element : 057"  # scripted group (container) (typed FeaturePython)
  n = 4
  ref = H_element
FEATURE [App::DocumentObjectGroupPython] N_element046  label="N_element : 019"  # scripted group (container) (typed FeaturePython)
  n = 2
  ref = N_element
FEATURE [App::DocumentObjectGroupPython] O_element101  label="O_element : 055"  # scripted group (container) (typed FeaturePython)
  n = 1
  ref = O_element
FEATURE [App::DocumentObjectGroupPython] G4_UREA  # scripted group (container) (typed FeaturePython)
  Dunit = g/cm3
  Dvalue = 1.323
  Group = -> [C_element119,H_element107,N_element046,O_element101]
  conduct = 2
  density = 1
  expand = 3
  formula = G4_UREA
  name = G4_UREA
  specific = 4
FEATURE [App::DocumentObjectGroupPython] C_element120  label="C_element : 067"  # scripted group (container) (typed FeaturePython)
  n = 5
  ref = C_element
FEATURE [App::DocumentObjectGroupPython] H_element108  label="H_element : 058"  # scripted group (container) (typed FeaturePython)
  n = 11
  ref = H_element
FEATURE [App::DocumentObjectGroupPython] N_element047  label="N_element : 020"  # scripted group (container) (typed FeaturePython)
  n = 1
  ref = N_element
FEATURE [App::DocumentObjectGroupPython] O_element102  label="O_element : 056"  # scripted group (container) (typed FeaturePython)
  n = 2
  ref = O_element
FEATURE [App::DocumentObjectGroupPython] G4_VALINE  # scripted group (container) (typed FeaturePython)
  Dunit = g/cm3
  Dvalue = 1.23
  Group = -> [C_element120,H_element108,N_element047,O_element102]
  conduct = 2
  density = 1
  expand = 3
  formula = G4_VALINE
  name = G4_VALINE
  specific = 4
FEATURE [App::DocumentObjectGroupPython] H_element109  label="H_element : 0.009"  # scripted group (container) (typed FeaturePython)
  n = 0.009417
FEATURE [App::DocumentObjectGroupPython] C_element121  label="C_element : 0.281"  # scripted group (container) (typed FeaturePython)
  n = 0.280555
FEATURE [App::DocumentObjectGroupPython] F_element018  label="F_element : 0.710"  # scripted group (container) (typed FeaturePython)
  n = 0.710028
FEATURE [App::DocumentObjectGroupPython] G4_VITON  # scripted group (container) (typed FeaturePython)
  Dunit = g/cm3
  Dvalue = 1.8
  Group = -> [H_element109,C_element121,F_element018]
  conduct = 2
  density = 1
  expand = 3
  formula = G4_VITON
  name = G4_VITON
  specific = 4
FEATURE [App::DocumentObjectGroupPython] H_element110  label="H_element : 059"  # scripted group (container) (typed FeaturePython)
  n = 2
  ref = H_element
FEATURE [App::DocumentObjectGroupPython] O_element103  label="O_element : 057"  # scripted group (container) (typed FeaturePython)
  n = 1
  ref = O_element
FEATURE [App::DocumentObjectGroupPython] G4_WATER  # scripted group (container) (typed FeaturePython)
  Dunit = g/cm3
  Dvalue = 1
  Group = -> [H_element110,O_element103]
  conduct = 2
  density = 1
  expand = 3
  formula = G4_WATER
  name = G4_WATER
  specific = 4
FEATURE [App::DocumentObjectGroupPython] H_element111  label="H_element : 060"  # scripted group (container) (typed FeaturePython)
  n = 2
  ref = H_element
FEATURE [App::DocumentObjectGroupPython] O_element104  label="O_element : 058"  # scripted group (container) (typed FeaturePython)
  n = 1
  ref = O_element
FEATURE [App::DocumentObjectGroupPython] G4_WATER_VAPOR  # scripted group (container) (typed FeaturePython)
  Dunit = g/cm3
  Dvalue = 0.000756182
  Group = -> [H_element111,O_element104]
  conduct = 2
  density = 1
  expand = 3
  formula = G4_WATER_VAPOR
  name = G4_WATER_VAPOR
  specific = 4
FEATURE [App::DocumentObjectGroupPython] C_element122  label="C_element : 068"  # scripted group (container) (typed FeaturePython)
  n = 8
  ref = C_element
FEATURE [App::DocumentObjectGroupPython] H_element112  label="H_element : 061"  # scripted group (container) (typed FeaturePython)
  n = 10
  ref = H_element
FEATURE [App::DocumentObjectGroupPython] G4_XYLENE  # scripted group (container) (typed FeaturePython)
  Dunit = g/cm3
  Dvalue = 0.87
  Group = -> [C_element122,H_element112]
  conduct = 2
  density = 1
  expand = 3
  formula = G4_XYLENE
  name = G4_XYLENE
  specific = 4
FEATURE [App::DocumentObjectGroupPython] C_element123  label="C_element : 069"  # scripted group (container) (typed FeaturePython)
  n = 1
  ref = C_element
FEATURE [App::DocumentObjectGroupPython] G4_GRAPHITE  # scripted group (container) (typed FeaturePython)
  Dunit = g/cm3
  Dvalue = 2.21
  Group = -> [C_element123]
  conduct = 2
  density = 1
  expand = 3
  formula = G4_GRAPHITE
  name = G4_GRAPHITE
  specific = 4
FEATURE [App::DocumentObjectGroupPython] NIST  # scripted group (container) (typed FeaturePython)
  Group = -> [G4_A_150_TISSUE,G4_ACETONE,G4_ACETYLENE,G4_ADENINE,G4_ADIPOSE_TISSUE_ICRP,G4_AIR,G4_ALANINE,G4_ALUMINUM_OXIDE,G4_AMBER,G4_AMMONIA,G4_ANILINE,G4_ANTHRACENE,G4_B_100_BONE,G4_BAKELITE,G4_BARIUM_FLUORIDE,G4_BARIUM_SULFATE,G4_BENZENE,G4_BERYLLIUM_OXIDE,G4_BGO,G4_BLOOD_ICRP,G4_BONE_COMPACT_ICRU,G4_BONE_CORTICAL_ICRP,G4_BORON_CARBIDE,G4_BORON_OXIDE,G4_BRAIN_ICRP,G4_BUTANE,G4_N_BUTYL_ALCOHOL,G4_C_552,+152 more]
FEATURE [App::DocumentObjectGroupPython] H_element113  label="H_element : 062"  # scripted group (container) (typed FeaturePython)
  n = 1
  ref = H_element
FEATURE [App::DocumentObjectGroupPython] G4_H  # scripted group (container) (typed FeaturePython)
  Dunit = g/cm3
  Dvalue = 8.3748e-05
  Group = -> [H_element113]
  conduct = 2
  density = 1
  expand = 3
  formula = H
  name = G4_H
  specific = 4
FEATURE [App::DocumentObjectGroupPython] He_element001  label="He_element : 1"  # scripted group (container) (typed FeaturePython)
  n = 1
  ref = He_element
FEATURE [App::DocumentObjectGroupPython] G4_He  # scripted group (container) (typed FeaturePython)
  Dunit = g/cm3
  Dvalue = 0.000166322
  Group = -> [He_element001]
  conduct = 2
  density = 1
  expand = 3
  formula = He
  name = G4_He
  specific = 4
FEATURE [App::DocumentObjectGroupPython] Li_element008  label="Li_element : 008"  # scripted group (container) (typed FeaturePython)
  n = 1
  ref = Li_element
FEATURE [App::DocumentObjectGroupPython] G4_Li  # scripted group (container) (typed FeaturePython)
  Dunit = g/cm3
  Dvalue = 0.534
  Group = -> [Li_element008]
  conduct = 2
  density = 1
  expand = 3
  formula = Li
  name = G4_Li
  specific = 4
FEATURE [App::DocumentObjectGroupPython] Be_element002  label="Be_element : 002"  # scripted group (container) (typed FeaturePython)
  n = 1
  ref = Be_element
FEATURE [App::DocumentObjectGroupPython] G4_Be  # scripted group (container) (typed FeaturePython)
  Dunit = g/cm3
  Dvalue = 1.848
  Group = -> [Be_element002]
  conduct = 2
  density = 1
  expand = 3
  formula = Be
  name = G4_Be
  specific = 4
FEATURE [App::DocumentObjectGroupPython] B_element007  label="B_element : 007"  # scripted group (container) (typed FeaturePython)
  n = 1
  ref = B_element
FEATURE [App::DocumentObjectGroupPython] G4_B  # scripted group (container) (typed FeaturePython)
  Dunit = g/cm3
  Dvalue = 2.37
  Group = -> [B_element007]
  conduct = 2
  density = 1
  expand = 3
  formula = B
  name = G4_B
  specific = 4
FEATURE [App::DocumentObjectGroupPython] C_element124  label="C_element : 070"  # scripted group (container) (typed FeaturePython)
  n = 1
  ref = C_element
FEATURE [App::DocumentObjectGroupPython] G4_C  # scripted group (container) (typed FeaturePython)
  Dunit = g/cm3
  Dvalue = 2
  Group = -> [C_element124]
  conduct = 2
  density = 1
  expand = 3
  formula = C
  name = G4_C
  specific = 4
FEATURE [App::DocumentObjectGroupPython] N_element048  label="N_element : 021"  # scripted group (container) (typed FeaturePython)
  n = 1
  ref = N_element
FEATURE [App::DocumentObjectGroupPython] G4_N  # scripted group (container) (typed FeaturePython)
  Dunit = g/cm3
  Dvalue = 0.0011652
  Group = -> [N_element048]
  conduct = 2
  density = 1
  expand = 3
  formula = N
  name = G4_N
  specific = 4
FEATURE [App::DocumentObjectGroupPython] O_element105  label="O_element : 059"  # scripted group (container) (typed FeaturePython)
  n = 1
  ref = O_element
FEATURE [App::DocumentObjectGroupPython] G4_O  # scripted group (container) (typed FeaturePython)
  Dunit = g/cm3
  Dvalue = 0.00133151
  Group = -> [O_element105]
  conduct = 2
  density = 1
  expand = 3
  formula = O
  name = G4_O
  specific = 4
FEATURE [App::DocumentObjectGroupPython] F_element019  label="F_element : 008"  # scripted group (container) (typed FeaturePython)
  n = 1
  ref = F_element
FEATURE [App::DocumentObjectGroupPython] G4_F  # scripted group (container) (typed FeaturePython)
  Dunit = g/cm3
  Dvalue = 0.00158029
  Group = -> [F_element019]
  conduct = 2
  density = 1
  expand = 3
  formula = F
  name = G4_F
  specific = 4
FEATURE [App::DocumentObjectGroupPython] Ne_element001  label="Ne_element : 1"  # scripted group (container) (typed FeaturePython)
  n = 1
  ref = Ne_element
FEATURE [App::DocumentObjectGroupPython] G4_Ne  # scripted group (container) (typed FeaturePython)
  Dunit = g/cm3
  Dvalue = 0.000838505
  Group = -> [Ne_element001]
  conduct = 2
  density = 1
  expand = 3
  formula = Ne
  name = G4_Ne
  specific = 4
FEATURE [App::DocumentObjectGroupPython] Na_element020  label="Na_element : 005"  # scripted group (container) (typed FeaturePython)
  n = 1
  ref = Na_element
FEATURE [App::DocumentObjectGroupPython] G4_Na  # scripted group (container) (typed FeaturePython)
  Dunit = g/cm3
  Dvalue = 0.971
  Group = -> [Na_element020]
  conduct = 2
  density = 1
  expand = 3
  formula = Na
  name = G4_Na
  specific = 4
FEATURE [App::DocumentObjectGroupPython] Mg_element011  label="Mg_element : 005"  # scripted group (container) (typed FeaturePython)
  n = 1
  ref = Mg_element
FEATURE [App::DocumentObjectGroupPython] G4_Mg  # scripted group (container) (typed FeaturePython)
  Dunit = g/cm3
  Dvalue = 1.74
  Group = -> [Mg_element011]
  conduct = 2
  density = 1
  expand = 3
  formula = Mg
  name = G4_Mg
  specific = 4
FEATURE [App::DocumentObjectGroupPython] Al_element004  label="Al_element : 1"  # scripted group (container) (typed FeaturePython)
  n = 1
  ref = Al_element
FEATURE [App::DocumentObjectGroupPython] G4_Al  # scripted group (container) (typed FeaturePython)
  Dunit = g/cm3
  Dvalue = 2.699
  Group = -> [Al_element004]
  conduct = 2
  density = 1
  expand = 3
  formula = Al
  name = G4_Al
  specific = 4
FEATURE [App::DocumentObjectGroupPython] Si_element007  label="Si_element : 002"  # scripted group (container) (typed FeaturePython)
  n = 1
  ref = Si_element
FEATURE [App::DocumentObjectGroupPython] G4_Si  # scripted group (container) (typed FeaturePython)
  Dunit = g/cm3
  Dvalue = 2.33
  Group = -> [Si_element007]
  conduct = 2
  density = 1
  expand = 3
  formula = Si
  name = G4_Si
  specific = 4
FEATURE [App::DocumentObjectGroupPython] P_element013  label="P_element : 002"  # scripted group (container) (typed FeaturePython)
  n = 1
  ref = P_element
FEATURE [App::DocumentObjectGroupPython] G4_P  # scripted group (container) (typed FeaturePython)
  Dunit = g/cm3
  Dvalue = 2.2
  Group = -> [P_element013]
  conduct = 2
  density = 1
  expand = 3
  formula = P
  name = G4_P
  specific = 4
FEATURE [App::DocumentObjectGroupPython] S_element023  label="S_element : 007"  # scripted group (container) (typed FeaturePython)
  n = 1
  ref = S_element
FEATURE [App::DocumentObjectGroupPython] G4_S  # scripted group (container) (typed FeaturePython)
  Dunit = g/cm3
  Dvalue = 2
  Group = -> [S_element023]
  conduct = 2
  density = 1
  expand = 3
  formula = S
  name = G4_S
  specific = 4
FEATURE [App::DocumentObjectGroupPython] Cl_element029  label="Cl_element : 015"  # scripted group (container) (typed FeaturePython)
  n = 1
  ref = Cl_element
FEATURE [App::DocumentObjectGroupPython] G4_Cl  # scripted group (container) (typed FeaturePython)
  Dunit = g/cm3
  Dvalue = 0.00299473
  Group = -> [Cl_element029]
  conduct = 2
  density = 1
  expand = 3
  formula = Cl
  name = G4_Cl
  specific = 4
FEATURE [App::DocumentObjectGroupPython] Ar_element002  label="Ar_element : 1"  # scripted group (container) (typed FeaturePython)
  n = 1
  ref = Ar_element
FEATURE [App::DocumentObjectGroupPython] G4_Ar  # scripted group (container) (typed FeaturePython)
  Dunit = g/cm3
  Dvalue = 0.00166201
  Group = -> [Ar_element002]
  conduct = 2
  density = 1
  expand = 3
  formula = Ar
  name = G4_Ar
  specific = 4
FEATURE [App::DocumentObjectGroupPython] K_element013  label="K_element : 003"  # scripted group (container) (typed FeaturePython)
  n = 1
  ref = K_element
FEATURE [App::DocumentObjectGroupPython] G4_K  # scripted group (container) (typed FeaturePython)
  Dunit = g/cm3
  Dvalue = 0.862
  Group = -> [K_element013]
  conduct = 2
  density = 1
  expand = 3
  formula = K
  name = G4_K
  specific = 4
FEATURE [App::DocumentObjectGroupPython] Ca_element014  label="Ca_element : 007"  # scripted group (container) (typed FeaturePython)
  n = 1
  ref = Ca_element
FEATURE [App::DocumentObjectGroupPython] G4_Ca  # scripted group (container) (typed FeaturePython)
  Dunit = g/cm3
  Dvalue = 1.55
  Group = -> [Ca_element014]
  conduct = 2
  density = 1
  expand = 3
  formula = Ca
  name = G4_Ca
  specific = 4
FEATURE [App::DocumentObjectGroupPython] Sc_element001  label="Sc_element : 1"  # scripted group (container) (typed FeaturePython)
  n = 1
  ref = Sc_element
FEATURE [App::DocumentObjectGroupPython] G4_Sc  # scripted group (container) (typed FeaturePython)
  Dunit = g/cm3
  Dvalue = 2.989
  Group = -> [Sc_element001]
  conduct = 2
  density = 1
  expand = 3
  formula = Sc
  name = G4_Sc
  specific = 4
FEATURE [App::DocumentObjectGroupPython] Ti_element004  label="Ti_element : 002"  # scripted group (container) (typed FeaturePython)
  n = 1
  ref = Ti_element
FEATURE [App::DocumentObjectGroupPython] G4_Ti  # scripted group (container) (typed FeaturePython)
  Dunit = g/cm3
  Dvalue = 4.54
  Group = -> [Ti_element004]
  conduct = 2
  density = 1
  expand = 3
  formula = Ti
  name = G4_Ti
  specific = 4
FEATURE [App::DocumentObjectGroupPython] V_element001  label="V_element : 1"  # scripted group (container) (typed FeaturePython)
  n = 1
  ref = V_element
FEATURE [App::DocumentObjectGroupPython] G4_V  # scripted group (container) (typed FeaturePython)
  Dunit = g/cm3
  Dvalue = 6.11
  Group = -> [V_element001]
  conduct = 2
  density = 1
  expand = 3
  formula = V
  name = G4_V
  specific = 4
FEATURE [App::DocumentObjectGroupPython] Cr_element001  label="Cr_element : 1"  # scripted group (container) (typed FeaturePython)
  n = 1
  ref = Cr_element
FEATURE [App::DocumentObjectGroupPython] G4_Cr  # scripted group (container) (typed FeaturePython)
  Dunit = g/cm3
  Dvalue = 7.18
  Group = -> [Cr_element001]
  conduct = 2
  density = 1
  expand = 3
  formula = Cr
  name = G4_Cr
  specific = 4
FEATURE [App::DocumentObjectGroupPython] Mn_element001  label="Mn_element : 1"  # scripted group (container) (typed FeaturePython)
  n = 1
  ref = Mn_element
FEATURE [App::DocumentObjectGroupPython] G4_Mn  # scripted group (container) (typed FeaturePython)
  Dunit = g/cm3
  Dvalue = 7.44
  Group = -> [Mn_element001]
  conduct = 2
  density = 1
  expand = 3
  formula = Mn
  name = G4_Mn
  specific = 4
FEATURE [App::DocumentObjectGroupPython] Fe_element007  label="Fe_element : 004"  # scripted group (container) (typed FeaturePython)
  n = 1
  ref = Fe_element
FEATURE [App::DocumentObjectGroupPython] G4_Fe  # scripted group (container) (typed FeaturePython)
  Dunit = g/cm3
  Dvalue = 7.874
  Group = -> [Fe_element007]
  conduct = 2
  density = 1
  expand = 3
  formula = Fe
  name = G4_Fe
  specific = 4
FEATURE [App::DocumentObjectGroupPython] Co_element001  label="Co_element : 1"  # scripted group (container) (typed FeaturePython)
  n = 1
  ref = Co_element
FEATURE [App::DocumentObjectGroupPython] G4_Co  # scripted group (container) (typed FeaturePython)
  Dunit = g/cm3
  Dvalue = 8.9
  Group = -> [Co_element001]
  conduct = 2
  density = 1
  expand = 3
  formula = Co
  name = G4_Co
  specific = 4
FEATURE [App::DocumentObjectGroupPython] Ni_element001  label="Ni_element : 1"  # scripted group (container) (typed FeaturePython)
  n = 1
  ref = Ni_element
FEATURE [App::DocumentObjectGroupPython] G4_Ni  # scripted group (container) (typed FeaturePython)
  Dunit = g/cm3
  Dvalue = 8.902
  Group = -> [Ni_element001]
  conduct = 2
  density = 1
  expand = 3
  formula = Ni
  name = G4_Ni
  specific = 4
FEATURE [App::DocumentObjectGroupPython] Cu_element001  label="Cu_element : 1"  # scripted group (container) (typed FeaturePython)
  n = 1
  ref = Cu_element
FEATURE [App::DocumentObjectGroupPython] G4_Cu  # scripted group (container) (typed FeaturePython)
  Dunit = g/cm3
  Dvalue = 8.96
  Group = -> [Cu_element001]
  conduct = 2
  density = 1
  expand = 3
  formula = Cu
  name = G4_Cu
  specific = 4
FEATURE [App::DocumentObjectGroupPython] Zn_element001  label="Zn_element : 1"  # scripted group (container) (typed FeaturePython)
  n = 1
  ref = Zn_element
FEATURE [App::DocumentObjectGroupPython] G4_Zn  # scripted group (container) (typed FeaturePython)
  Dunit = g/cm3
  Dvalue = 7.133
  Group = -> [Zn_element001]
  conduct = 2
  density = 1
  expand = 3
  formula = Zn
  name = G4_Zn
  specific = 4
FEATURE [App::DocumentObjectGroupPython] Ga_element002  label="Ga_element : 002"  # scripted group (container) (typed FeaturePython)
  n = 1
  ref = Ga_element
FEATURE [App::DocumentObjectGroupPython] G4_Ga  # scripted group (container) (typed FeaturePython)
  Dunit = g/cm3
  Dvalue = 5.904
  Group = -> [Ga_element002]
  conduct = 2
  density = 1
  expand = 3
  formula = Ga
  name = G4_Ga
  specific = 4
FEATURE [App::DocumentObjectGroupPython] Ge_element002  label="Ge_element : 1"  # scripted group (container) (typed FeaturePython)
  n = 1
  ref = Ge_element
FEATURE [App::DocumentObjectGroupPython] G4_Ge  # scripted group (container) (typed FeaturePython)
  Dunit = g/cm3
  Dvalue = 5.323
  Group = -> [Ge_element002]
  conduct = 2
  density = 1
  expand = 3
  formula = Ge
  name = G4_Ge
  specific = 4
FEATURE [App::DocumentObjectGroupPython] As_element003  label="As_element : 002"  # scripted group (container) (typed FeaturePython)
  n = 1
  ref = As_element
FEATURE [App::DocumentObjectGroupPython] G4_As  # scripted group (container) (typed FeaturePython)
  Dunit = g/cm3
  Dvalue = 5.73
  Group = -> [As_element003]
  conduct = 2
  density = 1
  expand = 3
  formula = As
  name = G4_As
  specific = 4
FEATURE [App::DocumentObjectGroupPython] Se_element001  label="Se_element : 1"  # scripted group (container) (typed FeaturePython)
  n = 1
  ref = Se_element
FEATURE [App::DocumentObjectGroupPython] G4_Se  # scripted group (container) (typed FeaturePython)
  Dunit = g/cm3
  Dvalue = 4.5
  Group = -> [Se_element001]
  conduct = 2
  density = 1
  expand = 3
  formula = Se
  name = G4_Se
  specific = 4
FEATURE [App::DocumentObjectGroupPython] Br_element007  label="Br_element : 004"  # scripted group (container) (typed FeaturePython)
  n = 1
  ref = Br_element
FEATURE [App::DocumentObjectGroupPython] G4_Br  # scripted group (container) (typed FeaturePython)
  Dunit = g/cm3
  Dvalue = 0.0070721
  Group = -> [Br_element007]
  conduct = 2
  density = 1
  expand = 3
  formula = Br
  name = G4_Br
  specific = 4
FEATURE [App::DocumentObjectGroupPython] Kr_element001  label="Kr_element : 1"  # scripted group (container) (typed FeaturePython)
  n = 1
  ref = Kr_element
FEATURE [App::DocumentObjectGroupPython] G4_Kr  # scripted group (container) (typed FeaturePython)
  Dunit = g/cm3
  Dvalue = 0.00347832
  Group = -> [Kr_element001]
  conduct = 2
  density = 1
  expand = 3
  formula = Kr
  name = G4_Kr
  specific = 4
FEATURE [App::DocumentObjectGroupPython] Rb_element001  label="Rb_element : 1"  # scripted group (container) (typed FeaturePython)
  n = 1
  ref = Rb_element
FEATURE [App::DocumentObjectGroupPython] G4_Rb  # scripted group (container) (typed FeaturePython)
  Dunit = g/cm3
  Dvalue = 1.532
  Group = -> [Rb_element001]
  conduct = 2
  density = 1
  expand = 3
  formula = Rb
  name = G4_Rb
  specific = 4
FEATURE [App::DocumentObjectGroupPython] Sr_element001  label="Sr_element : 1"  # scripted group (container) (typed FeaturePython)
  n = 1
  ref = Sr_element
FEATURE [App::DocumentObjectGroupPython] G4_Sr  # scripted group (container) (typed FeaturePython)
  Dunit = g/cm3
  Dvalue = 2.54
  Group = -> [Sr_element001]
  conduct = 2
  density = 1
  expand = 3
  formula = Sr
  name = G4_Sr
  specific = 4
FEATURE [App::DocumentObjectGroupPython] Y_element001  label="Y_element : 1"  # scripted group (container) (typed FeaturePython)
  n = 1
  ref = Y_element
FEATURE [App::DocumentObjectGroupPython] G4_Y  # scripted group (container) (typed FeaturePython)
  Dunit = g/cm3
  Dvalue = 4.469
  Group = -> [Y_element001]
  conduct = 2
  density = 1
  expand = 3
  formula = Y
  name = G4_Y
  specific = 4
FEATURE [App::DocumentObjectGroupPython] Zr_element001  label="Zr_element : 1"  # scripted group (container) (typed FeaturePython)
  n = 1
  ref = Zr_element
FEATURE [App::DocumentObjectGroupPython] G4_Zr  # scripted group (container) (typed FeaturePython)
  Dunit = g/cm3
  Dvalue = 6.506
  Group = -> [Zr_element001]
  conduct = 2
  density = 1
  expand = 3
  formula = Zr
  name = G4_Zr
  specific = 4
FEATURE [App::DocumentObjectGroupPython] Nb_element001  label="Nb_element : 1"  # scripted group (container) (typed FeaturePython)
  n = 1
  ref = Nb_element
FEATURE [App::DocumentObjectGroupPython] G4_Nb  # scripted group (container) (typed FeaturePython)
  Dunit = g/cm3
  Dvalue = 8.57
  Group = -> [Nb_element001]
  conduct = 2
  density = 1
  expand = 3
  formula = Nb
  name = G4_Nb
  specific = 4
FEATURE [App::DocumentObjectGroupPython] Mo_element001  label="Mo_element : 1"  # scripted group (container) (typed FeaturePython)
  n = 1
  ref = Mo_element
FEATURE [App::DocumentObjectGroupPython] G4_Mo  # scripted group (container) (typed FeaturePython)
  Dunit = g/cm3
  Dvalue = 10.22
  Group = -> [Mo_element001]
  conduct = 2
  density = 1
  expand = 3
  formula = Mo
  name = G4_Mo
  specific = 4
FEATURE [App::DocumentObjectGroupPython] Tc_element001  label="Tc_element : 1"  # scripted group (container) (typed FeaturePython)
  n = 1
  ref = Tc_element
FEATURE [App::DocumentObjectGroupPython] G4_Tc  # scripted group (container) (typed FeaturePython)
  Dunit = g/cm3
  Dvalue = 11.5
  Group = -> [Tc_element001]
  conduct = 2
  density = 1
  expand = 3
  formula = Tc
  name = G4_Tc
  specific = 4
FEATURE [App::DocumentObjectGroupPython] Ru_element001  label="Ru_element : 1"  # scripted group (container) (typed FeaturePython)
  n = 1
  ref = Ru_element
FEATURE [App::DocumentObjectGroupPython] G4_Ru  # scripted group (container) (typed FeaturePython)
  Dunit = g/cm3
  Dvalue = 12.41
  Group = -> [Ru_element001]
  conduct = 2
  density = 1
  expand = 3
  formula = Ru
  name = G4_Ru
  specific = 4
FEATURE [App::DocumentObjectGroupPython] Rh_element001  label="Rh_element : 1"  # scripted group (container) (typed FeaturePython)
  n = 1
  ref = Rh_element
FEATURE [App::DocumentObjectGroupPython] G4_Rh  # scripted group (container) (typed FeaturePython)
  Dunit = g/cm3
  Dvalue = 12.41
  Group = -> [Rh_element001]
  conduct = 2
  density = 1
  expand = 3
  formula = Rh
  name = G4_Rh
  specific = 4
FEATURE [App::DocumentObjectGroupPython] Pd_element001  label="Pd_element : 1"  # scripted group (container) (typed FeaturePython)
  n = 1
  ref = Pd_element
FEATURE [App::DocumentObjectGroupPython] G4_Pd  # scripted group (container) (typed FeaturePython)
  Dunit = g/cm3
  Dvalue = 12.02
  Group = -> [Pd_element001]
  conduct = 2
  density = 1
  expand = 3
  formula = Pd
  name = G4_Pd
  specific = 4
FEATURE [App::DocumentObjectGroupPython] Ag_element006  label="Ag_element : 004"  # scripted group (container) (typed FeaturePython)
  n = 1
  ref = Ag_element
FEATURE [App::DocumentObjectGroupPython] G4_Ag  # scripted group (container) (typed FeaturePython)
  Dunit = g/cm3
  Dvalue = 10.5
  Group = -> [Ag_element006]
  conduct = 2
  density = 1
  expand = 3
  formula = Ag
  name = G4_Ag
  specific = 4
FEATURE [App::DocumentObjectGroupPython] Cd_element003  label="Cd_element : 003"  # scripted group (container) (typed FeaturePython)
  n = 1
  ref = Cd_element
FEATURE [App::DocumentObjectGroupPython] G4_Cd  # scripted group (container) (typed FeaturePython)
  Dunit = g/cm3
  Dvalue = 8.65
  Group = -> [Cd_element003]
  conduct = 2
  density = 1
  expand = 3
  formula = Cd
  name = G4_Cd
  specific = 4
FEATURE [App::DocumentObjectGroupPython] In_element001  label="In_element : 1"  # scripted group (container) (typed FeaturePython)
  n = 1
  ref = In_element
FEATURE [App::DocumentObjectGroupPython] G4_In  # scripted group (container) (typed FeaturePython)
  Dunit = g/cm3
  Dvalue = 7.31
  Group = -> [In_element001]
  conduct = 2
  density = 1
  expand = 3
  formula = In
  name = G4_In
  specific = 4
FEATURE [App::DocumentObjectGroupPython] Sn_element001  label="Sn_element : 1"  # scripted group (container) (typed FeaturePython)
  n = 1
  ref = Sn_element
FEATURE [App::DocumentObjectGroupPython] G4_Sn  # scripted group (container) (typed FeaturePython)
  Dunit = g/cm3
  Dvalue = 7.31
  Group = -> [Sn_element001]
  conduct = 2
  density = 1
  expand = 3
  formula = Sn
  name = G4_Sn
  specific = 4
FEATURE [App::DocumentObjectGroupPython] Sb_element001  label="Sb_element : 1"  # scripted group (container) (typed FeaturePython)
  n = 1
  ref = Sb_element
FEATURE [App::DocumentObjectGroupPython] G4_Sb  # scripted group (container) (typed FeaturePython)
  Dunit = g/cm3
  Dvalue = 6.691
  Group = -> [Sb_element001]
  conduct = 2
  density = 1
  expand = 3
  formula = Sb
  name = G4_Sb
  specific = 4
FEATURE [App::DocumentObjectGroupPython] Te_element002  label="Te_element : 002"  # scripted group (container) (typed FeaturePython)
  n = 1
  ref = Te_element
FEATURE [App::DocumentObjectGroupPython] G4_Te  # scripted group (container) (typed FeaturePython)
  Dunit = g/cm3
  Dvalue = 6.24
  Group = -> [Te_element002]
  conduct = 2
  density = 1
  expand = 3
  formula = Te
  name = G4_Te
  specific = 4
FEATURE [App::DocumentObjectGroupPython] I_element010  label="I_element : 006"  # scripted group (container) (typed FeaturePython)
  n = 1
  ref = I_element
FEATURE [App::DocumentObjectGroupPython] G4_I  # scripted group (container) (typed FeaturePython)
  Dunit = g/cm3
  Dvalue = 4.93
  Group = -> [I_element010]
  conduct = 2
  density = 1
  expand = 3
  formula = I
  name = G4_I
  specific = 4
FEATURE [App::DocumentObjectGroupPython] Xe_element001  label="Xe_element : 1"  # scripted group (container) (typed FeaturePython)
  n = 1
  ref = Xe_element
FEATURE [App::DocumentObjectGroupPython] G4_Xe  # scripted group (container) (typed FeaturePython)
  Dunit = g/cm3
  Dvalue = 0.00548536
  Group = -> [Xe_element001]
  conduct = 2
  density = 1
  expand = 3
  formula = Xe
  name = G4_Xe
  specific = 4
FEATURE [App::DocumentObjectGroupPython] Cs_element003  label="Cs_element : 003"  # scripted group (container) (typed FeaturePython)
  n = 1
  ref = Cs_element
FEATURE [App::DocumentObjectGroupPython] G4_Cs  # scripted group (container) (typed FeaturePython)
  Dunit = g/cm3
  Dvalue = 1.873
  Group = -> [Cs_element003]
  conduct = 2
  density = 1
  expand = 3
  formula = Cs
  name = G4_Cs
  specific = 4
FEATURE [App::DocumentObjectGroupPython] Ba_element003  label="Ba_element : 003"  # scripted group (container) (typed FeaturePython)
  n = 1
  ref = Ba_element
FEATURE [App::DocumentObjectGroupPython] G4_Ba  # scripted group (container) (typed FeaturePython)
  Dunit = g/cm3
  Dvalue = 3.5
  Group = -> [Ba_element003]
  conduct = 2
  density = 1
  expand = 3
  formula = Ba
  name = G4_Ba
  specific = 4
FEATURE [App::DocumentObjectGroupPython] La_element003  label="La_element : 003"  # scripted group (container) (typed FeaturePython)
  n = 1
  ref = La_element
FEATURE [App::DocumentObjectGroupPython] G4_La  # scripted group (container) (typed FeaturePython)
  Dunit = g/cm3
  Dvalue = 6.154
  Group = -> [La_element003]
  conduct = 2
  density = 1
  expand = 3
  formula = La
  name = G4_La
  specific = 4
FEATURE [App::DocumentObjectGroupPython] Ce_element002  label="Ce_element : 1"  # scripted group (container) (typed FeaturePython)
  n = 1
  ref = Ce_element
FEATURE [App::DocumentObjectGroupPython] G4_Ce  # scripted group (container) (typed FeaturePython)
  Dunit = g/cm3
  Dvalue = 6.657
  Group = -> [Ce_element002]
  conduct = 2
  density = 1
  expand = 3
  formula = Ce
  name = G4_Ce
  specific = 4
FEATURE [App::DocumentObjectGroupPython] Pr_element001  label="Pr_element : 1"  # scripted group (container) (typed FeaturePython)
  n = 1
  ref = Pr_element
FEATURE [App::DocumentObjectGroupPython] G4_Pr  # scripted group (container) (typed FeaturePython)
  Dunit = g/cm3
  Dvalue = 6.71
  Group = -> [Pr_element001]
  conduct = 2
  density = 1
  expand = 3
  formula = Pr
  name = G4_Pr
  specific = 4
FEATURE [App::DocumentObjectGroupPython] Nd_element001  label="Nd_element : 1"  # scripted group (container) (typed FeaturePython)
  n = 1
  ref = Nd_element
FEATURE [App::DocumentObjectGroupPython] G4_Nd  # scripted group (container) (typed FeaturePython)
  Dunit = g/cm3
  Dvalue = 6.9
  Group = -> [Nd_element001]
  conduct = 2
  density = 1
  expand = 3
  formula = Nd
  name = G4_Nd
  specific = 4
FEATURE [App::DocumentObjectGroupPython] Pm_element001  label="Pm_element : 1"  # scripted group (container) (typed FeaturePython)
  n = 1
  ref = Pm_element
FEATURE [App::DocumentObjectGroupPython] G4_Pm  # scripted group (container) (typed FeaturePython)
  Dunit = g/cm3
  Dvalue = 7.22
  Group = -> [Pm_element001]
  conduct = 2
  density = 1
  expand = 3
  formula = Pm
  name = G4_Pm
  specific = 4
FEATURE [App::DocumentObjectGroupPython] Sm_element001  label="Sm_element : 1"  # scripted group (container) (typed FeaturePython)
  n = 1
  ref = Sm_element
FEATURE [App::DocumentObjectGroupPython] G4_Sm  # scripted group (container) (typed FeaturePython)
  Dunit = g/cm3
  Dvalue = 7.46
  Group = -> [Sm_element001]
  conduct = 2
  density = 1
  expand = 3
  formula = Sm
  name = G4_Sm
  specific = 4
FEATURE [App::DocumentObjectGroupPython] Eu_element001  label="Eu_element : 1"  # scripted group (container) (typed FeaturePython)
  n = 1
  ref = Eu_element
FEATURE [App::DocumentObjectGroupPython] G4_Eu  # scripted group (container) (typed FeaturePython)
  Dunit = g/cm3
  Dvalue = 5.243
  Group = -> [Eu_element001]
  conduct = 2
  density = 1
  expand = 3
  formula = Eu
  name = G4_Eu
  specific = 4
FEATURE [App::DocumentObjectGroupPython] Gd_element002  label="Gd_element : 1"  # scripted group (container) (typed FeaturePython)
  n = 1
  ref = Gd_element
FEATURE [App::DocumentObjectGroupPython] G4_Gd  # scripted group (container) (typed FeaturePython)
  Dunit = g/cm3
  Dvalue = 7.9004
  Group = -> [Gd_element002]
  conduct = 2
  density = 1
  expand = 3
  formula = Gd
  name = G4_Gd
  specific = 4
FEATURE [App::DocumentObjectGroupPython] Tb_element001  label="Tb_element : 1"  # scripted group (container) (typed FeaturePython)
  n = 1
  ref = Tb_element
FEATURE [App::DocumentObjectGroupPython] G4_Tb  # scripted group (container) (typed FeaturePython)
  Dunit = g/cm3
  Dvalue = 8.229
  Group = -> [Tb_element001]
  conduct = 2
  density = 1
  expand = 3
  formula = Tb
  name = G4_Tb
  specific = 4
FEATURE [App::DocumentObjectGroupPython] Dy_element001  label="Dy_element : 1"  # scripted group (container) (typed FeaturePython)
  n = 1
  ref = Dy_element
FEATURE [App::DocumentObjectGroupPython] G4_Dy  # scripted group (container) (typed FeaturePython)
  Dunit = g/cm3
  Dvalue = 8.55
  Group = -> [Dy_element001]
  conduct = 2
  density = 1
  expand = 3
  formula = Dy
  name = G4_Dy
  specific = 4
FEATURE [App::DocumentObjectGroupPython] Ho_element001  label="Ho_element : 1"  # scripted group (container) (typed FeaturePython)
  n = 1
  ref = Ho_element
FEATURE [App::DocumentObjectGroupPython] G4_Ho  # scripted group (container) (typed FeaturePython)
  Dunit = g/cm3
  Dvalue = 8.795
  Group = -> [Ho_element001]
  conduct = 2
  density = 1
  expand = 3
  formula = Ho
  name = G4_Ho
  specific = 4
FEATURE [App::DocumentObjectGroupPython] Er_element001  label="Er_element : 1"  # scripted group (container) (typed FeaturePython)
  n = 1
  ref = Er_element
FEATURE [App::DocumentObjectGroupPython] G4_Er  # scripted group (container) (typed FeaturePython)
  Dunit = g/cm3
  Dvalue = 9.066
  Group = -> [Er_element001]
  conduct = 2
  density = 1
  expand = 3
  formula = Er
  name = G4_Er
  specific = 4
FEATURE [App::DocumentObjectGroupPython] Tm_element001  label="Tm_element : 1"  # scripted group (container) (typed FeaturePython)
  n = 1
  ref = Tm_element
FEATURE [App::DocumentObjectGroupPython] G4_Tm  # scripted group (container) (typed FeaturePython)
  Dunit = g/cm3
  Dvalue = 9.321
  Group = -> [Tm_element001]
  conduct = 2
  density = 1
  expand = 3
  formula = Tm
  name = G4_Tm
  specific = 4
FEATURE [App::DocumentObjectGroupPython] Yb_element001  label="Yb_element : 1"  # scripted group (container) (typed FeaturePython)
  n = 1
  ref = Yb_element
FEATURE [App::DocumentObjectGroupPython] G4_Yb  # scripted group (container) (typed FeaturePython)
  Dunit = g/cm3
  Dvalue = 6.73
  Group = -> [Yb_element001]
  conduct = 2
  density = 1
  expand = 3
  formula = Yb
  name = G4_Yb
  specific = 4
FEATURE [App::DocumentObjectGroupPython] Lu_element001  label="Lu_element : 1"  # scripted group (container) (typed FeaturePython)
  n = 1
  ref = Lu_element
FEATURE [App::DocumentObjectGroupPython] G4_Lu  # scripted group (container) (typed FeaturePython)
  Dunit = g/cm3
  Dvalue = 9.84
  Group = -> [Lu_element001]
  conduct = 2
  density = 1
  expand = 3
  formula = Lu
  name = G4_Lu
  specific = 4
FEATURE [App::DocumentObjectGroupPython] Hf_element001  label="Hf_element : 1"  # scripted group (container) (typed FeaturePython)
  n = 1
  ref = Hf_element
FEATURE [App::DocumentObjectGroupPython] G4_Hf  # scripted group (container) (typed FeaturePython)
  Dunit = g/cm3
  Dvalue = 13.31
  Group = -> [Hf_element001]
  conduct = 2
  density = 1
  expand = 3
  formula = Hf
  name = G4_Hf
  specific = 4
FEATURE [App::DocumentObjectGroupPython] Ta_element001  label="Ta_element : 1"  # scripted group (container) (typed FeaturePython)
  n = 1
  ref = Ta_element
FEATURE [App::DocumentObjectGroupPython] G4_Ta  # scripted group (container) (typed FeaturePython)
  Dunit = g/cm3
  Dvalue = 16.654
  Group = -> [Ta_element001]
  conduct = 2
  density = 1
  expand = 3
  formula = Ta
  name = G4_Ta
  specific = 4
FEATURE [App::DocumentObjectGroupPython] W_element004  label="W_element : 004"  # scripted group (container) (typed FeaturePython)
  n = 1
  ref = W_element
FEATURE [App::DocumentObjectGroupPython] G4_W  # scripted group (container) (typed FeaturePython)
  Dunit = g/cm3
  Dvalue = 19.3
  Group = -> [W_element004]
  conduct = 2
  density = 1
  expand = 3
  formula = W
  name = G4_W
  specific = 4
FEATURE [App::DocumentObjectGroupPython] Re_element001  label="Re_element : 1"  # scripted group (container) (typed FeaturePython)
  n = 1
  ref = Re_element
FEATURE [App::DocumentObjectGroupPython] G4_Re  # scripted group (container) (typed FeaturePython)
  Dunit = g/cm3
  Dvalue = 21.02
  Group = -> [Re_element001]
  conduct = 2
  density = 1
  expand = 3
  formula = Re
  name = G4_Re
  specific = 4
FEATURE [App::DocumentObjectGroupPython] Os_element001  label="Os_element : 1"  # scripted group (container) (typed FeaturePython)
  n = 1
  ref = Os_element
FEATURE [App::DocumentObjectGroupPython] G4_Os  # scripted group (container) (typed FeaturePython)
  Dunit = g/cm3
  Dvalue = 22.57
  Group = -> [Os_element001]
  conduct = 2
  density = 1
  expand = 3
  formula = Os
  name = G4_Os
  specific = 4
FEATURE [App::DocumentObjectGroupPython] Ir_element001  label="Ir_element : 1"  # scripted group (container) (typed FeaturePython)
  n = 1
  ref = Ir_element
FEATURE [App::DocumentObjectGroupPython] G4_Ir  # scripted group (container) (typed FeaturePython)
  Dunit = g/cm3
  Dvalue = 22.42
  Group = -> [Ir_element001]
  conduct = 2
  density = 1
  expand = 3
  formula = Ir
  name = G4_Ir
  specific = 4
FEATURE [App::DocumentObjectGroupPython] Pt_element001  label="Pt_element : 1"  # scripted group (container) (typed FeaturePython)
  n = 1
  ref = Pt_element
FEATURE [App::DocumentObjectGroupPython] G4_Pt  # scripted group (container) (typed FeaturePython)
  Dunit = g/cm3
  Dvalue = 21.45
  Group = -> [Pt_element001]
  conduct = 2
  density = 1
  expand = 3
  formula = Pt
  name = G4_Pt
  specific = 4
FEATURE [App::DocumentObjectGroupPython] Au_element001  label="Au_element : 1"  # scripted group (container) (typed FeaturePython)
  n = 1
  ref = Au_element
FEATURE [App::DocumentObjectGroupPython] G4_Au  # scripted group (container) (typed FeaturePython)
  Dunit = g/cm3
  Dvalue = 19.32
  Group = -> [Au_element001]
  conduct = 2
  density = 1
  expand = 3
  formula = Au
  name = G4_Au
  specific = 4
FEATURE [App::DocumentObjectGroupPython] Hg_element002  label="Hg_element : 002"  # scripted group (container) (typed FeaturePython)
  n = 1
  ref = Hg_element
FEATURE [App::DocumentObjectGroupPython] G4_Hg  # scripted group (container) (typed FeaturePython)
  Dunit = g/cm3
  Dvalue = 13.546
  Group = -> [Hg_element002]
  conduct = 2
  density = 1
  expand = 3
  formula = Hg
  name = G4_Hg
  specific = 4
FEATURE [App::DocumentObjectGroupPython] Tl_element002  label="Tl_element : 002"  # scripted group (container) (typed FeaturePython)
  n = 1
  ref = Tl_element
FEATURE [App::DocumentObjectGroupPython] G4_Tl  # scripted group (container) (typed FeaturePython)
  Dunit = g/cm3
  Dvalue = 11.72
  Group = -> [Tl_element002]
  conduct = 2
  density = 1
  expand = 3
  formula = Tl
  name = G4_Tl
  specific = 4
FEATURE [App::DocumentObjectGroupPython] Pb_element003  label="Pb_element : 1"  # scripted group (container) (typed FeaturePython)
  n = 1
  ref = Pb_element
FEATURE [App::DocumentObjectGroupPython] G4_Pb  # scripted group (container) (typed FeaturePython)
  Dunit = g/cm3
  Dvalue = 11.35
  Group = -> [Pb_element003]
  conduct = 2
  density = 1
  expand = 3
  formula = Pb
  name = G4_Pb
  specific = 4
FEATURE [App::DocumentObjectGroupPython] Bi_element002  label="Bi_element : 1"  # scripted group (container) (typed FeaturePython)
  n = 1
  ref = Bi_element
FEATURE [App::DocumentObjectGroupPython] G4_Bi  # scripted group (container) (typed FeaturePython)
  Dunit = g/cm3
  Dvalue = 9.747
  Group = -> [Bi_element002]
  conduct = 2
  density = 1
  expand = 3
  formula = Bi
  name = G4_Bi
  specific = 4
FEATURE [App::DocumentObjectGroupPython] Po_element001  label="Po_element : 1"  # scripted group (container) (typed FeaturePython)
  n = 1
  ref = Po_element
FEATURE [App::DocumentObjectGroupPython] G4_Po  # scripted group (container) (typed FeaturePython)
  Dunit = g/cm3
  Dvalue = 9.32
  Group = -> [Po_element001]
  conduct = 2
  density = 1
  expand = 3
  formula = Po
  name = G4_Po
  specific = 4
FEATURE [App::DocumentObjectGroupPython] At_element001  label="At_element : 1"  # scripted group (container) (typed FeaturePython)
  n = 1
  ref = At_element
FEATURE [App::DocumentObjectGroupPython] G4_At  # scripted group (container) (typed FeaturePython)
  Dunit = g/cm3
  Dvalue = 9.32
  Group = -> [At_element001]
  conduct = 2
  density = 1
  expand = 3
  formula = At
  name = G4_At
  specific = 4
FEATURE [App::DocumentObjectGroupPython] Rn_element001  label="Rn_element : 1"  # scripted group (container) (typed FeaturePython)
  n = 1
  ref = Rn_element
FEATURE [App::DocumentObjectGroupPython] G4_Rn  # scripted group (container) (typed FeaturePython)
  Dunit = g/cm3
  Dvalue = 0.00900662
  Group = -> [Rn_element001]
  conduct = 2
  density = 1
  expand = 3
  formula = Rn
  name = G4_Rn
  specific = 4
FEATURE [App::DocumentObjectGroupPython] Fr_element001  label="Fr_element : 1"  # scripted group (container) (typed FeaturePython)
  n = 1
  ref = Fr_element
FEATURE [App::DocumentObjectGroupPython] G4_Fr  # scripted group (container) (typed FeaturePython)
  Dunit = g/cm3
  Dvalue = 1
  Group = -> [Fr_element001]
  conduct = 2
  density = 1
  expand = 3
  formula = Fr
  name = G4_Fr
  specific = 4
FEATURE [App::DocumentObjectGroupPython] Ra_element001  label="Ra_element : 1"  # scripted group (container) (typed FeaturePython)
  n = 1
  ref = Ra_element
FEATURE [App::DocumentObjectGroupPython] G4_Ra  # scripted group (container) (typed FeaturePython)
  Dunit = g/cm3
  Dvalue = 5
  Group = -> [Ra_element001]
  conduct = 2
  density = 1
  expand = 3
  formula = Ra
  name = G4_Ra
  specific = 4
FEATURE [App::DocumentObjectGroupPython] Ac_element001  label="Ac_element : 1"  # scripted group (container) (typed FeaturePython)
  n = 1
  ref = Ac_element
FEATURE [App::DocumentObjectGroupPython] G4_Ac  # scripted group (container) (typed FeaturePython)
  Dunit = g/cm3
  Dvalue = 10.07
  Group = -> [Ac_element001]
  conduct = 2
  density = 1
  expand = 3
  formula = Ac
  name = G4_Ac
  specific = 4
FEATURE [App::DocumentObjectGroupPython] Th_element001  label="Th_element : 1"  # scripted group (container) (typed FeaturePython)
  n = 1
  ref = Th_element
FEATURE [App::DocumentObjectGroupPython] G4_Th  # scripted group (container) (typed FeaturePython)
  Dunit = g/cm3
  Dvalue = 11.72
  Group = -> [Th_element001]
  conduct = 2
  density = 1
  expand = 3
  formula = Th
  name = G4_Th
  specific = 4
FEATURE [App::DocumentObjectGroupPython] Pa_element001  label="Pa_element : 1"  # scripted group (container) (typed FeaturePython)
  n = 1
  ref = Pa_element
FEATURE [App::DocumentObjectGroupPython] G4_Pa  # scripted group (container) (typed FeaturePython)
  Dunit = g/cm3
  Dvalue = 15.37
  Group = -> [Pa_element001]
  conduct = 2
  density = 1
  expand = 3
  formula = Pa
  name = G4_Pa
  specific = 4
FEATURE [App::DocumentObjectGroupPython] U_element004  label="U_element : 004"  # scripted group (container) (typed FeaturePython)
  n = 1
  ref = U_element
FEATURE [App::DocumentObjectGroupPython] G4_U  # scripted group (container) (typed FeaturePython)
  Dunit = g/cm3
  Dvalue = 18.95
  Group = -> [U_element004]
  conduct = 2
  density = 1
  expand = 3
  formula = U
  name = G4_U
  specific = 4
FEATURE [App::DocumentObjectGroupPython] Np_element001  label="Np_element : 1"  # scripted group (container) (typed FeaturePython)
  n = 1
  ref = Np_element
FEATURE [App::DocumentObjectGroupPython] G4_Np  # scripted group (container) (typed FeaturePython)
  Dunit = g/cm3
  Dvalue = 20.25
  Group = -> [Np_element001]
  conduct = 2
  density = 1
  expand = 3
  formula = Np
  name = G4_Np
  specific = 4
FEATURE [App::DocumentObjectGroupPython] Pu_element002  label="Pu_element : 002"  # scripted group (container) (typed FeaturePython)
  n = 1
  ref = Pu_element
FEATURE [App::DocumentObjectGroupPython] G4_Pu  # scripted group (container) (typed FeaturePython)
  Dunit = g/cm3
  Dvalue = 19.84
  Group = -> [Pu_element002]
  conduct = 2
  density = 1
  expand = 3
  formula = Pu
  name = G4_Pu
  specific = 4
FEATURE [App::DocumentObjectGroupPython] Am_element001  label="Am_element : 1"  # scripted group (container) (typed FeaturePython)
  n = 1
  ref = Am_element
FEATURE [App::DocumentObjectGroupPython] G4_Am  # scripted group (container) (typed FeaturePython)
  Dunit = g/cm3
  Dvalue = 13.67
  Group = -> [Am_element001]
  conduct = 2
  density = 1
  expand = 3
  formula = Am
  name = G4_Am
  specific = 4
FEATURE [App::DocumentObjectGroupPython] Cm_element001  label="Cm_element : 1"  # scripted group (container) (typed FeaturePython)
  n = 1
  ref = Cm_element
FEATURE [App::DocumentObjectGroupPython] G4_Cm  # scripted group (container) (typed FeaturePython)
  Dunit = g/cm3
  Dvalue = 13.51
  Group = -> [Cm_element001]
  conduct = 2
  density = 1
  expand = 3
  formula = Cm
  name = G4_Cm
  specific = 4
FEATURE [App::DocumentObjectGroupPython] Bk_element001  label="Bk_element : 1"  # scripted group (container) (typed FeaturePython)
  n = 1
  ref = Bk_element
FEATURE [App::DocumentObjectGroupPython] G4_Bk  # scripted group (container) (typed FeaturePython)
  Dunit = g/cm3
  Dvalue = 14
  Group = -> [Bk_element001]
  conduct = 2
  density = 1
  expand = 3
  formula = Bk
  name = G4_Bk
  specific = 4
FEATURE [App::DocumentObjectGroupPython] Cf_element001  label="Cf_element : 1"  # scripted group (container) (typed FeaturePython)
  n = 1
  ref = Cf_element
FEATURE [App::DocumentObjectGroupPython] G4_Cf  # scripted group (container) (typed FeaturePython)
  Dunit = g/cm3
  Dvalue = 10
  Group = -> [Cf_element001]
  conduct = 2
  density = 1
  expand = 3
  formula = Cf
  name = G4_Cf
  specific = 4
FEATURE [App::DocumentObjectGroupPython] Element  # scripted group (container) (typed FeaturePython)
  Group = -> [G4_H,G4_He,G4_Li,G4_Be,G4_B,G4_C,G4_N,G4_O,G4_F,G4_Ne,G4_Na,G4_Mg,G4_Al,G4_Si,G4_P,G4_S,G4_Cl,G4_Ar,G4_K,G4_Ca,G4_Sc,G4_Ti,G4_V,G4_Cr,G4_Mn,G4_Fe,G4_Co,G4_Ni,G4_Cu,G4_Zn,G4_Ga,G4_Ge,G4_As,G4_Se,G4_Br,G4_Kr,G4_Rb,G4_Sr,G4_Y,G4_Zr,G4_Nb,G4_Mo,G4_Tc,G4_Ru,G4_Rh,G4_Pd,G4_Ag,G4_Cd,G4_In,G4_Sn,G4_Sb,G4_Te,G4_I,G4_Xe,G4_Cs,G4_Ba,G4_La,G4_Ce,G4_Pr,G4_Nd,G4_Pm,G4_Sm,G4_Eu,G4_Gd,G4_Tb,G4_Dy,G4_Ho,G4_Er,+30 more]
FEATURE [App::DocumentObjectGroupPython] H_element114  label="H_element : 063"  # scripted group (container) (typed FeaturePython)
  n = 2
  ref = H_element
FEATURE [App::DocumentObjectGroupPython] G4_lH2  # scripted group (container) (typed FeaturePython)
  Dunit = g/cm3
  Dvalue = 0.0708
  Group = -> [H_element114]
  conduct = 2
  density = 1
  expand = 3
  formula = G4_lH2
  name = G4_lH2
  specific = 4
FEATURE [App::DocumentObjectGroupPython] N_element049  label="N_element : 022"  # scripted group (container) (typed FeaturePython)
  n = 2
  ref = N_element
FEATURE [App::DocumentObjectGroupPython] G4_lN2  # scripted group (container) (typed FeaturePython)
  Dunit = g/cm3
  Dvalue = 0.807
  Group = -> [N_element049]
  conduct = 2
  density = 1
  expand = 3
  formula = G4_lN2
  name = G4_lN2
  specific = 4
FEATURE [App::DocumentObjectGroupPython] O_element106  label="O_element : 060"  # scripted group (container) (typed FeaturePython)
  n = 2
  ref = O_element
FEATURE [App::DocumentObjectGroupPython] G4_lO2  # scripted group (container) (typed FeaturePython)
  Dunit = g/cm3
  Dvalue = 1.141
  Group = -> [O_element106]
  conduct = 2
  density = 1
  expand = 3
  formula = G4_lO2
  name = G4_lO2
  specific = 4
FEATURE [App::DocumentObjectGroupPython] Ar  label="Ar : 1"  # scripted group (container) (typed FeaturePython)
  n = 1
  ref = Ar
FEATURE [App::DocumentObjectGroupPython] G4_lAr  # scripted group (container) (typed FeaturePython)
  Dunit = g/cm3
  Dvalue = 1.396
  Group = -> [Ar]
  conduct = 2
  density = 1
  expand = 3
  formula = G4_lAr
  name = G4_lAr
  specific = 4
FEATURE [App::DocumentObjectGroupPython] Br  label="Br : 1"  # scripted group (container) (typed FeaturePython)
  n = 1
  ref = Br
FEATURE [App::DocumentObjectGroupPython] G4_lBr  # scripted group (container) (typed FeaturePython)
  Dunit = g/cm3
  Dvalue = 3.1028
  Group = -> [Br]
  conduct = 2
  density = 1
  expand = 3
  formula = G4_lBr
  name = G4_lBr
  specific = 4
FEATURE [App::DocumentObjectGroupPython] Kr  label="Kr : 1"  # scripted group (container) (typed FeaturePython)
  n = 1
  ref = Kr
FEATURE [App::DocumentObjectGroupPython] G4_lKr  # scripted group (container) (typed FeaturePython)
  Dunit = g/cm3
  Dvalue = 2.418
  Group = -> [Kr]
  conduct = 2
  density = 1
  expand = 3
  formula = G4_lKr
  name = G4_lKr
  specific = 4
FEATURE [App::DocumentObjectGroupPython] Xe  label="Xe : 1"  # scripted group (container) (typed FeaturePython)
  n = 1
  ref = Xe
FEATURE [App::DocumentObjectGroupPython] G4_lXe  # scripted group (container) (typed FeaturePython)
  Dunit = g/cm3
  Dvalue = 2.953
  Group = -> [Xe]
  conduct = 2
  density = 1
  expand = 3
  formula = G4_lXe
  name = G4_lXe
  specific = 4
FEATURE [App::DocumentObjectGroupPython] O_element107  label="O_element : 061"  # scripted group (container) (typed FeaturePython)
  n = 4
  ref = O_element
FEATURE [App::DocumentObjectGroupPython] Pb_element004  label="Pb_element : 002"  # scripted group (container) (typed FeaturePython)
  n = 1
  ref = Pb_element
FEATURE [App::DocumentObjectGroupPython] W_element005  label="W_element : 005"  # scripted group (container) (typed FeaturePython)
  n = 1
  ref = W_element
FEATURE [App::DocumentObjectGroupPython] G4_PbWO4  # scripted group (container) (typed FeaturePython)
  Dunit = g/cm3
  Dvalue = 8.28
  Group = -> [O_element107,Pb_element004,W_element005]
  conduct = 2
  density = 1
  expand = 3
  formula = G4_PbWO4
  name = G4_PbWO4
  specific = 4
FEATURE [App::DocumentObjectGroupPython] alactic  label="alactic : 1"  # scripted group (container) (typed FeaturePython)
  n = 1
  ref = alactic
FEATURE [App::DocumentObjectGroupPython] G4_Galactic  # scripted group (container) (typed FeaturePython)
  Dunit = g/cm3
  Dvalue = 0
  Group = -> [alactic]
  conduct = 2
  density = 1
  expand = 3
  formula = G4_Galactic
  name = G4_Galactic
  specific = 4
FEATURE [App::DocumentObjectGroupPython] RAPHITE_POROUS  label="RAPHITE_POROUS : 1"  # scripted group (container) (typed FeaturePython)
  n = 1
  ref = RAPHITE_POROUS
FEATURE [App::DocumentObjectGroupPython] G4_GRAPHITE_POROUS  # scripted group (container) (typed FeaturePython)
  Dunit = g/cm3
  Dvalue = 1.7
  Group = -> [RAPHITE_POROUS]
  conduct = 2
  density = 1
  expand = 3
  formula = G4_GRAPHITE_POROUS
  name = G4_GRAPHITE_POROUS
  specific = 4
FEATURE [App::DocumentObjectGroupPython] H_element115  label="H_element : 0.150"  # scripted group (container) (typed FeaturePython)
  n = 0.080538
FEATURE [App::DocumentObjectGroupPython] C_element125  label="C_element : 0.600"  # scripted group (container) (typed FeaturePython)
  n = 0.599848
FEATURE [App::DocumentObjectGroupPython] O_element108  label="O_element : 0.320"  # scripted group (container) (typed FeaturePython)
  n = 0.319614
FEATURE [App::DocumentObjectGroupPython] G4_LUCITE  # scripted group (container) (typed FeaturePython)
  Dunit = g/cm3
  Dvalue = 1.19
  Group = -> [H_element115,C_element125,O_element108]
  conduct = 2
  density = 1
  expand = 3
  formula = G4_LUCITE
  name = G4_LUCITE
  specific = 4
FEATURE [App::DocumentObjectGroupPython] Cu_element002  label="Cu_element : 62"  # scripted group (container) (typed FeaturePython)
  n = 62
  ref = Cu_element
FEATURE [App::DocumentObjectGroupPython] Zn_element002  label="Zn_element : 35"  # scripted group (container) (typed FeaturePython)
  n = 35
  ref = Zn_element
FEATURE [App::DocumentObjectGroupPython] Pb_element005  label="Pb_element : 3"  # scripted group (container) (typed FeaturePython)
  n = 3
  ref = Pb_element
FEATURE [App::DocumentObjectGroupPython] G4_BRASS  # scripted group (container) (typed FeaturePython)
  Dunit = g/cm3
  Dvalue = 8.52
  Group = -> [Cu_element002,Zn_element002,Pb_element005]
  conduct = 2
  density = 1
  expand = 3
  formula = G4_BRASS
  name = G4_BRASS
  specific = 4
FEATURE [App::DocumentObjectGroupPython] Cu_element003  label="Cu_element : 89"  # scripted group (container) (typed FeaturePython)
  n = 89
  ref = Cu_element
FEATURE [App::DocumentObjectGroupPython] Zn_element003  label="Zn_element : 9"  # scripted group (container) (typed FeaturePython)
  n = 9
  ref = Zn_element
FEATURE [App::DocumentObjectGroupPython] Pb_element006  label="Pb_element : 2"  # scripted group (container) (typed FeaturePython)
  n = 2
  ref = Pb_element
FEATURE [App::DocumentObjectGroupPython] G4_BRONZE  # scripted group (container) (typed FeaturePython)
  Dunit = g/cm3
  Dvalue = 8.82
  Group = -> [Cu_element003,Zn_element003,Pb_element006]
  conduct = 2
  density = 1
  expand = 3
  formula = G4_BRONZE
  name = G4_BRONZE
  specific = 4
FEATURE [App::DocumentObjectGroupPython] Fe_element008  label="Fe_element : 74"  # scripted group (container) (typed FeaturePython)
  n = 74
  ref = Fe_element
FEATURE [App::DocumentObjectGroupPython] Cr_element002  label="Cr_element : 18"  # scripted group (container) (typed FeaturePython)
  n = 18
  ref = Cr_element
FEATURE [App::DocumentObjectGroupPython] Ni_element002  label="Ni_element : 8"  # scripted group (container) (typed FeaturePython)
  n = 8
  ref = Ni_element
FEATURE [App::DocumentObjectGroupPython] G4_STAINLESS_STEEL  label="G4_STAINLESS-STEEL"  # scripted group (container) (typed FeaturePython)
  Dunit = g/cm3
  Dvalue = 8
  Group = -> [Fe_element008,Cr_element002,Ni_element002]
  conduct = 2
  density = 1
  expand = 3
  formula = G4_STAINLESS-STEEL
  name = G4_STAINLESS-STEEL
  specific = 4
FEATURE [App::DocumentObjectGroupPython] H_element116  label="H_element : 064"  # scripted group (container) (typed FeaturePython)
  n = 18
  ref = H_element
FEATURE [App::DocumentObjectGroupPython] C_element126  label="C_element : 071"  # scripted group (container) (typed FeaturePython)
  n = 12
  ref = C_element
FEATURE [App::DocumentObjectGroupPython] O_element109  label="O_element : 062"  # scripted group (container) (typed FeaturePython)
  n = 7
  ref = O_element
FEATURE [App::DocumentObjectGroupPython] G4_CR39  # scripted group (container) (typed FeaturePython)
  Dunit = g/cm3
  Dvalue = 1.32
  Group = -> [H_element116,C_element126,O_element109]
  conduct = 2
  density = 1
  expand = 3
  formula = G4_CR39
  name = G4_CR39
  specific = 4
FEATURE [App::DocumentObjectGroupPython] H_element117  label="H_element : 38"  # scripted group (container) (typed FeaturePython)
  n = 38
  ref = H_element
FEATURE [App::DocumentObjectGroupPython] C_element127  label="C_element : 072"  # scripted group (container) (typed FeaturePython)
  n = 18
  ref = C_element
FEATURE [App::DocumentObjectGroupPython] O_element110  label="O_element : 063"  # scripted group (container) (typed FeaturePython)
  n = 1
  ref = O_element
FEATURE [App::DocumentObjectGroupPython] G4_OCTADECANOL  # scripted group (container) (typed FeaturePython)
  Dunit = g/cm3
  Dvalue = 0.812
  Group = -> [H_element117,C_element127,O_element110]
  conduct = 2
  density = 1
  expand = 3
  formula = G4_OCTADECANOL
  name = G4_OCTADECANOL
  specific = 4
FEATURE [App::DocumentObjectGroupPython] HEP  # scripted group (container) (typed FeaturePython)
  Group = -> [G4_lH2,G4_lN2,G4_lO2,G4_lAr,G4_lBr,G4_lKr,G4_lXe,G4_PbWO4,G4_Galactic,G4_GRAPHITE_POROUS,G4_LUCITE,G4_BRASS,G4_BRONZE,G4_STAINLESS_STEEL,G4_CR39,G4_OCTADECANOL]
FEATURE [App::DocumentObjectGroupPython] C_element128  label="C_element : 073"  # scripted group (container) (typed FeaturePython)
  n = 14
  ref = C_element
FEATURE [App::DocumentObjectGroupPython] H_element118  label="H_element : 065"  # scripted group (container) (typed FeaturePython)
  n = 10
  ref = H_element
FEATURE [App::DocumentObjectGroupPython] O_element111  label="O_element : 064"  # scripted group (container) (typed FeaturePython)
  n = 2
  ref = O_element
FEATURE [App::DocumentObjectGroupPython] N_element050  label="N_element : 023"  # scripted group (container) (typed FeaturePython)
  n = 2
  ref = N_element
FEATURE [App::DocumentObjectGroupPython] G4_KEVLAR  # scripted group (container) (typed FeaturePython)
  Dunit = g/cm3
  Dvalue = 1.44
  Group = -> [C_element128,H_element118,O_element111,N_element050]
  conduct = 2
  density = 1
  expand = 3
  formula = G4_KEVLAR
  name = G4_KEVLAR
  specific = 4
FEATURE [App::DocumentObjectGroupPython] C_element129  label="C_element : 074"  # scripted group (container) (typed FeaturePython)
  n = 10
  ref = C_element
FEATURE [App::DocumentObjectGroupPython] H_element119  label="H_element : 066"  # scripted group (container) (typed FeaturePython)
  n = 8
  ref = H_element
FEATURE [App::DocumentObjectGroupPython] O_element112  label="O_element : 065"  # scripted group (container) (typed FeaturePython)
  n = 4
  ref = O_element
FEATURE [App::DocumentObjectGroupPython] G4_DACRON  # scripted group (container) (typed FeaturePython)
  Dunit = g/cm3
  Dvalue = 1.4
  Group = -> [C_element129,H_element119,O_element112]
  conduct = 2
  density = 1
  expand = 3
  formula = G4_DACRON
  name = G4_DACRON
  specific = 4
FEATURE [App::DocumentObjectGroupPython] C_element130  label="C_element : 075"  # scripted group (container) (typed FeaturePython)
  n = 4
  ref = C_element
FEATURE [App::DocumentObjectGroupPython] H_element120  label="H_element : 067"  # scripted group (container) (typed FeaturePython)
  n = 5
  ref = H_element
FEATURE [App::DocumentObjectGroupPython] Cl_element030  label="Cl_element : 016"  # scripted group (container) (typed FeaturePython)
  n = 1
  ref = Cl_element
FEATURE [App::DocumentObjectGroupPython] G4_NEOPRENE  # scripted group (container) (typed FeaturePython)
  Dunit = g/cm3
  Dvalue = 1.23
  Group = -> [C_element130,H_element120,Cl_element030]
  conduct = 2
  density = 1
  expand = 3
  formula = G4_NEOPRENE
  name = G4_NEOPRENE
  specific = 4
FEATURE [App::DocumentObjectGroupPython] Space  # scripted group (container) (typed FeaturePython)
  Group = -> [G4_KEVLAR,G4_DACRON,G4_NEOPRENE]
FEATURE [App::DocumentObjectGroupPython] H_element121  label="H_element : 068"  # scripted group (container) (typed FeaturePython)
  n = 5
  ref = H_element
FEATURE [App::DocumentObjectGroupPython] C_element131  label="C_element : 076"  # scripted group (container) (typed FeaturePython)
  n = 4
  ref = C_element
FEATURE [App::DocumentObjectGroupPython] N_element051  label="N_element : 3"  # scripted group (container) (typed FeaturePython)
  n = 3
  ref = N_element
FEATURE [App::DocumentObjectGroupPython] O_element113  label="O_element : 066"  # scripted group (container) (typed FeaturePython)
  n = 1
  ref = O_element
FEATURE [App::DocumentObjectGroupPython] G4_CYTOSINE  # scripted group (container) (typed FeaturePython)
  Dunit = g/cm3
  Dvalue = 1.55
  Group = -> [H_element121,C_element131,N_element051,O_element113]
  conduct = 2
  density = 1
  expand = 3
  formula = G4_CYTOSINE
  name = G4_CYTOSINE
  specific = 4
FEATURE [App::DocumentObjectGroupPython] H_element122  label="H_element : 069"  # scripted group (container) (typed FeaturePython)
  n = 6
  ref = H_element
FEATURE [App::DocumentObjectGroupPython] C_element132  label="C_element : 077"  # scripted group (container) (typed FeaturePython)
  n = 5
  ref = C_element
FEATURE [App::DocumentObjectGroupPython] N_element052  label="N_element : 024"  # scripted group (container) (typed FeaturePython)
  n = 2
  ref = N_element
FEATURE [App::DocumentObjectGroupPython] O_element114  label="O_element : 067"  # scripted group (container) (typed FeaturePython)
  n = 2
  ref = O_element
FEATURE [App::DocumentObjectGroupPython] G4_THYMINE  # scripted group (container) (typed FeaturePython)
  Dunit = g/cm3
  Dvalue = 1.23
  Group = -> [H_element122,C_element132,N_element052,O_element114]
  conduct = 2
  density = 1
  expand = 3
  formula = G4_THYMINE
  name = G4_THYMINE
  specific = 4
FEATURE [App::DocumentObjectGroupPython] H_element123  label="H_element : 070"  # scripted group (container) (typed FeaturePython)
  n = 4
  ref = H_element
FEATURE [App::DocumentObjectGroupPython] C_element133  label="C_element : 078"  # scripted group (container) (typed FeaturePython)
  n = 4
  ref = C_element
FEATURE [App::DocumentObjectGroupPython] N_element053  label="N_element : 025"  # scripted group (container) (typed FeaturePython)
  n = 2
  ref = N_element
FEATURE [App::DocumentObjectGroupPython] O_element115  label="O_element : 068"  # scripted group (container) (typed FeaturePython)
  n = 2
  ref = O_element
FEATURE [App::DocumentObjectGroupPython] G4_URACIL  # scripted group (container) (typed FeaturePython)
  Dunit = g/cm3
  Dvalue = 1.32
  Group = -> [H_element123,C_element133,N_element053,O_element115]
  conduct = 2
  density = 1
  expand = 3
  formula = G4_URACIL
  name = G4_URACIL
  specific = 4
FEATURE [App::DocumentObjectGroupPython] H_element124  label="H_element : 071"  # scripted group (container) (typed FeaturePython)
  n = 4
  ref = H_element
FEATURE [App::DocumentObjectGroupPython] C_element134  label="C_element : 079"  # scripted group (container) (typed FeaturePython)
  n = 5
  ref = C_element
FEATURE [App::DocumentObjectGroupPython] N_element054  label="N_element : 026"  # scripted group (container) (typed FeaturePython)
  n = 5
  ref = N_element
FEATURE [App::DocumentObjectGroupPython] G4_DNA_ADENINE  # scripted group (container) (typed FeaturePython)
  Dunit = g/cm3
  Dvalue = 1
  Group = -> [H_element124,C_element134,N_element054]
  conduct = 2
  density = 1
  expand = 3
  formula = G4_DNA_ADENINE
  name = G4_DNA_ADENINE
  specific = 4
FEATURE [App::DocumentObjectGroupPython] H_element125  label="H_element : 072"  # scripted group (container) (typed FeaturePython)
  n = 4
  ref = H_element
FEATURE [App::DocumentObjectGroupPython] C_element135  label="C_element : 080"  # scripted group (container) (typed FeaturePython)
  n = 5
  ref = C_element
FEATURE [App::DocumentObjectGroupPython] N_element055  label="N_element : 027"  # scripted group (container) (typed FeaturePython)
  n = 5
  ref = N_element
FEATURE [App::DocumentObjectGroupPython] O_element116  label="O_element : 069"  # scripted group (container) (typed FeaturePython)
  n = 1
  ref = O_element
FEATURE [App::DocumentObjectGroupPython] G4_DNA_GUANINE  # scripted group (container) (typed FeaturePython)
  Dunit = g/cm3
  Dvalue = 1
  Group = -> [H_element125,C_element135,N_element055,O_element116]
  conduct = 2
  density = 1
  expand = 3
  formula = G4_DNA_GUANINE
  name = G4_DNA_GUANINE
  specific = 4
FEATURE [App::DocumentObjectGroupPython] H_element126  label="H_element : 073"  # scripted group (container) (typed FeaturePython)
  n = 4
  ref = H_element
FEATURE [App::DocumentObjectGroupPython] C_element136  label="C_element : 081"  # scripted group (container) (typed FeaturePython)
  n = 4
  ref = C_element
FEATURE [App::DocumentObjectGroupPython] N_element056  label="N_element : 028"  # scripted group (container) (typed FeaturePython)
  n = 3
  ref = N_element
FEATURE [App::DocumentObjectGroupPython] O_element117  label="O_element : 070"  # scripted group (container) (typed FeaturePython)
  n = 1
  ref = O_element
FEATURE [App::DocumentObjectGroupPython] G4_DNA_CYTOSINE  # scripted group (container) (typed FeaturePython)
  Dunit = g/cm3
  Dvalue = 1
  Group = -> [H_element126,C_element136,N_element056,O_element117]
  conduct = 2
  density = 1
  expand = 3
  formula = G4_DNA_CYTOSINE
  name = G4_DNA_CYTOSINE
  specific = 4
FEATURE [App::DocumentObjectGroupPython] H_element127  label="H_element : 074"  # scripted group (container) (typed FeaturePython)
  n = 5
  ref = H_element
FEATURE [App::DocumentObjectGroupPython] C_element137  label="C_element : 082"  # scripted group (container) (typed FeaturePython)
  n = 5
  ref = C_element
FEATURE [App::DocumentObjectGroupPython] N_element057  label="N_element : 029"  # scripted group (container) (typed FeaturePython)
  n = 2
  ref = N_element
FEATURE [App::DocumentObjectGroupPython] O_element118  label="O_element : 071"  # scripted group (container) (typed FeaturePython)
  n = 2
  ref = O_element
FEATURE [App::DocumentObjectGroupPython] G4_DNA_THYMINE  # scripted group (container) (typed FeaturePython)
  Dunit = g/cm3
  Dvalue = 1
  Group = -> [H_element127,C_element137,N_element057,O_element118]
  conduct = 2
  density = 1
  expand = 3
  formula = G4_DNA_THYMINE
  name = G4_DNA_THYMINE
  specific = 4
FEATURE [App::DocumentObjectGroupPython] H_element128  label="H_element : 075"  # scripted group (container) (typed FeaturePython)
  n = 3
  ref = H_element
FEATURE [App::DocumentObjectGroupPython] C_element138  label="C_element : 083"  # scripted group (container) (typed FeaturePython)
  n = 4
  ref = C_element
FEATURE [App::DocumentObjectGroupPython] N_element058  label="N_element : 030"  # scripted group (container) (typed FeaturePython)
  n = 2
  ref = N_element
FEATURE [App::DocumentObjectGroupPython] O_element119  label="O_element : 072"  # scripted group (container) (typed FeaturePython)
  n = 2
  ref = O_element
FEATURE [App::DocumentObjectGroupPython] G4_DNA_URACIL  # scripted group (container) (typed FeaturePython)
  Dunit = g/cm3
  Dvalue = 1
  Group = -> [H_element128,C_element138,N_element058,O_element119]
  conduct = 2
  density = 1
  expand = 3
  formula = G4_DNA_URACIL
  name = G4_DNA_URACIL
  specific = 4
FEATURE [App::DocumentObjectGroupPython] H_element129  label="H_element : 076"  # scripted group (container) (typed FeaturePython)
  n = 10
  ref = H_element
FEATURE [App::DocumentObjectGroupPython] C_element139  label="C_element : 084"  # scripted group (container) (typed FeaturePython)
  n = 10
  ref = C_element
FEATURE [App::DocumentObjectGroupPython] N_element059  label="N_element : 031"  # scripted group (container) (typed FeaturePython)
  n = 5
  ref = N_element
FEATURE [App::DocumentObjectGroupPython] O_element120  label="O_element : 073"  # scripted group (container) (typed FeaturePython)
  n = 4
  ref = O_element
FEATURE [App::DocumentObjectGroupPython] G4_DNA_ADENOSINE  # scripted group (container) (typed FeaturePython)
  Dunit = g/cm3
  Dvalue = 1
  Group = -> [H_element129,C_element139,N_element059,O_element120]
  conduct = 2
  density = 1
  expand = 3
  formula = G4_DNA_ADENOSINE
  name = G4_DNA_ADENOSINE
  specific = 4
FEATURE [App::DocumentObjectGroupPython] H_element130  label="H_element : 077"  # scripted group (container) (typed FeaturePython)
  n = 10
  ref = H_element
FEATURE [App::DocumentObjectGroupPython] C_element140  label="C_element : 085"  # scripted group (container) (typed FeaturePython)
  n = 10
  ref = C_element
FEATURE [App::DocumentObjectGroupPython] N_element060  label="N_element : 032"  # scripted group (container) (typed FeaturePython)
  n = 5
  ref = N_element
FEATURE [App::DocumentObjectGroupPython] O_element121  label="O_element : 074"  # scripted group (container) (typed FeaturePython)
  n = 5
  ref = O_element
FEATURE [App::DocumentObjectGroupPython] G4_DNA_GUANOSINE  # scripted group (container) (typed FeaturePython)
  Dunit = g/cm3
  Dvalue = 1
  Group = -> [H_element130,C_element140,N_element060,O_element121]
  conduct = 2
  density = 1
  expand = 3
  formula = G4_DNA_GUANOSINE
  name = G4_DNA_GUANOSINE
  specific = 4
FEATURE [App::DocumentObjectGroupPython] H_element131  label="H_element : 078"  # scripted group (container) (typed FeaturePython)
  n = 10
  ref = H_element
FEATURE [App::DocumentObjectGroupPython] C_element141  label="C_element : 086"  # scripted group (container) (typed FeaturePython)
  n = 9
  ref = C_element
FEATURE [App::DocumentObjectGroupPython] N_element061  label="N_element : 033"  # scripted group (container) (typed FeaturePython)
  n = 3
  ref = N_element
FEATURE [App::DocumentObjectGroupPython] O_element122  label="O_element : 075"  # scripted group (container) (typed FeaturePython)
  n = 5
  ref = O_element
FEATURE [App::DocumentObjectGroupPython] G4_DNA_CYTIDINE  # scripted group (container) (typed FeaturePython)
  Dunit = g/cm3
  Dvalue = 1
  Group = -> [H_element131,C_element141,N_element061,O_element122]
  conduct = 2
  density = 1
  expand = 3
  formula = G4_DNA_CYTIDINE
  name = G4_DNA_CYTIDINE
  specific = 4
FEATURE [App::DocumentObjectGroupPython] H_element132  label="H_element : 079"  # scripted group (container) (typed FeaturePython)
  n = 9
  ref = H_element
FEATURE [App::DocumentObjectGroupPython] C_element142  label="C_element : 087"  # scripted group (container) (typed FeaturePython)
  n = 9
  ref = C_element
FEATURE [App::DocumentObjectGroupPython] N_element062  label="N_element : 034"  # scripted group (container) (typed FeaturePython)
  n = 2
  ref = N_element
FEATURE [App::DocumentObjectGroupPython] O_element123  label="O_element : 076"  # scripted group (container) (typed FeaturePython)
  n = 6
  ref = O_element
FEATURE [App::DocumentObjectGroupPython] G4_DNA_URIDINE  # scripted group (container) (typed FeaturePython)
  Dunit = g/cm3
  Dvalue = 1
  Group = -> [H_element132,C_element142,N_element062,O_element123]
  conduct = 2
  density = 1
  expand = 3
  formula = G4_DNA_URIDINE
  name = G4_DNA_URIDINE
  specific = 4
FEATURE [App::DocumentObjectGroupPython] H_element133  label="H_element : 080"  # scripted group (container) (typed FeaturePython)
  n = 11
  ref = H_element
FEATURE [App::DocumentObjectGroupPython] C_element143  label="C_element : 088"  # scripted group (container) (typed FeaturePython)
  n = 10
  ref = C_element
FEATURE [App::DocumentObjectGroupPython] N_element063  label="N_element : 035"  # scripted group (container) (typed FeaturePython)
  n = 2
  ref = N_element
FEATURE [App::DocumentObjectGroupPython] O_element124  label="O_element : 077"  # scripted group (container) (typed FeaturePython)
  n = 6
  ref = O_element
FEATURE [App::DocumentObjectGroupPython] G4_DNA_METHYLURIDINE  # scripted group (container) (typed FeaturePython)
  Dunit = g/cm3
  Dvalue = 1
  Group = -> [H_element133,C_element143,N_element063,O_element124]
  conduct = 2
  density = 1
  expand = 3
  formula = G4_DNA_METHYLURIDINE
  name = G4_DNA_METHYLURIDINE
  specific = 4
FEATURE [App::DocumentObjectGroupPython] P_element014  label="P_element : 003"  # scripted group (container) (typed FeaturePython)
  n = 1
  ref = P_element
FEATURE [App::DocumentObjectGroupPython] O_element125  label="O_element : 078"  # scripted group (container) (typed FeaturePython)
  n = 3
  ref = O_element
FEATURE [App::DocumentObjectGroupPython] G4_DNA_MONOPHOSPHATE  # scripted group (container) (typed FeaturePython)
  Dunit = g/cm3
  Dvalue = 1
  Group = -> [P_element014,O_element125]
  conduct = 2
  density = 1
  expand = 3
  formula = G4_DNA_MONOPHOSPHATE
  name = G4_DNA_MONOPHOSPHATE
  specific = 4
FEATURE [App::DocumentObjectGroupPython] H_element134  label="H_element : 081"  # scripted group (container) (typed FeaturePython)
  n = 10
  ref = H_element
FEATURE [App::DocumentObjectGroupPython] C_element144  label="C_element : 089"  # scripted group (container) (typed FeaturePython)
  n = 10
  ref = C_element
FEATURE [App::DocumentObjectGroupPython] N_element064  label="N_element : 036"  # scripted group (container) (typed FeaturePython)
  n = 5
  ref = N_element
FEATURE [App::DocumentObjectGroupPython] O_element126  label="O_element : 079"  # scripted group (container) (typed FeaturePython)
  n = 7
  ref = O_element
FEATURE [App::DocumentObjectGroupPython] P_element015  label="P_element : 004"  # scripted group (container) (typed FeaturePython)
  n = 1
  ref = P_element
FEATURE [App::DocumentObjectGroupPython] G4_DNA_A  # scripted group (container) (typed FeaturePython)
  Dunit = g/cm3
  Dvalue = 1
  Group = -> [H_element134,C_element144,N_element064,O_element126,P_element015]
  conduct = 2
  density = 1
  expand = 3
  formula = G4_DNA_A
  name = G4_DNA_A
  specific = 4
FEATURE [App::DocumentObjectGroupPython] H_element135  label="H_element : 082"  # scripted group (container) (typed FeaturePython)
  n = 10
  ref = H_element
FEATURE [App::DocumentObjectGroupPython] C_element145  label="C_element : 090"  # scripted group (container) (typed FeaturePython)
  n = 10
  ref = C_element
FEATURE [App::DocumentObjectGroupPython] N_element065  label="N_element : 037"  # scripted group (container) (typed FeaturePython)
  n = 5
  ref = N_element
FEATURE [App::DocumentObjectGroupPython] O_element127  label="O_element : 8"  # scripted group (container) (typed FeaturePython)
  n = 8
  ref = O_element
FEATURE [App::DocumentObjectGroupPython] P_element016  label="P_element : 005"  # scripted group (container) (typed FeaturePython)
  n = 1
  ref = P_element
FEATURE [App::DocumentObjectGroupPython] G4_DNA_G  # scripted group (container) (typed FeaturePython)
  Dunit = g/cm3
  Dvalue = 1
  Group = -> [H_element135,C_element145,N_element065,O_element127,P_element016]
  conduct = 2
  density = 1
  expand = 3
  formula = G4_DNA_G
  name = G4_DNA_G
  specific = 4
FEATURE [App::DocumentObjectGroupPython] H_element136  label="H_element : 083"  # scripted group (container) (typed FeaturePython)
  n = 10
  ref = H_element
FEATURE [App::DocumentObjectGroupPython] C_element146  label="C_element : 091"  # scripted group (container) (typed FeaturePython)
  n = 9
  ref = C_element
FEATURE [App::DocumentObjectGroupPython] N_element066  label="N_element : 038"  # scripted group (container) (typed FeaturePython)
  n = 3
  ref = N_element
FEATURE [App::DocumentObjectGroupPython] O_element128  label="O_element : 080"  # scripted group (container) (typed FeaturePython)
  n = 8
  ref = O_element
FEATURE [App::DocumentObjectGroupPython] P_element017  label="P_element : 006"  # scripted group (container) (typed FeaturePython)
  n = 1
  ref = P_element
FEATURE [App::DocumentObjectGroupPython] G4_DNA_C  # scripted group (container) (typed FeaturePython)
  Dunit = g/cm3
  Dvalue = 1
  Group = -> [H_element136,C_element146,N_element066,O_element128,P_element017]
  conduct = 2
  density = 1
  expand = 3
  formula = G4_DNA_C
  name = G4_DNA_C
  specific = 4
FEATURE [App::DocumentObjectGroupPython] H_element137  label="H_element : 084"  # scripted group (container) (typed FeaturePython)
  n = 9
  ref = H_element
FEATURE [App::DocumentObjectGroupPython] C_element147  label="C_element : 092"  # scripted group (container) (typed FeaturePython)
  n = 9
  ref = C_element
FEATURE [App::DocumentObjectGroupPython] N_element067  label="N_element : 039"  # scripted group (container) (typed FeaturePython)
  n = 2
  ref = N_element
FEATURE [App::DocumentObjectGroupPython] O_element129  label="O_element : 9"  # scripted group (container) (typed FeaturePython)
  n = 9
  ref = O_element
FEATURE [App::DocumentObjectGroupPython] P_element018  label="P_element : 007"  # scripted group (container) (typed FeaturePython)
  n = 1
  ref = P_element
FEATURE [App::DocumentObjectGroupPython] G4_DNA_U  # scripted group (container) (typed FeaturePython)
  Dunit = g/cm3
  Dvalue = 1
  Group = -> [H_element137,C_element147,N_element067,O_element129,P_element018]
  conduct = 2
  density = 1
  expand = 3
  formula = G4_DNA_U
  name = G4_DNA_U
  specific = 4
FEATURE [App::DocumentObjectGroupPython] H_element138  label="H_element : 085"  # scripted group (container) (typed FeaturePython)
  n = 11
  ref = H_element
FEATURE [App::DocumentObjectGroupPython] C_element148  label="C_element : 093"  # scripted group (container) (typed FeaturePython)
  n = 10
  ref = C_element
FEATURE [App::DocumentObjectGroupPython] N_element068  label="N_element : 040"  # scripted group (container) (typed FeaturePython)
  n = 2
  ref = N_element
FEATURE [App::DocumentObjectGroupPython] O_element130  label="O_element : 081"  # scripted group (container) (typed FeaturePython)
  n = 9
  ref = O_element
FEATURE [App::DocumentObjectGroupPython] P_element019  label="P_element : 008"  # scripted group (container) (typed FeaturePython)
  n = 1
  ref = P_element
FEATURE [App::DocumentObjectGroupPython] G4_DNA_MU  # scripted group (container) (typed FeaturePython)
  Dunit = g/cm3
  Dvalue = 1
  Group = -> [H_element138,C_element148,N_element068,O_element130,P_element019]
  conduct = 2
  density = 1
  expand = 3
  formula = G4_DNA_MU
  name = G4_DNA_MU
  specific = 4
FEATURE [App::DocumentObjectGroupPython] BioChemical  # scripted group (container) (typed FeaturePython)
  Group = -> [G4_CYTOSINE,G4_THYMINE,G4_URACIL,G4_DNA_ADENINE,G4_DNA_GUANINE,G4_DNA_CYTOSINE,G4_DNA_THYMINE,G4_DNA_URACIL,G4_DNA_ADENOSINE,G4_DNA_GUANOSINE,G4_DNA_CYTIDINE,G4_DNA_URIDINE,G4_DNA_METHYLURIDINE,G4_DNA_MONOPHOSPHATE,G4_DNA_A,G4_DNA_G,G4_DNA_C,G4_DNA_U,G4_DNA_MU]
FEATURE [App::DocumentObjectGroupPython] G4Materials  # scripted group (container) (typed FeaturePython)
  Group = -> [NIST,Element,HEP,Space,BioChemical]
  version = 1
FEATURE [App::DocumentObjectGroupPython] Geant4  # scripted group (container) (typed FeaturePython)
  Group = -> [G4Isotopes,G4Elements,G4Materials]
FEATURE [App::DocumentObjectGroupPython] Materials  # scripted group (container) (typed FeaturePython)
  Group = -> [Geant4]
FEATURE [Part::FeaturePython] GDMLBox_WorldBox  # WARN: FeaturePython — macro-defined, semantics opaque (R4)
  lunit = 2
  material = 5
  x = 100
  y = 100
  z = 100
FEATURE [Sketcher::SketchObject] Sketch
  FullyConstrained = false
  sketch-geometry (15):
    g0-g5: Circle x6 (B-spline internal-alignment scaffolding for g6; pole/knot coordinates omitted)
    g6: BSplineCurve PolesCount=7 KnotsCount=5 Degree=3 IsPeriodic=0
    g7-g10: GeomPoint x4 (B-spline internal-alignment scaffolding for g6; pole/knot coordinates omitted)
    g11: LineSegment StartX=-4.39557 StartY=8.39124 StartZ=0 EndX=-5.2662 EndY=10.5884 EndZ=0
    g12: LineSegment StartX=-5.2662 StartY=10.5884 StartZ=0 EndX=-7.82152 EndY=9.89481 EndZ=0
    g13: LineSegment StartX=-7.82152 StartY=9.89481 StartZ=0 EndX=-9.50073 EndY=7.63152 EndZ=0
    g14: ArcOfCircle CenterX=-7.8377 CenterY=5.34547 CenterZ=0 NormalX=0 NormalY=0 NormalZ=1 AngleXU=0 Radius=2.82696 StartAngle=4.84147 EndAngle=8.48291
  constraints (9):
    c: Weight(g0) = 1
    c: Equal(g0, g1-g5) x5
    c: InternalAlignment(g0-g5 -> g6) x6
    c: InternalAlignment(g7-g10 -> g6) x4
    c: Coincident(g11,g6)
    c: Coincident(g11,g12)
    c: Coincident(g12,g13)
    c: Coincident(g14,g13)
    c: Coincident(g14,g6)
FEATURE [Part::Extrusion] Extrude
  Base = -> Sketch
  Dir = (0,0,1)
  DirMode = 2
  FaceMakerClass = Part::FaceMakerBullseye
  LengthFwd = 10
  LengthRev = 0
  Placement = pos=(13,9,0) rot=(0,0,1;0rad)
  Solid = true
  Symmetric = false
  material = 1
FEATURE [Part::Mirroring] Part__Mirroring  label="Extrude_mirror"
  Base = (0,0,0)
  Normal = (0,1,0)
  Source = -> Extrude
  material = 261
FEATURE [App::Part] Part
  Group = -> [Sketch,Extrude,Part__Mirroring]
  Origin = -> Origin001
FEATURE [App::Part] worldVOL
  Group = -> [GDMLBox_WorldBox,Part]
  Origin = -> Origin
